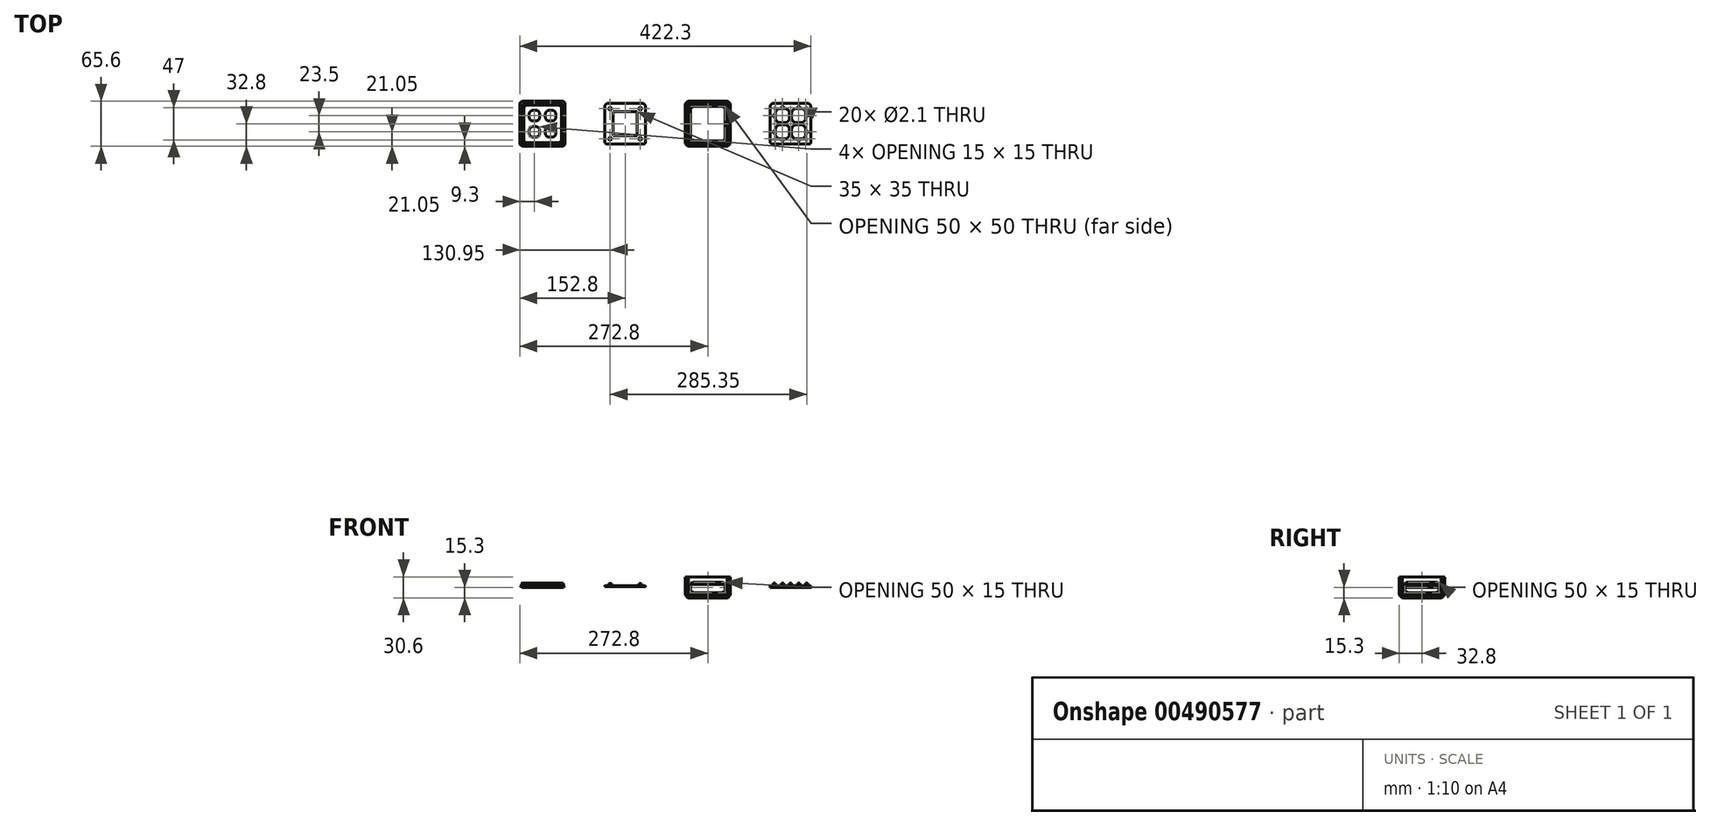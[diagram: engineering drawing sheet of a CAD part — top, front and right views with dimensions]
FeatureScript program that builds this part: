
annotation { "Feature Type Name" : "Feature", "Feature Type Description" : "" }
export const myFeature = defineFeature(function(context is Context, id is Id, definition is map)
    precondition{}
    {
        {
            assignVariable(context, id + "F0", {"name" : "Grosor", "anyValue" : 2.8});
        }
        {
            assignVariable(context, id + "F1", {"name" : "AltoPlaca", "anyValue" : 15});
        }
        {
            assignVariable(context, id + "F2", {"name" : "AltoBriX", "anyValue" : 10});
        }
        {
            var Q0;
            Q0=qCreatedBy(makeId("Top.planeOp"),FACE);
            var sketch = newSketch(context, id + "F3", { "sketchPlane" : qUnion([Q0])});
            skLineSegment(sketch, "E0.bottom", {"start": v(30, -30) * mm, "end": v(-30, -30) * mm});
            skLineSegment(sketch, "E0.top", {"start": v(30, 30) * mm, "end": v(-30, 30) * mm});
            skLineSegment(sketch, "E0.left", {"start": v(30, -30) * mm, "end": v(30, 30) * mm});
            skLineSegment(sketch, "E0.right", {"start": v(-30, -30) * mm, "end": v(-30, 30) * mm});
            skPoint(sketch, "E0.middle", {"position": v(0, 0) * mm});
            skLineSegment(sketch, "E1.0", {"start": v(32.8, 32.8) * mm, "end": v(-32.8, 32.8) * mm});
            skLineSegment(sketch, "E1.1", {"start": v(32.8, -32.8) * mm, "end": v(32.8, 32.8) * mm});
            skLineSegment(sketch, "E1.2", {"start": v(32.8, -32.8) * mm, "end": v(-32.8, -32.8) * mm});
            skLineSegment(sketch, "E1.3", {"start": v(-32.8, -32.8) * mm, "end": v(-32.8, 32.8) * mm});
            skLineSegment(sketch, "E2.bottom", {"start": v(-25, 32.8) * mm, "end": v(25, 32.8) * mm});
            skLineSegment(sketch, "E2.top", {"start": v(-25, -32.8) * mm, "end": v(25, -32.8) * mm});
            skLineSegment(sketch, "E2.left", {"start": v(-25, 32.8) * mm, "end": v(-25, -32.8) * mm});
            skLineSegment(sketch, "E2.right", {"start": v(25, 32.8) * mm, "end": v(25, -32.8) * mm});
            skLineSegment(sketch, "E3.bottom", {"start": v(-32.8, 25) * mm, "end": v(32.8, 25) * mm});
            skLineSegment(sketch, "E3.top", {"start": v(-32.8, -25) * mm, "end": v(32.8, -25) * mm});
            skLineSegment(sketch, "E3.left", {"start": v(-32.8, 25) * mm, "end": v(-32.8, -25) * mm});
            skLineSegment(sketch, "E3.right", {"start": v(32.8, 25) * mm, "end": v(32.8, -25) * mm});
            skSolve(sketch);
        }
        {
            var Q0;
            {var subQ0=sQuery(id+"F3.wireOp",EDGE,"E2.right");var subQ1=sQuery(id+"F3.wireOp",EDGE,"E0.top");var subQ2=makeQuery(id+"F3.imprint","INTERSECT",VERTEX,{"derivedFrom":[subQ1,subQ0]});Q0=makeQuery(id+"F3.imprint","IMPRINT",FACE,{"disambiguationData":[TD([[makeQuery(id+"F3.imprint","IMPRINT",EDGE,{"disambiguationData":[TD([[subQ2,-1.0]])],"derivedFrom":subQ1}),-1.0]])]});}
            var Q1;
            {var subQ7=sQuery(id+"F3.wireOp",EDGE,"E0.right");var subQ8=sQuery(id+"F3.wireOp",EDGE,"E0.top");var subQ9=makeQuery(id+"F3.imprint","INTERSECT",VERTEX,{"derivedFrom":[subQ8,subQ7]});Q1=makeQuery(id+"F3.imprint","IMPRINT",FACE,{"disambiguationData":[TD([[makeQuery(id+"F3.imprint","IMPRINT",EDGE,{"disambiguationData":[TD([[subQ9,1.0]])],"derivedFrom":subQ8}),-1.0]])]});}
            var Q2;
            {var subQ6=sQuery(id+"F3.wireOp",EDGE,"E0.top");var subQ9=sQuery(id+"F3.wireOp",EDGE,"E2.right");var subQ11=makeQuery(id+"F3.imprint","INTERSECT",VERTEX,{"derivedFrom":[subQ6,subQ9]});Q2=makeQuery(id+"F3.imprint","IMPRINT",FACE,{"disambiguationData":[TD([[makeQuery(id+"F3.imprint","IMPRINT",EDGE,{"disambiguationData":[TD([[subQ11,1.0]])],"derivedFrom":subQ6}),-1.0]])]});}
            var Q3;
            {var subQ0=sQuery(id+"F3.wireOp",EDGE,"E3.top");var subQ1=sQuery(id+"F3.wireOp",EDGE,"E0.left");var subQ2=makeQuery(id+"F3.imprint","INTERSECT",VERTEX,{"derivedFrom":[subQ1,subQ0]});Q3=makeQuery(id+"F3.imprint","IMPRINT",FACE,{"disambiguationData":[TD([[makeQuery(id+"F3.imprint","IMPRINT",EDGE,{"disambiguationData":[TD([[subQ2,-1.0]])],"derivedFrom":subQ1}),-1.0]])]});}
            var Q4;
            {var subQ0=sQuery(id+"F3.wireOp",EDGE,"E2.right");var subQ8=sQuery(id+"F3.wireOp",EDGE,"E0.bottom");var subQ11=makeQuery(id+"F3.imprint","INTERSECT",VERTEX,{"derivedFrom":[subQ8,subQ0]});Q4=makeQuery(id+"F3.imprint","IMPRINT",FACE,{"disambiguationData":[TD([[makeQuery(id+"F3.imprint","IMPRINT",EDGE,{"disambiguationData":[TD([[subQ11,1.0]])],"derivedFrom":subQ8}),1.0]])]});}
            var Q5;
            {var subQ0=sQuery(id+"F3.wireOp",EDGE,"E2.right");var subQ1=sQuery(id+"F3.wireOp",EDGE,"E0.bottom");var subQ2=makeQuery(id+"F3.imprint","INTERSECT",VERTEX,{"derivedFrom":[subQ1,subQ0]});Q5=makeQuery(id+"F3.imprint","IMPRINT",FACE,{"disambiguationData":[TD([[makeQuery(id+"F3.imprint","IMPRINT",EDGE,{"disambiguationData":[TD([[subQ2,-1.0]])],"derivedFrom":subQ1}),1.0]])]});}
            var Q6;
            {var subQ6=sQuery(id+"F3.wireOp",EDGE,"E0.right");var subQ9=sQuery(id+"F3.wireOp",EDGE,"E0.bottom");var subQ10=makeQuery(id+"F3.imprint","INTERSECT",VERTEX,{"derivedFrom":[subQ9,subQ6]});Q6=makeQuery(id+"F3.imprint","IMPRINT",FACE,{"disambiguationData":[TD([[makeQuery(id+"F3.imprint","IMPRINT",EDGE,{"disambiguationData":[TD([[subQ10,1.0]])],"derivedFrom":subQ9}),1.0]])]});}
            var Q7;
            {var subQ0=sQuery(id+"F3.wireOp",EDGE,"E3.top");var subQ1=sQuery(id+"F3.wireOp",EDGE,"E0.right");var subQ2=makeQuery(id+"F3.imprint","INTERSECT",VERTEX,{"derivedFrom":[subQ1,subQ0]});Q7=makeQuery(id+"F3.imprint","IMPRINT",FACE,{"disambiguationData":[TD([[makeQuery(id+"F3.imprint","IMPRINT",EDGE,{"disambiguationData":[TD([[subQ2,-1.0]])],"derivedFrom":subQ1}),1.0]])]});}
            var Q8;
            {var subQ0=sQuery(id+"F3.wireOp",EDGE,"E2.right");var subQ1=sQuery(id+"F3.wireOp",EDGE,"E0.bottom");var subQ2=makeQuery(id+"F3.imprint","INTERSECT",VERTEX,{"derivedFrom":[subQ1,subQ0]});Q8=makeQuery(id+"F3.imprint","IMPRINT",FACE,{"disambiguationData":[TD([[makeQuery(id+"F3.imprint","IMPRINT",EDGE,{"disambiguationData":[TD([[subQ2,1.0]])],"derivedFrom":subQ1}),-1.0]])]});}
            var Q9;
            {var subQ0=sQuery(id+"F3.wireOp",EDGE,"E2.right");var subQ1=sQuery(id+"F3.wireOp",EDGE,"E0.top");var subQ2=makeQuery(id+"F3.imprint","INTERSECT",VERTEX,{"derivedFrom":[subQ1,subQ0]});Q9=makeQuery(id+"F3.imprint","IMPRINT",FACE,{"disambiguationData":[TD([[makeQuery(id+"F3.imprint","IMPRINT",EDGE,{"disambiguationData":[TD([[subQ2,1.0]])],"derivedFrom":subQ1}),1.0]])]});}
            var Q10;
            {var subQ0=sQuery(id+"F3.wireOp",EDGE,"E0.right");var subQ1=sQuery(id+"F3.wireOp",EDGE,"E0.top");var subQ2=makeQuery(id+"F3.imprint","INTERSECT",VERTEX,{"derivedFrom":[subQ1,subQ0]});Q10=makeQuery(id+"F3.imprint","IMPRINT",FACE,{"disambiguationData":[TD([[makeQuery(id+"F3.imprint","IMPRINT",EDGE,{"disambiguationData":[TD([[subQ2,1.0]])],"derivedFrom":subQ1}),1.0]])]});}
            var Q11;
            {var subQ0=sQuery(id+"F3.wireOp",EDGE,"E3.top");var subQ1=sQuery(id+"F3.wireOp",EDGE,"E0.right");var subQ2=makeQuery(id+"F3.imprint","INTERSECT",VERTEX,{"derivedFrom":[subQ1,subQ0]});Q11=makeQuery(id+"F3.imprint","IMPRINT",FACE,{"disambiguationData":[TD([[makeQuery(id+"F3.imprint","IMPRINT",EDGE,{"disambiguationData":[TD([[subQ2,-1.0]])],"derivedFrom":subQ1}),-1.0]])]});}
            var Q12;
            {var subQ0=sQuery(id+"F3.wireOp",EDGE,"E3.top");var subQ1=sQuery(id+"F3.wireOp",EDGE,"E0.left");var subQ2=makeQuery(id+"F3.imprint","INTERSECT",VERTEX,{"derivedFrom":[subQ1,subQ0]});Q12=makeQuery(id+"F3.imprint","IMPRINT",FACE,{"disambiguationData":[TD([[makeQuery(id+"F3.imprint","IMPRINT",EDGE,{"disambiguationData":[TD([[subQ2,-1.0]])],"derivedFrom":subQ1}),1.0]])]});}
            var Q13;
            {var subQ0=sQuery(id+"F3.wireOp",EDGE,"E0.right");var subQ1=sQuery(id+"F3.wireOp",EDGE,"E0.bottom");var subQ2=makeQuery(id+"F3.imprint","INTERSECT",VERTEX,{"derivedFrom":[subQ1,subQ0]});Q13=makeQuery(id+"F3.imprint","IMPRINT",FACE,{"disambiguationData":[TD([[makeQuery(id+"F3.imprint","IMPRINT",EDGE,{"disambiguationData":[TD([[subQ2,1.0]])],"derivedFrom":subQ1}),-1.0]])]});}
            var Q14;
            {var subQ0=sQuery(id+"F3.wireOp",EDGE,"E2.right");var subQ1=sQuery(id+"F3.wireOp",EDGE,"E0.bottom");var subQ2=makeQuery(id+"F3.imprint","INTERSECT",VERTEX,{"derivedFrom":[subQ1,subQ0]});Q14=makeQuery(id+"F3.imprint","IMPRINT",FACE,{"disambiguationData":[TD([[makeQuery(id+"F3.imprint","IMPRINT",EDGE,{"disambiguationData":[TD([[subQ2,-1.0]])],"derivedFrom":subQ1}),-1.0]])]});}
            var Q15;
            {var subQ0=sQuery(id+"F3.wireOp",EDGE,"E2.right");var subQ1=sQuery(id+"F3.wireOp",EDGE,"E0.top");var subQ2=makeQuery(id+"F3.imprint","INTERSECT",VERTEX,{"derivedFrom":[subQ1,subQ0]});Q15=makeQuery(id+"F3.imprint","IMPRINT",FACE,{"disambiguationData":[TD([[makeQuery(id+"F3.imprint","IMPRINT",EDGE,{"disambiguationData":[TD([[subQ2,-1.0]])],"derivedFrom":subQ1}),1.0]])]});}
            extrude(context, id + "F4", {"entities" : qUnion([Q0, Q1, Q2, Q3, Q4, Q5, Q6, Q7, Q8, Q9, Q10, Q11, Q12, Q13, Q14, Q15]), "depth" : (getVariable(context, 'AltoBriX') + getVariable(context, 'Grosor')) * mm, "hasSecondDirection" : true, "secondDirectionOppositeDirection" : true, "secondDirectionDepth" : (getVariable(context, 'AltoPlaca') + getVariable(context, 'Grosor')) * mm});
        }
        {
            var Q0;
            {var subQ0=sQuery(id+"F3.wireOp",EDGE,"E3.top");var subQ1=sQuery(id+"F3.wireOp",EDGE,"E0.right");var subQ2=makeQuery(id+"F3.imprint","INTERSECT",VERTEX,{"derivedFrom":[subQ1,subQ0]});Q0=makeQuery(id+"F3.imprint","IMPRINT",FACE,{"disambiguationData":[TD([[makeQuery(id+"F3.imprint","IMPRINT",EDGE,{"disambiguationData":[TD([[subQ2,-1.0]])],"derivedFrom":subQ1}),-1.0]])]});}
            var Q1;
            {var subQ0=sQuery(id+"F3.wireOp",EDGE,"E2.right");var subQ1=sQuery(id+"F3.wireOp",EDGE,"E0.top");var subQ2=makeQuery(id+"F3.imprint","INTERSECT",VERTEX,{"derivedFrom":[subQ1,subQ0]});Q1=makeQuery(id+"F3.imprint","IMPRINT",FACE,{"disambiguationData":[TD([[makeQuery(id+"F3.imprint","IMPRINT",EDGE,{"disambiguationData":[TD([[subQ2,-1.0]])],"derivedFrom":subQ1}),1.0]])]});}
            var Q2;
            {var subQ0=sQuery(id+"F3.wireOp",EDGE,"E0.right");var subQ1=sQuery(id+"F3.wireOp",EDGE,"E0.top");var subQ2=makeQuery(id+"F3.imprint","INTERSECT",VERTEX,{"derivedFrom":[subQ1,subQ0]});Q2=makeQuery(id+"F3.imprint","IMPRINT",FACE,{"disambiguationData":[TD([[makeQuery(id+"F3.imprint","IMPRINT",EDGE,{"disambiguationData":[TD([[subQ2,1.0]])],"derivedFrom":subQ1}),1.0]])]});}
            var Q3;
            {var subQ0=sQuery(id+"F3.wireOp",EDGE,"E3.top");var subQ1=sQuery(id+"F3.wireOp",EDGE,"E0.left");var subQ2=makeQuery(id+"F3.imprint","INTERSECT",VERTEX,{"derivedFrom":[subQ1,subQ0]});Q3=makeQuery(id+"F3.imprint","IMPRINT",FACE,{"disambiguationData":[TD([[makeQuery(id+"F3.imprint","IMPRINT",EDGE,{"disambiguationData":[TD([[subQ2,-1.0]])],"derivedFrom":subQ1}),1.0]])]});}
            var Q4;
            {var subQ0=sQuery(id+"F3.wireOp",EDGE,"E2.right");var subQ1=sQuery(id+"F3.wireOp",EDGE,"E0.top");var subQ2=makeQuery(id+"F3.imprint","INTERSECT",VERTEX,{"derivedFrom":[subQ1,subQ0]});Q4=makeQuery(id+"F3.imprint","IMPRINT",FACE,{"disambiguationData":[TD([[makeQuery(id+"F3.imprint","IMPRINT",EDGE,{"disambiguationData":[TD([[subQ2,1.0]])],"derivedFrom":subQ1}),1.0]])]});}
            var Q5;
            {var subQ0=sQuery(id+"F3.wireOp",EDGE,"E0.right");var subQ1=sQuery(id+"F3.wireOp",EDGE,"E0.bottom");var subQ2=makeQuery(id+"F3.imprint","INTERSECT",VERTEX,{"derivedFrom":[subQ1,subQ0]});Q5=makeQuery(id+"F3.imprint","IMPRINT",FACE,{"disambiguationData":[TD([[makeQuery(id+"F3.imprint","IMPRINT",EDGE,{"disambiguationData":[TD([[subQ2,1.0]])],"derivedFrom":subQ1}),-1.0]])]});}
            var Q6;
            {var subQ0=sQuery(id+"F3.wireOp",EDGE,"E2.right");var subQ1=sQuery(id+"F3.wireOp",EDGE,"E0.bottom");var subQ2=makeQuery(id+"F3.imprint","INTERSECT",VERTEX,{"derivedFrom":[subQ1,subQ0]});Q6=makeQuery(id+"F3.imprint","IMPRINT",FACE,{"disambiguationData":[TD([[makeQuery(id+"F3.imprint","IMPRINT",EDGE,{"disambiguationData":[TD([[subQ2,-1.0]])],"derivedFrom":subQ1}),-1.0]])]});}
            var Q7;
            {var subQ0=sQuery(id+"F3.wireOp",EDGE,"E2.right");var subQ1=sQuery(id+"F3.wireOp",EDGE,"E0.bottom");var subQ2=makeQuery(id+"F3.imprint","INTERSECT",VERTEX,{"derivedFrom":[subQ1,subQ0]});Q7=makeQuery(id+"F3.imprint","IMPRINT",FACE,{"disambiguationData":[TD([[makeQuery(id+"F3.imprint","IMPRINT",EDGE,{"disambiguationData":[TD([[subQ2,1.0]])],"derivedFrom":subQ1}),-1.0]])]});}
            extrude(context, id + "F5", {"entities" : qUnion([Q0, Q1, Q2, Q3, Q4, Q5, Q6, Q7]), "operationType" : NewBodyOperationType.REMOVE, "depth" : (getVariable(context, 'AltoBriX') + getVariable(context, 'Grosor')) * mm, "hasSecondDirection" : true, "secondDirectionOppositeDirection" : true, "secondDirectionDepth" : (getVariable(context, 'AltoPlaca')) * mm});
        }
        {
            var Q0;
            {var subQ0=sQuery(id+"F3.wireOp",EDGE,"E3.top");var subQ1=sQuery(id+"F3.wireOp",EDGE,"E0.right");var subQ2=makeQuery(id+"F3.imprint","INTERSECT",VERTEX,{"derivedFrom":[subQ1,subQ0]});Q0=makeQuery(id+"F3.imprint","IMPRINT",FACE,{"disambiguationData":[TD([[makeQuery(id+"F3.imprint","IMPRINT",EDGE,{"disambiguationData":[TD([[subQ2,-1.0]])],"derivedFrom":subQ1}),1.0]])]});}
            var Q1;
            {var subQ0=sQuery(id+"F3.wireOp",EDGE,"E3.top");var subQ1=sQuery(id+"F3.wireOp",EDGE,"E0.left");var subQ2=makeQuery(id+"F3.imprint","INTERSECT",VERTEX,{"derivedFrom":[subQ1,subQ0]});Q1=makeQuery(id+"F3.imprint","IMPRINT",FACE,{"disambiguationData":[TD([[makeQuery(id+"F3.imprint","IMPRINT",EDGE,{"disambiguationData":[TD([[subQ2,-1.0]])],"derivedFrom":subQ1}),-1.0]])]});}
            var Q2;
            {var subQ0=sQuery(id+"F3.wireOp",EDGE,"E2.right");var subQ1=sQuery(id+"F3.wireOp",EDGE,"E0.bottom");var subQ2=makeQuery(id+"F3.imprint","INTERSECT",VERTEX,{"derivedFrom":[subQ1,subQ0]});Q2=makeQuery(id+"F3.imprint","IMPRINT",FACE,{"disambiguationData":[TD([[makeQuery(id+"F3.imprint","IMPRINT",EDGE,{"disambiguationData":[TD([[subQ2,-1.0]])],"derivedFrom":subQ1}),1.0]])]});}
            var Q3;
            {var subQ0=sQuery(id+"F3.wireOp",EDGE,"E2.right");var subQ1=sQuery(id+"F3.wireOp",EDGE,"E0.top");var subQ2=makeQuery(id+"F3.imprint","INTERSECT",VERTEX,{"derivedFrom":[subQ1,subQ0]});Q3=makeQuery(id+"F3.imprint","IMPRINT",FACE,{"disambiguationData":[TD([[makeQuery(id+"F3.imprint","IMPRINT",EDGE,{"disambiguationData":[TD([[subQ2,-1.0]])],"derivedFrom":subQ1}),-1.0]])]});}
            extrude(context, id + "F6", {"entities" : qUnion([Q0, Q1, Q2, Q3]), "operationType" : NewBodyOperationType.REMOVE, "depth" : (getVariable(context, 'AltoBriX') - 5) * mm, "hasSecondDirection" : true, "secondDirectionOppositeDirection" : true, "secondDirectionDepth" : (getVariable(context, 'AltoPlaca') - 5) * mm});
        }
        {
            var Q0;
            {var subQ0=sQuery(id+"F3.wireOp",EDGE,"E3.bottom");Q0=makeQuery(id+"F6.boolean.opBoolean","COPY",EDGE,{"derivedFrom":makeQuery(id+"F6.opExtrude","CAP_EDGE",EDGE,{"disambiguationData":[OSD([subQ0]),TDD([makeQuery(id+"F3.imprint","IMPRINT",EDGE,{"disambiguationData":[TD([[makeQuery(id+"F3.imprint","INTERSECT",VERTEX,{"derivedFrom":[sQuery(id+"F3.wireOp",EDGE,"E0.right"),subQ0]}),1.0]])],"derivedFrom":subQ0})])],"isStart":false})});}
            var Q1;
            {var subQ0=sQuery(id+"F3.wireOp",EDGE,"E3.bottom");Q1=makeQuery(id+"F6.boolean.opBoolean","COPY",EDGE,{"derivedFrom":makeQuery(id+"F6.opExtrude","CAP_EDGE",EDGE,{"disambiguationData":[OSD([subQ0]),TDD([makeQuery(id+"F3.imprint","IMPRINT",EDGE,{"disambiguationData":[TD([[makeQuery(id+"F3.imprint","INTERSECT",VERTEX,{"derivedFrom":[sQuery(id+"F3.wireOp",EDGE,"E0.right"),subQ0]}),1.0]])],"derivedFrom":subQ0})])],"isStart":true})});}
            var Q2;
            {var subQ0=sQuery(id+"F3.wireOp",EDGE,"E3.top");Q2=makeQuery(id+"F6.boolean.opBoolean","COPY",EDGE,{"derivedFrom":makeQuery(id+"F6.opExtrude","CAP_EDGE",EDGE,{"disambiguationData":[OSD([subQ0]),TDD([makeQuery(id+"F3.imprint","IMPRINT",EDGE,{"disambiguationData":[TD([[makeQuery(id+"F3.imprint","INTERSECT",VERTEX,{"derivedFrom":[sQuery(id+"F3.wireOp",EDGE,"E0.right"),subQ0]}),1.0]])],"derivedFrom":subQ0})])],"isStart":false})});}
            var Q3;
            {var subQ0=sQuery(id+"F3.wireOp",EDGE,"E2.right");Q3=makeQuery(id+"F6.boolean.opBoolean","COPY",EDGE,{"derivedFrom":makeQuery(id+"F6.opExtrude","CAP_EDGE",EDGE,{"disambiguationData":[OSD([subQ0]),TDD([makeQuery(id+"F3.imprint","IMPRINT",EDGE,{"disambiguationData":[TD([[makeQuery(id+"F3.imprint","INTERSECT",VERTEX,{"derivedFrom":[sQuery(id+"F3.wireOp",EDGE,"E0.bottom"),subQ0]}),-1.0]])],"derivedFrom":subQ0})])],"isStart":false})});}
            var Q4;
            {var subQ0=sQuery(id+"F3.wireOp",EDGE,"E3.top");Q4=makeQuery(id+"F6.boolean.opBoolean","COPY",EDGE,{"derivedFrom":makeQuery(id+"F6.opExtrude","CAP_EDGE",EDGE,{"disambiguationData":[OSD([subQ0]),TDD([makeQuery(id+"F3.imprint","IMPRINT",EDGE,{"disambiguationData":[TD([[makeQuery(id+"F3.imprint","INTERSECT",VERTEX,{"derivedFrom":[sQuery(id+"F3.wireOp",EDGE,"E0.left"),subQ0]}),-1.0]])],"derivedFrom":subQ0})])],"isStart":false})});}
            var Q5;
            {var subQ0=sQuery(id+"F3.wireOp",EDGE,"E3.top");Q5=makeQuery(id+"F6.boolean.opBoolean","COPY",EDGE,{"derivedFrom":makeQuery(id+"F6.opExtrude","CAP_EDGE",EDGE,{"disambiguationData":[OSD([subQ0]),TDD([makeQuery(id+"F3.imprint","IMPRINT",EDGE,{"disambiguationData":[TD([[makeQuery(id+"F3.imprint","INTERSECT",VERTEX,{"derivedFrom":[sQuery(id+"F3.wireOp",EDGE,"E0.left"),subQ0]}),-1.0]])],"derivedFrom":subQ0})])],"isStart":true})});}
            var Q6;
            {var subQ0=sQuery(id+"F3.wireOp",EDGE,"E2.right");Q6=makeQuery(id+"F6.boolean.opBoolean","COPY",EDGE,{"derivedFrom":makeQuery(id+"F6.opExtrude","CAP_EDGE",EDGE,{"disambiguationData":[OSD([subQ0]),TDD([makeQuery(id+"F3.imprint","IMPRINT",EDGE,{"disambiguationData":[TD([[makeQuery(id+"F3.imprint","INTERSECT",VERTEX,{"derivedFrom":[sQuery(id+"F3.wireOp",EDGE,"E0.bottom"),subQ0]}),-1.0]])],"derivedFrom":subQ0})])],"isStart":true})});}
            var Q7;
            {var subQ0=sQuery(id+"F3.wireOp",EDGE,"E3.top");Q7=makeQuery(id+"F6.boolean.opBoolean","COPY",EDGE,{"derivedFrom":makeQuery(id+"F6.opExtrude","CAP_EDGE",EDGE,{"disambiguationData":[OSD([subQ0]),TDD([makeQuery(id+"F3.imprint","IMPRINT",EDGE,{"disambiguationData":[TD([[makeQuery(id+"F3.imprint","INTERSECT",VERTEX,{"derivedFrom":[sQuery(id+"F3.wireOp",EDGE,"E0.right"),subQ0]}),1.0]])],"derivedFrom":subQ0})])],"isStart":true})});}
            var Q8;
            {var subQ0=sQuery(id+"F3.wireOp",EDGE,"E2.left");Q8=makeQuery(id+"F6.boolean.opBoolean","COPY",EDGE,{"derivedFrom":makeQuery(id+"F6.opExtrude","CAP_EDGE",EDGE,{"disambiguationData":[OSD([subQ0]),TDD([makeQuery(id+"F3.imprint","IMPRINT",EDGE,{"disambiguationData":[TD([[makeQuery(id+"F3.imprint","INTERSECT",VERTEX,{"derivedFrom":[sQuery(id+"F3.wireOp",EDGE,"E1.2"),subQ0]}),1.0]])],"derivedFrom":subQ0})])],"isStart":true})});}
            var Q9;
            {var subQ0=sQuery(id+"F3.wireOp",EDGE,"E2.left");Q9=makeQuery(id+"F6.boolean.opBoolean","COPY",EDGE,{"derivedFrom":makeQuery(id+"F6.opExtrude","CAP_EDGE",EDGE,{"disambiguationData":[OSD([subQ0]),TDD([makeQuery(id+"F3.imprint","IMPRINT",EDGE,{"disambiguationData":[TD([[makeQuery(id+"F3.imprint","INTERSECT",VERTEX,{"derivedFrom":[sQuery(id+"F3.wireOp",EDGE,"E1.2"),subQ0]}),1.0]])],"derivedFrom":subQ0})])],"isStart":false})});}
            var Q10;
            {var subQ0=sQuery(id+"F3.wireOp",EDGE,"E3.bottom");Q10=makeQuery(id+"F6.boolean.opBoolean","COPY",EDGE,{"derivedFrom":makeQuery(id+"F6.opExtrude","CAP_EDGE",EDGE,{"disambiguationData":[OSD([subQ0]),TDD([makeQuery(id+"F3.imprint","IMPRINT",EDGE,{"disambiguationData":[TD([[makeQuery(id+"F3.imprint","INTERSECT",VERTEX,{"derivedFrom":[sQuery(id+"F3.wireOp",EDGE,"E1.1"),subQ0]}),1.0]])],"derivedFrom":subQ0})])],"isStart":true})});}
            var Q11;
            {var subQ0=sQuery(id+"F3.wireOp",EDGE,"E3.bottom");Q11=makeQuery(id+"F6.boolean.opBoolean","COPY",EDGE,{"derivedFrom":makeQuery(id+"F6.opExtrude","CAP_EDGE",EDGE,{"disambiguationData":[OSD([subQ0]),TDD([makeQuery(id+"F3.imprint","IMPRINT",EDGE,{"disambiguationData":[TD([[makeQuery(id+"F3.imprint","INTERSECT",VERTEX,{"derivedFrom":[sQuery(id+"F3.wireOp",EDGE,"E1.1"),subQ0]}),1.0]])],"derivedFrom":subQ0})])],"isStart":false})});}
            var Q12;
            {var subQ0=sQuery(id+"F3.wireOp",EDGE,"E2.left");Q12=makeQuery(id+"F6.boolean.opBoolean","COPY",EDGE,{"derivedFrom":makeQuery(id+"F6.opExtrude","CAP_EDGE",EDGE,{"disambiguationData":[OSD([subQ0]),TDD([makeQuery(id+"F3.imprint","IMPRINT",EDGE,{"disambiguationData":[TD([[makeQuery(id+"F3.imprint","INTERSECT",VERTEX,{"derivedFrom":[sQuery(id+"F3.wireOp",EDGE,"E1.0"),subQ0]}),-1.0]])],"derivedFrom":subQ0})])],"isStart":false})});}
            var Q13;
            {var subQ0=sQuery(id+"F3.wireOp",EDGE,"E2.left");Q13=makeQuery(id+"F6.boolean.opBoolean","COPY",EDGE,{"derivedFrom":makeQuery(id+"F6.opExtrude","CAP_EDGE",EDGE,{"disambiguationData":[OSD([subQ0]),TDD([makeQuery(id+"F3.imprint","IMPRINT",EDGE,{"disambiguationData":[TD([[makeQuery(id+"F3.imprint","INTERSECT",VERTEX,{"derivedFrom":[sQuery(id+"F3.wireOp",EDGE,"E1.0"),subQ0]}),-1.0]])],"derivedFrom":subQ0})])],"isStart":true})});}
            var Q14;
            {var subQ0=sQuery(id+"F3.wireOp",EDGE,"E2.right");Q14=makeQuery(id+"F6.boolean.opBoolean","COPY",EDGE,{"derivedFrom":makeQuery(id+"F6.opExtrude","CAP_EDGE",EDGE,{"disambiguationData":[OSD([subQ0]),TDD([makeQuery(id+"F3.imprint","IMPRINT",EDGE,{"disambiguationData":[TD([[makeQuery(id+"F3.imprint","INTERSECT",VERTEX,{"derivedFrom":[sQuery(id+"F3.wireOp",EDGE,"E0.top"),subQ0]}),1.0]])],"derivedFrom":subQ0})])],"isStart":false})});}
            var Q15;
            {var subQ0=sQuery(id+"F3.wireOp",EDGE,"E2.right");Q15=makeQuery(id+"F6.boolean.opBoolean","COPY",EDGE,{"derivedFrom":makeQuery(id+"F6.opExtrude","CAP_EDGE",EDGE,{"disambiguationData":[OSD([subQ0]),TDD([makeQuery(id+"F3.imprint","IMPRINT",EDGE,{"disambiguationData":[TD([[makeQuery(id+"F3.imprint","INTERSECT",VERTEX,{"derivedFrom":[sQuery(id+"F3.wireOp",EDGE,"E0.top"),subQ0]}),1.0]])],"derivedFrom":subQ0})])],"isStart":true})});}
            var Q16;
            Q16=makeQuery(id+"F4.opExtrude","SWEPT_EDGE",EDGE,{"disambiguationData":[OSD([sQuery(id+"F3.wireOp",EDGE,"E2.right"),sQuery(id+"F3.wireOp",EDGE,"E3.top")])]});
            var Q17;
            Q17=makeQuery(id+"F4.opExtrude","SWEPT_EDGE",EDGE,{"disambiguationData":[OSD([sQuery(id+"F3.wireOp",EDGE,"E2.left"),sQuery(id+"F3.wireOp",EDGE,"E3.top")])]});
            var Q18;
            Q18=makeQuery(id+"F4.opExtrude","SWEPT_EDGE",EDGE,{"disambiguationData":[OSD([sQuery(id+"F3.wireOp",EDGE,"E2.left"),sQuery(id+"F3.wireOp",EDGE,"E3.bottom")])]});
            var Q19;
            Q19=makeQuery(id+"F4.opExtrude","SWEPT_EDGE",EDGE,{"disambiguationData":[OSD([sQuery(id+"F3.wireOp",EDGE,"E2.right"),sQuery(id+"F3.wireOp",EDGE,"E3.bottom")])]});
            fillet(context, id + "F7", {"entities" : qUnion([Q0, Q1, Q2, Q3, Q4, Q5, Q6, Q7, Q8, Q9, Q10, Q11, Q12, Q13, Q14, Q15, Q16, Q17, Q18, Q19]), "radius" : 5 * mm, "tangentPropagation" : true, "allowEdgeOverflow" : false});
        }
        {
            var Q0;
            Q0=qCreatedBy(makeId("Top.planeOp"),FACE);
            cPlane(context, id + "F8", {"entities" : qUnion([Q0]), "cplaneType" : CPlaneType.OFFSET, "offset" : (getVariable(context, 'AltoBriX') - 5) * mm, "width" : 150 * mm, "height" : 150 * mm});
        }
        {
            var Q0;
            Q0=qCreatedBy(id+"F8.planeOp",FACE);
            var sketch = newSketch(context, id + "F9", { "sketchPlane" : qUnion([Q0])});
            skLineSegment(sketch, "E4", {"start": v(0, 0) * mm, "end": v(-31.4, 0) * mm, "construction": true});
            skLineSegment(sketch, "E5", {"start": v(0, 0) * mm, "end": v(0, 31.4) * mm, "construction": true});
            skLineSegment(sketch, "E6", {"start": v(0, 0) * mm, "end": v(-16.82, 16.82) * mm, "construction": true});
            skLineSegment(sketch, "E7", {"start": v(0, 0) * mm, "end": v(10.62, -10.62) * mm, "construction": true});
            skLineSegment(sketch, "E8.bottom", {"start": v(-0.3, 30.25) * mm, "end": v(0.3, 30.25) * mm});
            skLineSegment(sketch, "E8.top", {"start": v(-0.3, 32.55) * mm, "end": v(0.3, 32.55) * mm});
            skLineSegment(sketch, "E8.left", {"start": v(-0.3, 30.25) * mm, "end": v(-0.3, 32.55) * mm});
            skLineSegment(sketch, "E8.right", {"start": v(0.3, 30.25) * mm, "end": v(0.3, 32.55) * mm});
            skPoint(sketch, "E8.middle", {"position": v(0, 31.4) * mm});
            skLineSegment(sketch, "E9", {"start": v(0, 0) * mm, "end": v(15.28, 0) * mm, "construction": true});
            skLineSegment(sketch, "E10.MirrorCS", {"start": v(0, 0) * mm, "end": v(0, -31.4) * mm, "construction": true});
            skPoint(sketch, "E11.1.0.0", {"position": v(5, 31.4) * mm});
            skPoint(sketch, "E11.1.0.1", {"position": v(5, 31.4) * mm});
            skLineSegment(sketch, "E11.1.0.2", {"start": v(4.7, 30.25) * mm, "end": v(5.3, 30.25) * mm});
            skLineSegment(sketch, "E11.1.0.3", {"start": v(4.7, 32.55) * mm, "end": v(5.3, 32.55) * mm});
            skLineSegment(sketch, "E11.1.0.4", {"start": v(4.7, 30.25) * mm, "end": v(4.7, 32.55) * mm});
            skLineSegment(sketch, "E11.1.0.5", {"start": v(5.3, 30.25) * mm, "end": v(5.3, 32.55) * mm});
            skPoint(sketch, "E11.2.0.0", {"position": v(10, 31.4) * mm});
            skPoint(sketch, "E11.2.0.1", {"position": v(10, 31.4) * mm});
            skLineSegment(sketch, "E11.2.0.2", {"start": v(9.7, 30.25) * mm, "end": v(10.3, 30.25) * mm});
            skLineSegment(sketch, "E11.2.0.3", {"start": v(9.7, 32.55) * mm, "end": v(10.3, 32.55) * mm});
            skLineSegment(sketch, "E11.2.0.4", {"start": v(9.7, 30.25) * mm, "end": v(9.7, 32.55) * mm});
            skLineSegment(sketch, "E11.2.0.5", {"start": v(10.3, 30.25) * mm, "end": v(10.3, 32.55) * mm});
            skPoint(sketch, "E11.3.0.0", {"position": v(15, 31.4) * mm});
            skPoint(sketch, "E11.3.0.1", {"position": v(15, 31.4) * mm});
            skLineSegment(sketch, "E11.3.0.2", {"start": v(14.7, 30.25) * mm, "end": v(15.3, 30.25) * mm});
            skLineSegment(sketch, "E11.3.0.3", {"start": v(14.7, 32.55) * mm, "end": v(15.3, 32.55) * mm});
            skLineSegment(sketch, "E11.3.0.4", {"start": v(14.7, 30.25) * mm, "end": v(14.7, 32.55) * mm});
            skLineSegment(sketch, "E11.3.0.5", {"start": v(15.3, 30.25) * mm, "end": v(15.3, 32.55) * mm});
            skPoint(sketch, "E11.4.0.0", {"position": v(20, 31.4) * mm});
            skPoint(sketch, "E11.4.0.1", {"position": v(20, 31.4) * mm});
            skLineSegment(sketch, "E11.4.0.2", {"start": v(19.7, 30.25) * mm, "end": v(20.3, 30.25) * mm});
            skLineSegment(sketch, "E11.4.0.3", {"start": v(19.7, 32.55) * mm, "end": v(20.3, 32.55) * mm});
            skLineSegment(sketch, "E11.4.0.4", {"start": v(19.7, 30.25) * mm, "end": v(19.7, 32.55) * mm});
            skLineSegment(sketch, "E11.4.0.5", {"start": v(20.3, 30.25) * mm, "end": v(20.3, 32.55) * mm});
            skLineSegment(sketch, "E11.direction1", {"start": v(-0.3, 30.25) * mm, "end": v(4.7, 30.25) * mm, "construction": true});
            skPoint(sketch, "E12.1.0.0", {"position": v(-5, 31.4) * mm});
            skLineSegment(sketch, "E12.1.0.1", {"start": v(-4.7, 30.25) * mm, "end": v(-4.7, 32.55) * mm});
            skLineSegment(sketch, "E12.1.0.2", {"start": v(-5.3, 30.25) * mm, "end": v(-5.3, 32.55) * mm});
            skPoint(sketch, "E12.1.0.3", {"position": v(-5, 31.4) * mm});
            skLineSegment(sketch, "E12.1.0.4", {"start": v(-5.3, 32.55) * mm, "end": v(-4.7, 32.55) * mm});
            skLineSegment(sketch, "E12.1.0.5", {"start": v(-5.3, 30.25) * mm, "end": v(-4.7, 30.25) * mm});
            skPoint(sketch, "E12.2.0.0", {"position": v(-10, 31.4) * mm});
            skLineSegment(sketch, "E12.2.0.1", {"start": v(-9.7, 30.25) * mm, "end": v(-9.7, 32.55) * mm});
            skLineSegment(sketch, "E12.2.0.2", {"start": v(-10.3, 30.25) * mm, "end": v(-10.3, 32.55) * mm});
            skPoint(sketch, "E12.2.0.3", {"position": v(-10, 31.4) * mm});
            skLineSegment(sketch, "E12.2.0.4", {"start": v(-10.3, 32.55) * mm, "end": v(-9.7, 32.55) * mm});
            skLineSegment(sketch, "E12.2.0.5", {"start": v(-10.3, 30.25) * mm, "end": v(-9.7, 30.25) * mm});
            skPoint(sketch, "E12.3.0.0", {"position": v(-15, 31.4) * mm});
            skLineSegment(sketch, "E12.3.0.1", {"start": v(-14.7, 30.25) * mm, "end": v(-14.7, 32.55) * mm});
            skLineSegment(sketch, "E12.3.0.2", {"start": v(-15.3, 30.25) * mm, "end": v(-15.3, 32.55) * mm});
            skPoint(sketch, "E12.3.0.3", {"position": v(-15, 31.4) * mm});
            skLineSegment(sketch, "E12.3.0.4", {"start": v(-15.3, 32.55) * mm, "end": v(-14.7, 32.55) * mm});
            skLineSegment(sketch, "E12.3.0.5", {"start": v(-15.3, 30.25) * mm, "end": v(-14.7, 30.25) * mm});
            skPoint(sketch, "E12.4.0.0", {"position": v(-20, 31.4) * mm});
            skLineSegment(sketch, "E12.4.0.1", {"start": v(-19.7, 30.25) * mm, "end": v(-19.7, 32.55) * mm});
            skLineSegment(sketch, "E12.4.0.2", {"start": v(-20.3, 30.25) * mm, "end": v(-20.3, 32.55) * mm});
            skPoint(sketch, "E12.4.0.3", {"position": v(-20, 31.4) * mm});
            skLineSegment(sketch, "E12.4.0.4", {"start": v(-20.3, 32.55) * mm, "end": v(-19.7, 32.55) * mm});
            skLineSegment(sketch, "E12.4.0.5", {"start": v(-20.3, 30.25) * mm, "end": v(-19.7, 30.25) * mm});
            skLineSegment(sketch, "E12.direction1", {"start": v(-0.3, 30.25) * mm, "end": v(-5.3, 30.25) * mm, "construction": true});
            skLineSegment(sketch, "E13.MirrorCS", {"start": v(-0.3, -30.25) * mm, "end": v(0.3, -30.25) * mm});
            skLineSegment(sketch, "E14.MirrorCS", {"start": v(9.7, -30.25) * mm, "end": v(10.3, -30.25) * mm});
            skLineSegment(sketch, "E15.MirrorCS", {"start": v(5.3, -30.25) * mm, "end": v(5.3, -32.55) * mm});
            skLineSegment(sketch, "E16.MirrorCS", {"start": v(4.7, -30.25) * mm, "end": v(4.7, -32.55) * mm});
            skLineSegment(sketch, "E17.MirrorCS", {"start": v(4.7, -32.55) * mm, "end": v(5.3, -32.55) * mm});
            skLineSegment(sketch, "E18.MirrorCS", {"start": v(4.7, -30.25) * mm, "end": v(5.3, -30.25) * mm});
            skLineSegment(sketch, "E19.MirrorCS", {"start": v(19.7, -30.25) * mm, "end": v(20.3, -30.25) * mm});
            skLineSegment(sketch, "E20.MirrorCS", {"start": v(-0.3, -30.25) * mm, "end": v(-0.3, -32.55) * mm});
            skLineSegment(sketch, "E21.MirrorCS", {"start": v(-0.3, -32.55) * mm, "end": v(0.3, -32.55) * mm});
            skLineSegment(sketch, "E22.MirrorCS", {"start": v(0.3, -30.25) * mm, "end": v(0.3, -32.55) * mm});
            skLineSegment(sketch, "E23.MirrorCS", {"start": v(-5.3, -30.25) * mm, "end": v(-4.7, -30.25) * mm});
            skLineSegment(sketch, "E24.MirrorCS", {"start": v(14.7, -30.25) * mm, "end": v(15.3, -30.25) * mm});
            skLineSegment(sketch, "E25.MirrorCS", {"start": v(20.3, -30.25) * mm, "end": v(20.3, -32.55) * mm});
            skLineSegment(sketch, "E26.MirrorCS", {"start": v(-20.3, -32.55) * mm, "end": v(-19.7, -32.55) * mm});
            skLineSegment(sketch, "E27.MirrorCS", {"start": v(-5.3, -32.55) * mm, "end": v(-4.7, -32.55) * mm});
            skLineSegment(sketch, "E28.MirrorCS", {"start": v(-5.3, -30.25) * mm, "end": v(-5.3, -32.55) * mm});
            skLineSegment(sketch, "E29.MirrorCS", {"start": v(19.7, -30.25) * mm, "end": v(19.7, -32.55) * mm});
            skLineSegment(sketch, "E30.MirrorCS", {"start": v(-20.3, -30.25) * mm, "end": v(-20.3, -32.55) * mm});
            skLineSegment(sketch, "E31.MirrorCS", {"start": v(-4.7, -30.25) * mm, "end": v(-4.7, -32.55) * mm});
            skLineSegment(sketch, "E32.MirrorCS", {"start": v(-0.3, -30.25) * mm, "end": v(-5.3, -30.25) * mm, "construction": true});
            skLineSegment(sketch, "E33.MirrorCS", {"start": v(-20.3, -30.25) * mm, "end": v(-19.7, -30.25) * mm});
            skLineSegment(sketch, "E34.MirrorCS", {"start": v(-15.3, -30.25) * mm, "end": v(-14.7, -30.25) * mm});
            skLineSegment(sketch, "E35.MirrorCS", {"start": v(19.7, -32.55) * mm, "end": v(20.3, -32.55) * mm});
            skLineSegment(sketch, "E36.MirrorCS", {"start": v(-19.7, -30.25) * mm, "end": v(-19.7, -32.55) * mm});
            skLineSegment(sketch, "E37.MirrorCS", {"start": v(15.3, -30.25) * mm, "end": v(15.3, -32.55) * mm});
            skLineSegment(sketch, "E38.MirrorCS", {"start": v(-15.3, -32.55) * mm, "end": v(-14.7, -32.55) * mm});
            skLineSegment(sketch, "E39.MirrorCS", {"start": v(14.7, -30.25) * mm, "end": v(14.7, -32.55) * mm});
            skLineSegment(sketch, "E40.MirrorCS", {"start": v(-15.3, -30.25) * mm, "end": v(-15.3, -32.55) * mm});
            skLineSegment(sketch, "E41.MirrorCS", {"start": v(-10.3, -30.25) * mm, "end": v(-9.7, -30.25) * mm});
            skLineSegment(sketch, "E42.MirrorCS", {"start": v(14.7, -32.55) * mm, "end": v(15.3, -32.55) * mm});
            skLineSegment(sketch, "E43.MirrorCS", {"start": v(-14.7, -30.25) * mm, "end": v(-14.7, -32.55) * mm});
            skLineSegment(sketch, "E44.MirrorCS", {"start": v(-10.3, -30.25) * mm, "end": v(-10.3, -32.55) * mm});
            skLineSegment(sketch, "E45.MirrorCS", {"start": v(9.7, -32.55) * mm, "end": v(10.3, -32.55) * mm});
            skLineSegment(sketch, "E46.MirrorCS", {"start": v(10.3, -30.25) * mm, "end": v(10.3, -32.55) * mm});
            skLineSegment(sketch, "E47.MirrorCS", {"start": v(-10.3, -32.55) * mm, "end": v(-9.7, -32.55) * mm});
            skLineSegment(sketch, "E48.MirrorCS", {"start": v(-9.7, -30.25) * mm, "end": v(-9.7, -32.55) * mm});
            skLineSegment(sketch, "E49.MirrorCS", {"start": v(9.7, -30.25) * mm, "end": v(9.7, -32.55) * mm});
            skPoint(sketch, "E50.MirrorP", {"position": v(0, -31.4) * mm});
            skPoint(sketch, "E51.MirrorP", {"position": v(-15, -31.4) * mm});
            skPoint(sketch, "E52.MirrorP", {"position": v(20, -31.4) * mm});
            skPoint(sketch, "E53.MirrorP", {"position": v(15, -31.4) * mm});
            skLineSegment(sketch, "E54.MirrorCS", {"start": v(-0.3, -30.25) * mm, "end": v(4.7, -30.25) * mm, "construction": true});
            skPoint(sketch, "E55.MirrorP", {"position": v(-5, -31.4) * mm});
            skPoint(sketch, "E56.MirrorP", {"position": v(-20, -31.4) * mm});
            skPoint(sketch, "E57.MirrorP", {"position": v(-10, -31.4) * mm});
            skPoint(sketch, "E58.MirrorP", {"position": v(10, -31.4) * mm});
            skPoint(sketch, "E59.MirrorP", {"position": v(5, -31.4) * mm});
            skLineSegment(sketch, "E60.bottom", {"start": v(-25, 31.25) * mm, "end": v(25, 31.25) * mm});
            skLineSegment(sketch, "E60.top", {"start": v(-25, 31.55) * mm, "end": v(25, 31.55) * mm});
            skLineSegment(sketch, "E60.left", {"start": v(-25, 31.25) * mm, "end": v(-25, 31.55) * mm});
            skLineSegment(sketch, "E60.right", {"start": v(25, 31.25) * mm, "end": v(25, 31.55) * mm});
            skLineSegment(sketch, "E61.MirrorCS", {"start": v(-25, -31.55) * mm, "end": v(25, -31.55) * mm});
            skLineSegment(sketch, "E62.MirrorCS", {"start": v(-25, -31.25) * mm, "end": v(25, -31.25) * mm});
            skLineSegment(sketch, "E63.MirrorCS", {"start": v(25, -31.25) * mm, "end": v(25, -31.55) * mm});
            skLineSegment(sketch, "E64.MirrorCS", {"start": v(-25, -31.25) * mm, "end": v(-25, -31.55) * mm});
            skLineSegment(sketch, "E65.bottom", {"start": v(-32.55, 0.3) * mm, "end": v(-30.25, 0.3) * mm});
            skLineSegment(sketch, "E65.top", {"start": v(-32.55, -0.3) * mm, "end": v(-30.25, -0.3) * mm});
            skLineSegment(sketch, "E65.left", {"start": v(-32.55, 0.3) * mm, "end": v(-32.55, -0.3) * mm});
            skLineSegment(sketch, "E65.right", {"start": v(-30.25, 0.3) * mm, "end": v(-30.25, -0.3) * mm});
            skPoint(sketch, "E65.middle", {"position": v(-31.4, 0) * mm});
            skLineSegment(sketch, "E66.1.0.0", {"start": v(-32.54, -4.7) * mm, "end": v(-32.54, -5.3) * mm});
            skLineSegment(sketch, "E66.1.0.1", {"start": v(-30.24, -4.7) * mm, "end": v(-30.24, -5.3) * mm});
            skPoint(sketch, "E66.1.0.2", {"position": v(-31.4, -5) * mm});
            skLineSegment(sketch, "E66.1.0.3", {"start": v(-32.54, -4.7) * mm, "end": v(-30.24, -4.7) * mm});
            skLineSegment(sketch, "E66.1.0.4", {"start": v(-32.54, -5.3) * mm, "end": v(-30.24, -5.3) * mm});
            skLineSegment(sketch, "E66.2.0.0", {"start": v(-32.53, -9.7) * mm, "end": v(-32.53, -10.3) * mm});
            skLineSegment(sketch, "E66.2.0.1", {"start": v(-30.23, -9.7) * mm, "end": v(-30.23, -10.3) * mm});
            skPoint(sketch, "E66.2.0.2", {"position": v(-31.38, -10) * mm});
            skLineSegment(sketch, "E66.2.0.3", {"start": v(-32.53, -9.7) * mm, "end": v(-30.23, -9.7) * mm});
            skLineSegment(sketch, "E66.2.0.4", {"start": v(-32.53, -10.3) * mm, "end": v(-30.23, -10.3) * mm});
            skLineSegment(sketch, "E66.3.0.0", {"start": v(-32.53, -14.7) * mm, "end": v(-32.53, -15.3) * mm});
            skLineSegment(sketch, "E66.3.0.1", {"start": v(-30.23, -14.7) * mm, "end": v(-30.23, -15.3) * mm});
            skPoint(sketch, "E66.3.0.2", {"position": v(-31.38, -15) * mm});
            skLineSegment(sketch, "E66.3.0.3", {"start": v(-32.53, -14.7) * mm, "end": v(-30.23, -14.7) * mm});
            skLineSegment(sketch, "E66.3.0.4", {"start": v(-32.53, -15.3) * mm, "end": v(-30.23, -15.3) * mm});
            skLineSegment(sketch, "E66.4.0.0", {"start": v(-32.52, -19.7) * mm, "end": v(-32.52, -20.3) * mm});
            skLineSegment(sketch, "E66.4.0.1", {"start": v(-30.22, -19.7) * mm, "end": v(-30.22, -20.3) * mm});
            skPoint(sketch, "E66.4.0.2", {"position": v(-31.37, -20) * mm});
            skLineSegment(sketch, "E66.4.0.3", {"start": v(-32.52, -19.7) * mm, "end": v(-30.22, -19.7) * mm});
            skLineSegment(sketch, "E66.4.0.4", {"start": v(-32.52, -20.3) * mm, "end": v(-30.22, -20.3) * mm});
            skLineSegment(sketch, "E66.5.0.0", {"start": v(-32.5, -24.7) * mm, "end": v(-32.5, -25.3) * mm});
            skLineSegment(sketch, "E66.5.0.1", {"start": v(-30.2, -24.7) * mm, "end": v(-30.2, -25.3) * mm});
            skPoint(sketch, "E66.5.0.2", {"position": v(-31.36, -25) * mm});
            skLineSegment(sketch, "E66.5.0.3", {"start": v(-32.5, -24.7) * mm, "end": v(-30.2, -24.7) * mm});
            skLineSegment(sketch, "E66.5.0.4", {"start": v(-32.5, -25.3) * mm, "end": v(-30.2, -25.3) * mm});
            skLineSegment(sketch, "E66.6.0.0", {"start": v(-32.5, -29.7) * mm, "end": v(-32.5, -30.3) * mm});
            skLineSegment(sketch, "E66.6.0.1", {"start": v(-30.2, -29.7) * mm, "end": v(-30.2, -30.3) * mm});
            skPoint(sketch, "E66.6.0.2", {"position": v(-31.35, -30) * mm});
            skLineSegment(sketch, "E66.6.0.3", {"start": v(-32.5, -29.7) * mm, "end": v(-30.2, -29.7) * mm});
            skLineSegment(sketch, "E66.6.0.4", {"start": v(-32.5, -30.3) * mm, "end": v(-30.2, -30.3) * mm});
            skLineSegment(sketch, "E66.direction1", {"start": v(-32.55, -0.3) * mm, "end": v(-32.54, -5.3) * mm, "construction": true});
            skLineSegment(sketch, "E67.1.0.0", {"start": v(-32.55, 4.7) * mm, "end": v(-30.25, 4.7) * mm});
            skPoint(sketch, "E67.1.0.1", {"position": v(-31.4, 5) * mm});
            skLineSegment(sketch, "E67.1.0.2", {"start": v(-32.55, 5.3) * mm, "end": v(-30.25, 5.3) * mm});
            skLineSegment(sketch, "E67.1.0.3", {"start": v(-30.25, 5.3) * mm, "end": v(-30.25, 4.7) * mm});
            skLineSegment(sketch, "E67.1.0.4", {"start": v(-32.55, 5.3) * mm, "end": v(-32.55, 4.7) * mm});
            skLineSegment(sketch, "E67.2.0.0", {"start": v(-32.55, 9.7) * mm, "end": v(-30.25, 9.7) * mm});
            skPoint(sketch, "E67.2.0.1", {"position": v(-31.4, 10) * mm});
            skLineSegment(sketch, "E67.2.0.2", {"start": v(-32.55, 10.3) * mm, "end": v(-30.25, 10.3) * mm});
            skLineSegment(sketch, "E67.2.0.3", {"start": v(-30.25, 10.3) * mm, "end": v(-30.25, 9.7) * mm});
            skLineSegment(sketch, "E67.2.0.4", {"start": v(-32.55, 10.3) * mm, "end": v(-32.55, 9.7) * mm});
            skLineSegment(sketch, "E67.3.0.0", {"start": v(-32.55, 14.7) * mm, "end": v(-30.25, 14.7) * mm});
            skPoint(sketch, "E67.3.0.1", {"position": v(-31.4, 15) * mm});
            skLineSegment(sketch, "E67.3.0.2", {"start": v(-32.55, 15.3) * mm, "end": v(-30.25, 15.3) * mm});
            skLineSegment(sketch, "E67.3.0.3", {"start": v(-30.25, 15.3) * mm, "end": v(-30.25, 14.7) * mm});
            skLineSegment(sketch, "E67.3.0.4", {"start": v(-32.55, 15.3) * mm, "end": v(-32.55, 14.7) * mm});
            skLineSegment(sketch, "E67.4.0.0", {"start": v(-32.55, 19.7) * mm, "end": v(-30.25, 19.7) * mm});
            skPoint(sketch, "E67.4.0.1", {"position": v(-31.4, 20) * mm});
            skLineSegment(sketch, "E67.4.0.2", {"start": v(-32.55, 20.3) * mm, "end": v(-30.25, 20.3) * mm});
            skLineSegment(sketch, "E67.4.0.3", {"start": v(-30.25, 20.3) * mm, "end": v(-30.25, 19.7) * mm});
            skLineSegment(sketch, "E67.4.0.4", {"start": v(-32.55, 20.3) * mm, "end": v(-32.55, 19.7) * mm});
            skLineSegment(sketch, "E67.5.0.0", {"start": v(-32.55, 24.7) * mm, "end": v(-30.25, 24.7) * mm});
            skPoint(sketch, "E67.5.0.1", {"position": v(-31.4, 25) * mm});
            skLineSegment(sketch, "E67.5.0.2", {"start": v(-32.55, 25.3) * mm, "end": v(-30.25, 25.3) * mm});
            skLineSegment(sketch, "E67.5.0.3", {"start": v(-30.25, 25.3) * mm, "end": v(-30.25, 24.7) * mm});
            skLineSegment(sketch, "E67.5.0.4", {"start": v(-32.55, 25.3) * mm, "end": v(-32.55, 24.7) * mm});
            skLineSegment(sketch, "E67.6.0.0", {"start": v(-32.55, 29.7) * mm, "end": v(-30.25, 29.7) * mm});
            skPoint(sketch, "E67.6.0.1", {"position": v(-31.4, 30) * mm});
            skLineSegment(sketch, "E67.6.0.2", {"start": v(-32.55, 30.3) * mm, "end": v(-30.25, 30.3) * mm});
            skLineSegment(sketch, "E67.6.0.3", {"start": v(-30.25, 30.3) * mm, "end": v(-30.25, 29.7) * mm});
            skLineSegment(sketch, "E67.6.0.4", {"start": v(-32.55, 30.3) * mm, "end": v(-32.55, 29.7) * mm});
            skLineSegment(sketch, "E67.direction1", {"start": v(-32.55, -0.3) * mm, "end": v(-32.55, 4.7) * mm, "construction": true});
            skLineSegment(sketch, "E68.MirrorCS", {"start": v(32.55, 0.3) * mm, "end": v(32.55, -0.3) * mm});
            skLineSegment(sketch, "E69.MirrorCS", {"start": v(32.55, -0.3) * mm, "end": v(30.25, -0.3) * mm});
            skLineSegment(sketch, "E70.MirrorCS", {"start": v(32.55, 0.3) * mm, "end": v(30.25, 0.3) * mm});
            skLineSegment(sketch, "E71.MirrorCS", {"start": v(32.5, -24.7) * mm, "end": v(32.5, -25.3) * mm});
            skLineSegment(sketch, "E72.MirrorCS", {"start": v(32.55, 20.3) * mm, "end": v(32.55, 19.7) * mm});
            skLineSegment(sketch, "E73.MirrorCS", {"start": v(30.2, -24.7) * mm, "end": v(30.2, -25.3) * mm});
            skLineSegment(sketch, "E74.MirrorCS", {"start": v(30.25, 0.3) * mm, "end": v(30.25, -0.3) * mm});
            skLineSegment(sketch, "E75.MirrorCS", {"start": v(30.25, 20.3) * mm, "end": v(30.25, 19.7) * mm});
            skLineSegment(sketch, "E76.MirrorCS", {"start": v(32.5, -24.7) * mm, "end": v(30.2, -24.7) * mm});
            skLineSegment(sketch, "E77.MirrorCS", {"start": v(32.5, -25.3) * mm, "end": v(30.2, -25.3) * mm});
            skLineSegment(sketch, "E78.MirrorCS", {"start": v(32.55, 20.3) * mm, "end": v(30.25, 20.3) * mm});
            skLineSegment(sketch, "E79.MirrorCS", {"start": v(32.55, 19.7) * mm, "end": v(30.25, 19.7) * mm});
            skLineSegment(sketch, "E80.MirrorCS", {"start": v(30.23, -9.7) * mm, "end": v(30.23, -10.3) * mm});
            skLineSegment(sketch, "E81.MirrorCS", {"start": v(30.24, -4.7) * mm, "end": v(30.24, -5.3) * mm});
            skLineSegment(sketch, "E82.MirrorCS", {"start": v(32.52, -20.3) * mm, "end": v(30.22, -20.3) * mm});
            skLineSegment(sketch, "E83.MirrorCS", {"start": v(32.53, -9.7) * mm, "end": v(32.53, -10.3) * mm});
            skLineSegment(sketch, "E84.MirrorCS", {"start": v(32.55, -0.3) * mm, "end": v(32.55, 4.7) * mm, "construction": true});
            skLineSegment(sketch, "E85.MirrorCS", {"start": v(32.53, -10.3) * mm, "end": v(30.23, -10.3) * mm});
            skLineSegment(sketch, "E86.MirrorCS", {"start": v(32.53, -9.7) * mm, "end": v(30.23, -9.7) * mm});
            skLineSegment(sketch, "E87.MirrorCS", {"start": v(32.55, 9.7) * mm, "end": v(30.25, 9.7) * mm});
            skLineSegment(sketch, "E88.MirrorCS", {"start": v(32.55, 29.7) * mm, "end": v(30.25, 29.7) * mm});
            skLineSegment(sketch, "E89.MirrorCS", {"start": v(30.22, -19.7) * mm, "end": v(30.22, -20.3) * mm});
            skLineSegment(sketch, "E90.MirrorCS", {"start": v(30.25, 30.3) * mm, "end": v(30.25, 29.7) * mm});
            skLineSegment(sketch, "E91.MirrorCS", {"start": v(32.52, -19.7) * mm, "end": v(30.22, -19.7) * mm});
            skLineSegment(sketch, "E92.MirrorCS", {"start": v(30.25, 10.3) * mm, "end": v(30.25, 9.7) * mm});
            skLineSegment(sketch, "E93.MirrorCS", {"start": v(32.54, -5.3) * mm, "end": v(30.24, -5.3) * mm});
            skLineSegment(sketch, "E94.MirrorCS", {"start": v(32.55, 5.3) * mm, "end": v(30.25, 5.3) * mm});
            skLineSegment(sketch, "E95.MirrorCS", {"start": v(30.2, -29.7) * mm, "end": v(30.2, -30.3) * mm});
            skLineSegment(sketch, "E96.MirrorCS", {"start": v(30.23, -14.7) * mm, "end": v(30.23, -15.3) * mm});
            skLineSegment(sketch, "E97.MirrorCS", {"start": v(32.55, 4.7) * mm, "end": v(30.25, 4.7) * mm});
            skLineSegment(sketch, "E98.MirrorCS", {"start": v(32.54, -4.7) * mm, "end": v(30.24, -4.7) * mm});
            skLineSegment(sketch, "E99.MirrorCS", {"start": v(32.55, 5.3) * mm, "end": v(32.55, 4.7) * mm});
            skLineSegment(sketch, "E100.MirrorCS", {"start": v(32.55, 30.3) * mm, "end": v(30.25, 30.3) * mm});
            skLineSegment(sketch, "E101.MirrorCS", {"start": v(32.55, 10.3) * mm, "end": v(30.25, 10.3) * mm});
            skLineSegment(sketch, "E102.MirrorCS", {"start": v(32.55, 24.7) * mm, "end": v(30.25, 24.7) * mm});
            skLineSegment(sketch, "E103.MirrorCS", {"start": v(32.5, -30.3) * mm, "end": v(30.2, -30.3) * mm});
            skLineSegment(sketch, "E104.MirrorCS", {"start": v(32.53, -14.7) * mm, "end": v(32.53, -15.3) * mm});
            skLineSegment(sketch, "E105.MirrorCS", {"start": v(32.55, 15.3) * mm, "end": v(32.55, 14.7) * mm});
            skLineSegment(sketch, "E106.MirrorCS", {"start": v(32.55, 10.3) * mm, "end": v(32.55, 9.7) * mm});
            skLineSegment(sketch, "E107.MirrorCS", {"start": v(32.55, 30.3) * mm, "end": v(32.55, 29.7) * mm});
            skLineSegment(sketch, "E108.MirrorCS", {"start": v(32.55, 14.7) * mm, "end": v(30.25, 14.7) * mm});
            skLineSegment(sketch, "E109.MirrorCS", {"start": v(32.54, -4.7) * mm, "end": v(32.54, -5.3) * mm});
            skLineSegment(sketch, "E110.MirrorCS", {"start": v(32.5, -29.7) * mm, "end": v(30.2, -29.7) * mm});
            skLineSegment(sketch, "E111.MirrorCS", {"start": v(32.55, 15.3) * mm, "end": v(30.25, 15.3) * mm});
            skLineSegment(sketch, "E112.MirrorCS", {"start": v(30.25, 15.3) * mm, "end": v(30.25, 14.7) * mm});
            skLineSegment(sketch, "E113.MirrorCS", {"start": v(30.25, 5.3) * mm, "end": v(30.25, 4.7) * mm});
            skLineSegment(sketch, "E114.MirrorCS", {"start": v(32.53, -14.7) * mm, "end": v(30.23, -14.7) * mm});
            skLineSegment(sketch, "E115.MirrorCS", {"start": v(32.55, 25.3) * mm, "end": v(30.25, 25.3) * mm});
            skLineSegment(sketch, "E116.MirrorCS", {"start": v(30.25, 25.3) * mm, "end": v(30.25, 24.7) * mm});
            skLineSegment(sketch, "E117.MirrorCS", {"start": v(32.53, -15.3) * mm, "end": v(30.23, -15.3) * mm});
            skLineSegment(sketch, "E118.MirrorCS", {"start": v(32.5, -29.7) * mm, "end": v(32.5, -30.3) * mm});
            skLineSegment(sketch, "E119.MirrorCS", {"start": v(32.55, -0.3) * mm, "end": v(32.54, -5.3) * mm, "construction": true});
            skLineSegment(sketch, "E120.MirrorCS", {"start": v(32.52, -19.7) * mm, "end": v(32.52, -20.3) * mm});
            skLineSegment(sketch, "E121.MirrorCS", {"start": v(32.55, 25.3) * mm, "end": v(32.55, 24.7) * mm});
            skPoint(sketch, "E122.MirrorP", {"position": v(31.4, 0) * mm});
            skPoint(sketch, "E123.MirrorP", {"position": v(31.38, -10) * mm});
            skPoint(sketch, "E124.MirrorP", {"position": v(31.38, -15) * mm});
            skPoint(sketch, "E125.MirrorP", {"position": v(31.4, 15) * mm});
            skPoint(sketch, "E126.MirrorP", {"position": v(31.4, 30) * mm});
            skPoint(sketch, "E127.MirrorP", {"position": v(31.4, 5) * mm});
            skPoint(sketch, "E128.MirrorP", {"position": v(31.36, -25) * mm});
            skPoint(sketch, "E129.MirrorP", {"position": v(31.35, -30) * mm});
            skPoint(sketch, "E130.MirrorP", {"position": v(31.4, 20) * mm});
            skPoint(sketch, "E131.MirrorP", {"position": v(31.4, 10) * mm});
            skPoint(sketch, "E132.MirrorP", {"position": v(31.4, 25) * mm});
            skPoint(sketch, "E133.MirrorP", {"position": v(31.4, -5) * mm});
            skPoint(sketch, "E134.MirrorP", {"position": v(31.37, -20) * mm});
            skLineSegment(sketch, "E135.bottom", {"start": v(-31.6, -25) * mm, "end": v(-31.2, -25) * mm});
            skLineSegment(sketch, "E135.top", {"start": v(-31.6, 25) * mm, "end": v(-31.2, 25) * mm});
            skLineSegment(sketch, "E135.left", {"start": v(-31.6, -25) * mm, "end": v(-31.6, 25) * mm});
            skLineSegment(sketch, "E135.right", {"start": v(-31.2, -25) * mm, "end": v(-31.2, 25) * mm});
            skLineSegment(sketch, "E136.bottom", {"start": v(31.6, -25) * mm, "end": v(31.2, -25) * mm});
            skLineSegment(sketch, "E136.top", {"start": v(31.6, 25) * mm, "end": v(31.2, 25) * mm});
            skLineSegment(sketch, "E136.left", {"start": v(31.6, -25) * mm, "end": v(31.6, 25) * mm});
            skLineSegment(sketch, "E136.right", {"start": v(31.2, -25) * mm, "end": v(31.2, 25) * mm});
            skSolve(sketch);
        }
        {
            var Q0;
            Q0=qSketchRegion(id+"F9",true);
            extrude(context, id + "F10", {"entities" : qUnion([Q0]), "operationType" : NewBodyOperationType.ADD, "oppositeDirection" : true, "depth" : 3 * mm, "hasDraft" : true, "draftAngle" : 3 * degree});
        }
        {
            var Q0;
            {var subQ5=sQuery(id+"F9.wireOp",EDGE,"E60.left");Q0=makeQuery(id+"F9.imprint","IMPRINT",FACE,{"disambiguationData":[TD([[makeQuery(id+"F9.imprint","IMPRINT",EDGE,{"derivedFrom":subQ5}),-1.0]])]});}
            var Q1;
            {var subQ5=sQuery(id+"F9.wireOp",EDGE,"E60.right");Q1=makeQuery(id+"F9.imprint","IMPRINT",FACE,{"disambiguationData":[TD([[makeQuery(id+"F9.imprint","IMPRINT",EDGE,{"derivedFrom":subQ5}),1.0]])]});}
            var Q2;
            {var subQ0=sQuery(id+"F9.wireOp",EDGE,"E136.left");var subQ1=sQuery(id+"F9.wireOp",EDGE,"E78.MirrorCS");var subQ2=makeQuery(id+"F9.imprint","INTERSECT",VERTEX,{"derivedFrom":[subQ1,subQ0]});Q2=makeQuery(id+"F9.imprint","IMPRINT",FACE,{"disambiguationData":[TD([[makeQuery(id+"F9.imprint","IMPRINT",EDGE,{"disambiguationData":[TD([[subQ2,-1.0]])],"derivedFrom":subQ1}),-1.0]])]});}
            var Q3;
            {var subQ0=sQuery(id+"F9.wireOp",EDGE,"E136.left");var subQ1=sQuery(id+"F9.wireOp",EDGE,"E76.MirrorCS");var subQ2=makeQuery(id+"F9.imprint","INTERSECT",VERTEX,{"derivedFrom":[subQ1,subQ0]});Q3=makeQuery(id+"F9.imprint","IMPRINT",FACE,{"disambiguationData":[TD([[makeQuery(id+"F9.imprint","IMPRINT",EDGE,{"disambiguationData":[TD([[subQ2,-1.0]])],"derivedFrom":subQ1}),-1.0]])]});}
            var Q4;
            {var subQ5=sQuery(id+"F9.wireOp",EDGE,"E63.MirrorCS");Q4=makeQuery(id+"F9.imprint","IMPRINT",FACE,{"disambiguationData":[TD([[makeQuery(id+"F9.imprint","IMPRINT",EDGE,{"derivedFrom":subQ5}),-1.0]])]});}
            var Q5;
            {var subQ5=sQuery(id+"F9.wireOp",EDGE,"E64.MirrorCS");Q5=makeQuery(id+"F9.imprint","IMPRINT",FACE,{"disambiguationData":[TD([[makeQuery(id+"F9.imprint","IMPRINT",EDGE,{"derivedFrom":subQ5}),1.0]])]});}
            var Q6;
            {var subQ0=sQuery(id+"F9.wireOp",EDGE,"E135.left");var subQ1=sQuery(id+"F9.wireOp",EDGE,"E66.4.0.4");var subQ2=makeQuery(id+"F9.imprint","INTERSECT",VERTEX,{"derivedFrom":[subQ1,subQ0]});Q6=makeQuery(id+"F9.imprint","IMPRINT",FACE,{"disambiguationData":[TD([[makeQuery(id+"F9.imprint","IMPRINT",EDGE,{"disambiguationData":[TD([[subQ2,-1.0]])],"derivedFrom":subQ1}),-1.0]])]});}
            var Q7;
            {var subQ0=sQuery(id+"F9.wireOp",EDGE,"E135.left");var subQ1=sQuery(id+"F9.wireOp",EDGE,"E67.4.0.2");var subQ2=makeQuery(id+"F9.imprint","INTERSECT",VERTEX,{"derivedFrom":[subQ1,subQ0]});Q7=makeQuery(id+"F9.imprint","IMPRINT",FACE,{"disambiguationData":[TD([[makeQuery(id+"F9.imprint","IMPRINT",EDGE,{"disambiguationData":[TD([[subQ2,-1.0]])],"derivedFrom":subQ1}),1.0]])]});}
            var Q8;
            {var subQ0=sQuery(id+"F9.wireOp",EDGE,"E60.bottom");var subQ1=sQuery(id+"F9.wireOp",EDGE,"E12.2.0.2");var subQ2=makeQuery(id+"F9.imprint","INTERSECT",VERTEX,{"derivedFrom":[subQ1,subQ0]});Q8=makeQuery(id+"F9.imprint","IMPRINT",FACE,{"disambiguationData":[TD([[makeQuery(id+"F9.imprint","IMPRINT",EDGE,{"disambiguationData":[TD([[subQ2,-1.0]])],"derivedFrom":subQ1}),1.0]])]});}
            var Q9;
            {var subQ0=sQuery(id+"F9.wireOp",EDGE,"E62.MirrorCS");var subQ1=sQuery(id+"F9.wireOp",EDGE,"E36.MirrorCS");var subQ2=makeQuery(id+"F9.imprint","INTERSECT",VERTEX,{"derivedFrom":[subQ1,subQ0]});Q9=makeQuery(id+"F9.imprint","IMPRINT",FACE,{"disambiguationData":[TD([[makeQuery(id+"F9.imprint","IMPRINT",EDGE,{"disambiguationData":[TD([[subQ2,-1.0]])],"derivedFrom":subQ1}),1.0]])]});}
            var Q10;
            {var subQ0=sQuery(id+"F9.wireOp",EDGE,"E62.MirrorCS");var subQ1=sQuery(id+"F9.wireOp",EDGE,"E43.MirrorCS");var subQ2=makeQuery(id+"F9.imprint","INTERSECT",VERTEX,{"derivedFrom":[subQ1,subQ0]});Q10=makeQuery(id+"F9.imprint","IMPRINT",FACE,{"disambiguationData":[TD([[makeQuery(id+"F9.imprint","IMPRINT",EDGE,{"disambiguationData":[TD([[subQ2,-1.0]])],"derivedFrom":subQ1}),1.0]])]});}
            var Q11;
            {var subQ0=sQuery(id+"F9.wireOp",EDGE,"E62.MirrorCS");var subQ1=sQuery(id+"F9.wireOp",EDGE,"E28.MirrorCS");var subQ2=makeQuery(id+"F9.imprint","INTERSECT",VERTEX,{"derivedFrom":[subQ1,subQ0]});Q11=makeQuery(id+"F9.imprint","IMPRINT",FACE,{"disambiguationData":[TD([[makeQuery(id+"F9.imprint","IMPRINT",EDGE,{"disambiguationData":[TD([[subQ2,-1.0]])],"derivedFrom":subQ1}),-1.0]])]});}
            var Q12;
            {var subQ0=sQuery(id+"F9.wireOp",EDGE,"E62.MirrorCS");var subQ1=sQuery(id+"F9.wireOp",EDGE,"E20.MirrorCS");var subQ2=makeQuery(id+"F9.imprint","INTERSECT",VERTEX,{"derivedFrom":[subQ1,subQ0]});Q12=makeQuery(id+"F9.imprint","IMPRINT",FACE,{"disambiguationData":[TD([[makeQuery(id+"F9.imprint","IMPRINT",EDGE,{"disambiguationData":[TD([[subQ2,-1.0]])],"derivedFrom":subQ1}),-1.0]])]});}
            var Q13;
            {var subQ0=sQuery(id+"F9.wireOp",EDGE,"E62.MirrorCS");var subQ1=sQuery(id+"F9.wireOp",EDGE,"E16.MirrorCS");var subQ2=makeQuery(id+"F9.imprint","INTERSECT",VERTEX,{"derivedFrom":[subQ1,subQ0]});Q13=makeQuery(id+"F9.imprint","IMPRINT",FACE,{"disambiguationData":[TD([[makeQuery(id+"F9.imprint","IMPRINT",EDGE,{"disambiguationData":[TD([[subQ2,-1.0]])],"derivedFrom":subQ1}),-1.0]])]});}
            var Q14;
            {var subQ0=sQuery(id+"F9.wireOp",EDGE,"E62.MirrorCS");var subQ1=sQuery(id+"F9.wireOp",EDGE,"E15.MirrorCS");var subQ2=makeQuery(id+"F9.imprint","INTERSECT",VERTEX,{"derivedFrom":[subQ1,subQ0]});Q14=makeQuery(id+"F9.imprint","IMPRINT",FACE,{"disambiguationData":[TD([[makeQuery(id+"F9.imprint","IMPRINT",EDGE,{"disambiguationData":[TD([[subQ2,-1.0]])],"derivedFrom":subQ1}),1.0]])]});}
            var Q15;
            {var subQ0=sQuery(id+"F9.wireOp",EDGE,"E62.MirrorCS");var subQ1=sQuery(id+"F9.wireOp",EDGE,"E29.MirrorCS");var subQ2=makeQuery(id+"F9.imprint","INTERSECT",VERTEX,{"derivedFrom":[subQ1,subQ0]});Q15=makeQuery(id+"F9.imprint","IMPRINT",FACE,{"disambiguationData":[TD([[makeQuery(id+"F9.imprint","IMPRINT",EDGE,{"disambiguationData":[TD([[subQ2,-1.0]])],"derivedFrom":subQ1}),-1.0]])]});}
            var Q16;
            {var subQ0=sQuery(id+"F9.wireOp",EDGE,"E62.MirrorCS");var subQ1=sQuery(id+"F9.wireOp",EDGE,"E39.MirrorCS");var subQ2=makeQuery(id+"F9.imprint","INTERSECT",VERTEX,{"derivedFrom":[subQ1,subQ0]});Q16=makeQuery(id+"F9.imprint","IMPRINT",FACE,{"disambiguationData":[TD([[makeQuery(id+"F9.imprint","IMPRINT",EDGE,{"disambiguationData":[TD([[subQ2,-1.0]])],"derivedFrom":subQ1}),-1.0]])]});}
            var Q17;
            {var subQ0=sQuery(id+"F9.wireOp",EDGE,"E136.left");var subQ1=sQuery(id+"F9.wireOp",EDGE,"E91.MirrorCS");var subQ2=makeQuery(id+"F9.imprint","INTERSECT",VERTEX,{"derivedFrom":[subQ1,subQ0]});Q17=makeQuery(id+"F9.imprint","IMPRINT",FACE,{"disambiguationData":[TD([[makeQuery(id+"F9.imprint","IMPRINT",EDGE,{"disambiguationData":[TD([[subQ2,-1.0]])],"derivedFrom":subQ1}),-1.0]])]});}
            var Q18;
            {var subQ0=sQuery(id+"F9.wireOp",EDGE,"E136.left");var subQ1=sQuery(id+"F9.wireOp",EDGE,"E85.MirrorCS");var subQ2=makeQuery(id+"F9.imprint","INTERSECT",VERTEX,{"derivedFrom":[subQ1,subQ0]});Q18=makeQuery(id+"F9.imprint","IMPRINT",FACE,{"disambiguationData":[TD([[makeQuery(id+"F9.imprint","IMPRINT",EDGE,{"disambiguationData":[TD([[subQ2,-1.0]])],"derivedFrom":subQ1}),1.0]])]});}
            var Q19;
            {var subQ0=sQuery(id+"F9.wireOp",EDGE,"E136.left");var subQ1=sQuery(id+"F9.wireOp",EDGE,"E86.MirrorCS");var subQ2=makeQuery(id+"F9.imprint","INTERSECT",VERTEX,{"derivedFrom":[subQ1,subQ0]});Q19=makeQuery(id+"F9.imprint","IMPRINT",FACE,{"disambiguationData":[TD([[makeQuery(id+"F9.imprint","IMPRINT",EDGE,{"disambiguationData":[TD([[subQ2,-1.0]])],"derivedFrom":subQ1}),-1.0]])]});}
            var Q20;
            {var subQ0=sQuery(id+"F9.wireOp",EDGE,"E136.left");var subQ1=sQuery(id+"F9.wireOp",EDGE,"E69.MirrorCS");var subQ2=makeQuery(id+"F9.imprint","INTERSECT",VERTEX,{"derivedFrom":[subQ1,subQ0]});Q20=makeQuery(id+"F9.imprint","IMPRINT",FACE,{"disambiguationData":[TD([[makeQuery(id+"F9.imprint","IMPRINT",EDGE,{"disambiguationData":[TD([[subQ2,-1.0]])],"derivedFrom":subQ1}),1.0]])]});}
            var Q21;
            {var subQ0=sQuery(id+"F9.wireOp",EDGE,"E136.left");var subQ1=sQuery(id+"F9.wireOp",EDGE,"E87.MirrorCS");var subQ2=makeQuery(id+"F9.imprint","INTERSECT",VERTEX,{"derivedFrom":[subQ1,subQ0]});Q21=makeQuery(id+"F9.imprint","IMPRINT",FACE,{"disambiguationData":[TD([[makeQuery(id+"F9.imprint","IMPRINT",EDGE,{"disambiguationData":[TD([[subQ2,-1.0]])],"derivedFrom":subQ1}),1.0]])]});}
            var Q22;
            {var subQ0=sQuery(id+"F9.wireOp",EDGE,"E136.left");var subQ1=sQuery(id+"F9.wireOp",EDGE,"E70.MirrorCS");var subQ2=makeQuery(id+"F9.imprint","INTERSECT",VERTEX,{"derivedFrom":[subQ1,subQ0]});Q22=makeQuery(id+"F9.imprint","IMPRINT",FACE,{"disambiguationData":[TD([[makeQuery(id+"F9.imprint","IMPRINT",EDGE,{"disambiguationData":[TD([[subQ2,-1.0]])],"derivedFrom":subQ1}),-1.0]])]});}
            var Q23;
            {var subQ0=sQuery(id+"F9.wireOp",EDGE,"E136.left");var subQ1=sQuery(id+"F9.wireOp",EDGE,"E101.MirrorCS");var subQ2=makeQuery(id+"F9.imprint","INTERSECT",VERTEX,{"derivedFrom":[subQ1,subQ0]});Q23=makeQuery(id+"F9.imprint","IMPRINT",FACE,{"disambiguationData":[TD([[makeQuery(id+"F9.imprint","IMPRINT",EDGE,{"disambiguationData":[TD([[subQ2,-1.0]])],"derivedFrom":subQ1}),-1.0]])]});}
            var Q24;
            {var subQ0=sQuery(id+"F9.wireOp",EDGE,"E136.left");var subQ1=sQuery(id+"F9.wireOp",EDGE,"E79.MirrorCS");var subQ2=makeQuery(id+"F9.imprint","INTERSECT",VERTEX,{"derivedFrom":[subQ1,subQ0]});Q24=makeQuery(id+"F9.imprint","IMPRINT",FACE,{"disambiguationData":[TD([[makeQuery(id+"F9.imprint","IMPRINT",EDGE,{"disambiguationData":[TD([[subQ2,-1.0]])],"derivedFrom":subQ1}),1.0]])]});}
            var Q25;
            {var subQ0=sQuery(id+"F9.wireOp",EDGE,"E60.bottom");var subQ1=sQuery(id+"F9.wireOp",EDGE,"E11.3.0.5");var subQ2=makeQuery(id+"F9.imprint","INTERSECT",VERTEX,{"derivedFrom":[subQ1,subQ0]});Q25=makeQuery(id+"F9.imprint","IMPRINT",FACE,{"disambiguationData":[TD([[makeQuery(id+"F9.imprint","IMPRINT",EDGE,{"disambiguationData":[TD([[subQ2,-1.0]])],"derivedFrom":subQ1}),-1.0]])]});}
            var Q26;
            {var subQ0=sQuery(id+"F9.wireOp",EDGE,"E60.bottom");var subQ1=sQuery(id+"F9.wireOp",EDGE,"E11.2.0.5");var subQ2=makeQuery(id+"F9.imprint","INTERSECT",VERTEX,{"derivedFrom":[subQ1,subQ0]});Q26=makeQuery(id+"F9.imprint","IMPRINT",FACE,{"disambiguationData":[TD([[makeQuery(id+"F9.imprint","IMPRINT",EDGE,{"disambiguationData":[TD([[subQ2,-1.0]])],"derivedFrom":subQ1}),-1.0]])]});}
            var Q27;
            {var subQ0=sQuery(id+"F9.wireOp",EDGE,"E60.bottom");var subQ1=sQuery(id+"F9.wireOp",EDGE,"E11.1.0.5");var subQ2=makeQuery(id+"F9.imprint","INTERSECT",VERTEX,{"derivedFrom":[subQ1,subQ0]});Q27=makeQuery(id+"F9.imprint","IMPRINT",FACE,{"disambiguationData":[TD([[makeQuery(id+"F9.imprint","IMPRINT",EDGE,{"disambiguationData":[TD([[subQ2,-1.0]])],"derivedFrom":subQ1}),-1.0]])]});}
            var Q28;
            {var subQ0=sQuery(id+"F9.wireOp",EDGE,"E60.bottom");var subQ1=sQuery(id+"F9.wireOp",EDGE,"E8.right");var subQ2=makeQuery(id+"F9.imprint","INTERSECT",VERTEX,{"derivedFrom":[subQ1,subQ0]});Q28=makeQuery(id+"F9.imprint","IMPRINT",FACE,{"disambiguationData":[TD([[makeQuery(id+"F9.imprint","IMPRINT",EDGE,{"disambiguationData":[TD([[subQ2,-1.0]])],"derivedFrom":subQ1}),-1.0]])]});}
            var Q29;
            {var subQ0=sQuery(id+"F9.wireOp",EDGE,"E60.bottom");var subQ1=sQuery(id+"F9.wireOp",EDGE,"E8.left");var subQ2=makeQuery(id+"F9.imprint","INTERSECT",VERTEX,{"derivedFrom":[subQ1,subQ0]});Q29=makeQuery(id+"F9.imprint","IMPRINT",FACE,{"disambiguationData":[TD([[makeQuery(id+"F9.imprint","IMPRINT",EDGE,{"disambiguationData":[TD([[subQ2,-1.0]])],"derivedFrom":subQ1}),1.0]])]});}
            var Q30;
            {var subQ0=sQuery(id+"F9.wireOp",EDGE,"E60.bottom");var subQ1=sQuery(id+"F9.wireOp",EDGE,"E12.1.0.2");var subQ2=makeQuery(id+"F9.imprint","INTERSECT",VERTEX,{"derivedFrom":[subQ1,subQ0]});Q30=makeQuery(id+"F9.imprint","IMPRINT",FACE,{"disambiguationData":[TD([[makeQuery(id+"F9.imprint","IMPRINT",EDGE,{"disambiguationData":[TD([[subQ2,-1.0]])],"derivedFrom":subQ1}),1.0]])]});}
            var Q31;
            {var subQ0=sQuery(id+"F9.wireOp",EDGE,"E60.bottom");var subQ1=sQuery(id+"F9.wireOp",EDGE,"E12.3.0.2");var subQ2=makeQuery(id+"F9.imprint","INTERSECT",VERTEX,{"derivedFrom":[subQ1,subQ0]});Q31=makeQuery(id+"F9.imprint","IMPRINT",FACE,{"disambiguationData":[TD([[makeQuery(id+"F9.imprint","IMPRINT",EDGE,{"disambiguationData":[TD([[subQ2,-1.0]])],"derivedFrom":subQ1}),1.0]])]});}
            var Q32;
            {var subQ0=sQuery(id+"F9.wireOp",EDGE,"E135.left");var subQ1=sQuery(id+"F9.wireOp",EDGE,"E67.3.0.2");var subQ2=makeQuery(id+"F9.imprint","INTERSECT",VERTEX,{"derivedFrom":[subQ1,subQ0]});Q32=makeQuery(id+"F9.imprint","IMPRINT",FACE,{"disambiguationData":[TD([[makeQuery(id+"F9.imprint","IMPRINT",EDGE,{"disambiguationData":[TD([[subQ2,-1.0]])],"derivedFrom":subQ1}),1.0]])]});}
            var Q33;
            {var subQ0=sQuery(id+"F9.wireOp",EDGE,"E135.left");var subQ1=sQuery(id+"F9.wireOp",EDGE,"E67.2.0.2");var subQ2=makeQuery(id+"F9.imprint","INTERSECT",VERTEX,{"derivedFrom":[subQ1,subQ0]});Q33=makeQuery(id+"F9.imprint","IMPRINT",FACE,{"disambiguationData":[TD([[makeQuery(id+"F9.imprint","IMPRINT",EDGE,{"disambiguationData":[TD([[subQ2,-1.0]])],"derivedFrom":subQ1}),1.0]])]});}
            var Q34;
            {var subQ0=sQuery(id+"F9.wireOp",EDGE,"E135.left");var subQ1=sQuery(id+"F9.wireOp",EDGE,"E67.1.0.2");var subQ2=makeQuery(id+"F9.imprint","INTERSECT",VERTEX,{"derivedFrom":[subQ1,subQ0]});Q34=makeQuery(id+"F9.imprint","IMPRINT",FACE,{"disambiguationData":[TD([[makeQuery(id+"F9.imprint","IMPRINT",EDGE,{"disambiguationData":[TD([[subQ2,-1.0]])],"derivedFrom":subQ1}),1.0]])]});}
            var Q35;
            {var subQ0=sQuery(id+"F9.wireOp",EDGE,"E135.left");var subQ1=sQuery(id+"F9.wireOp",EDGE,"E65.bottom");var subQ2=makeQuery(id+"F9.imprint","INTERSECT",VERTEX,{"derivedFrom":[subQ1,subQ0]});Q35=makeQuery(id+"F9.imprint","IMPRINT",FACE,{"disambiguationData":[TD([[makeQuery(id+"F9.imprint","IMPRINT",EDGE,{"disambiguationData":[TD([[subQ2,-1.0]])],"derivedFrom":subQ1}),1.0]])]});}
            var Q36;
            {var subQ0=sQuery(id+"F9.wireOp",EDGE,"E135.left");var subQ1=sQuery(id+"F9.wireOp",EDGE,"E66.1.0.4");var subQ2=makeQuery(id+"F9.imprint","INTERSECT",VERTEX,{"derivedFrom":[subQ1,subQ0]});Q36=makeQuery(id+"F9.imprint","IMPRINT",FACE,{"disambiguationData":[TD([[makeQuery(id+"F9.imprint","IMPRINT",EDGE,{"disambiguationData":[TD([[subQ2,-1.0]])],"derivedFrom":subQ1}),-1.0]])]});}
            var Q37;
            {var subQ0=sQuery(id+"F9.wireOp",EDGE,"E135.left");var subQ1=sQuery(id+"F9.wireOp",EDGE,"E65.top");var subQ2=makeQuery(id+"F9.imprint","INTERSECT",VERTEX,{"derivedFrom":[subQ1,subQ0]});Q37=makeQuery(id+"F9.imprint","IMPRINT",FACE,{"disambiguationData":[TD([[makeQuery(id+"F9.imprint","IMPRINT",EDGE,{"disambiguationData":[TD([[subQ2,-1.0]])],"derivedFrom":subQ1}),-1.0]])]});}
            var Q38;
            {var subQ0=sQuery(id+"F9.wireOp",EDGE,"E135.left");var subQ1=sQuery(id+"F9.wireOp",EDGE,"E66.2.0.4");var subQ2=makeQuery(id+"F9.imprint","INTERSECT",VERTEX,{"derivedFrom":[subQ1,subQ0]});Q38=makeQuery(id+"F9.imprint","IMPRINT",FACE,{"disambiguationData":[TD([[makeQuery(id+"F9.imprint","IMPRINT",EDGE,{"disambiguationData":[TD([[subQ2,-1.0]])],"derivedFrom":subQ1}),-1.0]])]});}
            var Q39;
            {var subQ0=sQuery(id+"F9.wireOp",EDGE,"E135.left");var subQ1=sQuery(id+"F9.wireOp",EDGE,"E66.3.0.4");var subQ2=makeQuery(id+"F9.imprint","INTERSECT",VERTEX,{"derivedFrom":[subQ1,subQ0]});Q39=makeQuery(id+"F9.imprint","IMPRINT",FACE,{"disambiguationData":[TD([[makeQuery(id+"F9.imprint","IMPRINT",EDGE,{"disambiguationData":[TD([[subQ2,-1.0]])],"derivedFrom":subQ1}),-1.0]])]});}
            extrude(context, id + "F11", {"entities" : qUnion([Q0, Q1, Q2, Q3, Q4, Q5, Q6, Q7, Q8, Q9, Q10, Q11, Q12, Q13, Q14, Q15, Q16, Q17, Q18, Q19, Q20, Q21, Q22, Q23, Q24, Q25, Q26, Q27, Q28, Q29, Q30, Q31, Q32, Q33, Q34, Q35, Q36, Q37, Q38, Q39]), "operationType" : NewBodyOperationType.REMOVE, "oppositeDirection" : true, "depth" : 2 * mm, "hasDraft" : true, "draftAngle" : 3 * degree});
        }
        {
            var Q0;
            {var subQ0=sQuery(id+"F3.wireOp",EDGE,"E0.right");var subQ1=sQuery(id+"F3.wireOp",EDGE,"E0.top");var subQ2=makeQuery(id+"F3.imprint","INTERSECT",VERTEX,{"derivedFrom":[subQ1,subQ0]});Q0=makeQuery(id+"F3.imprint","IMPRINT",FACE,{"disambiguationData":[TD([[makeQuery(id+"F3.imprint","IMPRINT",EDGE,{"disambiguationData":[TD([[subQ2,1.0]])],"derivedFrom":subQ1}),1.0]])]});}
            var Q1;
            {var subQ0=sQuery(id+"F3.wireOp",EDGE,"E2.right");var subQ1=sQuery(id+"F3.wireOp",EDGE,"E0.top");var subQ2=makeQuery(id+"F3.imprint","INTERSECT",VERTEX,{"derivedFrom":[subQ1,subQ0]});Q1=makeQuery(id+"F3.imprint","IMPRINT",FACE,{"disambiguationData":[TD([[makeQuery(id+"F3.imprint","IMPRINT",EDGE,{"disambiguationData":[TD([[subQ2,1.0]])],"derivedFrom":subQ1}),1.0]])]});}
            var Q2;
            {var subQ0=sQuery(id+"F3.wireOp",EDGE,"E2.right");var subQ1=sQuery(id+"F3.wireOp",EDGE,"E0.bottom");var subQ2=makeQuery(id+"F3.imprint","INTERSECT",VERTEX,{"derivedFrom":[subQ1,subQ0]});Q2=makeQuery(id+"F3.imprint","IMPRINT",FACE,{"disambiguationData":[TD([[makeQuery(id+"F3.imprint","IMPRINT",EDGE,{"disambiguationData":[TD([[subQ2,1.0]])],"derivedFrom":subQ1}),-1.0]])]});}
            var Q3;
            {var subQ0=sQuery(id+"F3.wireOp",EDGE,"E0.right");var subQ1=sQuery(id+"F3.wireOp",EDGE,"E0.bottom");var subQ2=makeQuery(id+"F3.imprint","INTERSECT",VERTEX,{"derivedFrom":[subQ1,subQ0]});Q3=makeQuery(id+"F3.imprint","IMPRINT",FACE,{"disambiguationData":[TD([[makeQuery(id+"F3.imprint","IMPRINT",EDGE,{"disambiguationData":[TD([[subQ2,1.0]])],"derivedFrom":subQ1}),-1.0]])]});}
            extrude(context, id + "F12", {"entities" : qUnion([Q0, Q1, Q2, Q3]), "operationType" : NewBodyOperationType.ADD, "endBound" : BoundingType.SYMMETRIC, "depth" : (getVariable(context, 'Grosor')) * mm});
        }
        {
            var Q0;
            Q0=makeQuery(id+"F12.opExtrude","SWEPT_EDGE",EDGE,{"disambiguationData":[OSD([sQuery(id+"F3.wireOp",EDGE,"E2.left"),sQuery(id+"F3.wireOp",EDGE,"E3.bottom")])]});
            var Q1;
            Q1=makeQuery(id+"F12.opExtrude","SWEPT_EDGE",EDGE,{"disambiguationData":[OSD([sQuery(id+"F3.wireOp",EDGE,"E2.right"),sQuery(id+"F3.wireOp",EDGE,"E3.bottom")])]});
            var Q2;
            Q2=makeQuery(id+"F12.opExtrude","SWEPT_EDGE",EDGE,{"disambiguationData":[OSD([sQuery(id+"F3.wireOp",EDGE,"E2.right"),sQuery(id+"F3.wireOp",EDGE,"E3.top")])]});
            var Q3;
            Q3=makeQuery(id+"F12.opExtrude","SWEPT_EDGE",EDGE,{"disambiguationData":[OSD([sQuery(id+"F3.wireOp",EDGE,"E2.left"),sQuery(id+"F3.wireOp",EDGE,"E3.top")])]});
            chamfer(context, id + "F13", {"entities" : qUnion([Q0, Q1, Q2, Q3]), "width" : 5 * mm, "tangentPropagation" : true});
        }
        {
            var Q0;
            {var subQ0=sQuery(id+"F3.wireOp",EDGE,"E1.3");Q0=makeQuery(id+"F3vxCluZQKjuGS6_1.boolean.opBoolean","MERGE",EDGE,{"derivedFrom":[makeQuery(id+"F6.opExtrude","CAP_EDGE",EDGE,{"disambiguationData":[OSD([subQ0]),TDD([makeQuery(id+"F3.imprint","IMPRINT",EDGE,{"disambiguationData":[TD([[makeQuery(id+"F3.imprint","INTERSECT",VERTEX,{"derivedFrom":[sQuery(id+"F3.wireOp",EDGE,"E1.2"),subQ0]}),-1.0]])],"derivedFrom":subQ0})])],"isStart":false}),makeQuery(id+"F6.opExtrude","CAP_EDGE",EDGE,{"disambiguationData":[OSD([subQ0]),TDD([makeQuery(id+"F3.imprint","IMPRINT",EDGE,{"disambiguationData":[TD([[makeQuery(id+"F3.imprint","INTERSECT",VERTEX,{"derivedFrom":[sQuery(id+"F3.wireOp",EDGE,"E1.0"),subQ0]}),1.0]])],"derivedFrom":subQ0})])],"isStart":false}),makeQuery(id+"F3vxCluZQKjuGS6_1.opExtrude","CAP_EDGE",EDGE,{"disambiguationData":[OSD([sQuery(id+"FG7JfQnFfKm0W8e.wireOp",EDGE,"a4df6a7b-901c-458c-aeef-db07d71890a7.3"),sQuery(id+"FG7JfQnFfKm0W8e.wireOp",EDGE,"3a78ae17-f210-4514-9efc-eef556d70575.left")])],"isStart":true})]});}
            var Q1;
            {var subQ0=sQuery(id+"F3.wireOp",EDGE,"E1.0");Q1=makeQuery(id+"F3vxCluZQKjuGS6_1.boolean.opBoolean","MERGE",EDGE,{"derivedFrom":[makeQuery(id+"F6.opExtrude","CAP_EDGE",EDGE,{"disambiguationData":[OSD([subQ0]),TDD([makeQuery(id+"F3.imprint","IMPRINT",EDGE,{"disambiguationData":[TD([[makeQuery(id+"F3.imprint","INTERSECT",VERTEX,{"derivedFrom":[subQ0,sQuery(id+"F3.wireOp",EDGE,"E1.1")]}),-1.0]])],"derivedFrom":subQ0})])],"isStart":false}),makeQuery(id+"F6.opExtrude","CAP_EDGE",EDGE,{"disambiguationData":[OSD([subQ0]),TDD([makeQuery(id+"F3.imprint","IMPRINT",EDGE,{"disambiguationData":[TD([[makeQuery(id+"F3.imprint","INTERSECT",VERTEX,{"derivedFrom":[subQ0,sQuery(id+"F3.wireOp",EDGE,"E1.3")]}),1.0]])],"derivedFrom":subQ0})])],"isStart":false}),makeQuery(id+"F3vxCluZQKjuGS6_1.opExtrude","CAP_EDGE",EDGE,{"disambiguationData":[OSD([sQuery(id+"FG7JfQnFfKm0W8e.wireOp",EDGE,"a4df6a7b-901c-458c-aeef-db07d71890a7.0"),sQuery(id+"FG7JfQnFfKm0W8e.wireOp",EDGE,"28a57de8-ee20-4f04-b501-8f9bbeeccb0a.bottom")])],"isStart":true})]});}
            var Q2;
            Q2=makeQuery(id+"F4.opExtrude","SWEPT_EDGE",EDGE,{"disambiguationData":[OSD([sQuery(id+"F3.wireOp",EDGE,"E1.0"),sQuery(id+"F3.wireOp",EDGE,"E1.3")])]});
            var Q3;
            {var subQ0=sQuery(id+"F3.wireOp",EDGE,"E1.1");Q3=makeQuery(id+"F3vxCluZQKjuGS6_1.boolean.opBoolean","MERGE",EDGE,{"derivedFrom":[makeQuery(id+"F6.opExtrude","CAP_EDGE",EDGE,{"disambiguationData":[OSD([subQ0]),TDD([makeQuery(id+"F3.imprint","IMPRINT",EDGE,{"disambiguationData":[TD([[makeQuery(id+"F3.imprint","INTERSECT",VERTEX,{"derivedFrom":[subQ0,sQuery(id+"F3.wireOp",EDGE,"E1.2")]}),-1.0]])],"derivedFrom":subQ0})])],"isStart":false}),makeQuery(id+"F6.opExtrude","CAP_EDGE",EDGE,{"disambiguationData":[OSD([subQ0]),TDD([makeQuery(id+"F3.imprint","IMPRINT",EDGE,{"disambiguationData":[TD([[makeQuery(id+"F3.imprint","INTERSECT",VERTEX,{"derivedFrom":[sQuery(id+"F3.wireOp",EDGE,"E1.0"),subQ0]}),1.0]])],"derivedFrom":subQ0})])],"isStart":false}),makeQuery(id+"F3vxCluZQKjuGS6_1.opExtrude","CAP_EDGE",EDGE,{"disambiguationData":[OSD([sQuery(id+"FG7JfQnFfKm0W8e.wireOp",EDGE,"a4df6a7b-901c-458c-aeef-db07d71890a7.1"),sQuery(id+"FG7JfQnFfKm0W8e.wireOp",EDGE,"3a78ae17-f210-4514-9efc-eef556d70575.right")])],"isStart":true})]});}
            var Q4;
            Q4=makeQuery(id+"F4.opExtrude","SWEPT_EDGE",EDGE,{"disambiguationData":[OSD([sQuery(id+"F3.wireOp",EDGE,"E1.0"),sQuery(id+"F3.wireOp",EDGE,"E1.1")])]});
            var Q5;
            Q5=makeQuery(id+"F4.opExtrude","SWEPT_EDGE",EDGE,{"disambiguationData":[OSD([sQuery(id+"F3.wireOp",EDGE,"E1.1"),sQuery(id+"F3.wireOp",EDGE,"E1.2")])]});
            var Q6;
            Q6=makeQuery(id+"F4.opExtrude","SWEPT_EDGE",EDGE,{"disambiguationData":[OSD([sQuery(id+"F3.wireOp",EDGE,"E1.2"),sQuery(id+"F3.wireOp",EDGE,"E1.3")])]});
            var Q7;
            {var subQ0=sQuery(id+"F3.wireOp",EDGE,"E1.2");Q7=makeQuery(id+"F3vxCluZQKjuGS6_1.boolean.opBoolean","MERGE",EDGE,{"derivedFrom":[makeQuery(id+"F6.opExtrude","CAP_EDGE",EDGE,{"disambiguationData":[OSD([subQ0]),TDD([makeQuery(id+"F3.imprint","IMPRINT",EDGE,{"disambiguationData":[TD([[makeQuery(id+"F3.imprint","INTERSECT",VERTEX,{"derivedFrom":[sQuery(id+"F3.wireOp",EDGE,"E1.1"),subQ0]}),-1.0]])],"derivedFrom":subQ0})])],"isStart":false}),makeQuery(id+"F6.opExtrude","CAP_EDGE",EDGE,{"disambiguationData":[OSD([subQ0]),TDD([makeQuery(id+"F3.imprint","IMPRINT",EDGE,{"disambiguationData":[TD([[makeQuery(id+"F3.imprint","INTERSECT",VERTEX,{"derivedFrom":[subQ0,sQuery(id+"F3.wireOp",EDGE,"E1.3")]}),1.0]])],"derivedFrom":subQ0})])],"isStart":false}),makeQuery(id+"F3vxCluZQKjuGS6_1.opExtrude","CAP_EDGE",EDGE,{"disambiguationData":[OSD([sQuery(id+"FG7JfQnFfKm0W8e.wireOp",EDGE,"a4df6a7b-901c-458c-aeef-db07d71890a7.2"),sQuery(id+"FG7JfQnFfKm0W8e.wireOp",EDGE,"28a57de8-ee20-4f04-b501-8f9bbeeccb0a.top")])],"isStart":true})]});}
            var Q8;
            Q8=makeQuery(id+"F4.opExtrude","CAP_EDGE",EDGE,{"disambiguationData":[OSD([sQuery(id+"F3.wireOp",EDGE,"E1.2")])],"isStart":true});
            var Q9;
            Q9=makeQuery(id+"F4.opExtrude","CAP_EDGE",EDGE,{"disambiguationData":[OSD([sQuery(id+"F3.wireOp",EDGE,"E1.0")])],"isStart":true});
            var Q10;
            Q10=makeQuery(id+"F4.opExtrude","CAP_EDGE",EDGE,{"disambiguationData":[OSD([sQuery(id+"F3.wireOp",EDGE,"E1.1")])],"isStart":true});
            var Q11;
            Q11=makeQuery(id+"F4.opExtrude","CAP_EDGE",EDGE,{"disambiguationData":[OSD([sQuery(id+"F3.wireOp",EDGE,"E1.3")])],"isStart":true});
            chamfer(context, id + "F14", {"entities" : qUnion([Q0, Q1, Q2, Q3, Q4, Q5, Q6, Q7, Q8, Q9, Q10, Q11]), "width" : 4 * mm, "tangentPropagation" : true});
        }
        {
            var Q0;
            Q0=makeQuery(id+"F5.boolean.opBoolean","COPY",EDGE,{"derivedFrom":makeQuery(id+"F5.opExtrude","CAP_EDGE",EDGE,{"disambiguationData":[OSD([sQuery(id+"F3.wireOp",EDGE,"E0.left")])],"isStart":true})});
            var Q1;
            Q1=makeQuery(id+"F5.boolean.opBoolean","COPY",EDGE,{"derivedFrom":makeQuery(id+"F5.opExtrude","CAP_EDGE",EDGE,{"disambiguationData":[OSD([sQuery(id+"F3.wireOp",EDGE,"E0.bottom")])],"isStart":true})});
            var Q2;
            Q2=makeQuery(id+"F5.boolean.opBoolean","COPY",EDGE,{"derivedFrom":makeQuery(id+"F5.opExtrude","CAP_EDGE",EDGE,{"disambiguationData":[OSD([sQuery(id+"F3.wireOp",EDGE,"E0.top")])],"isStart":true})});
            var Q3;
            Q3=makeQuery(id+"F5.boolean.opBoolean","COPY",EDGE,{"derivedFrom":makeQuery(id+"F5.opExtrude","CAP_EDGE",EDGE,{"disambiguationData":[OSD([sQuery(id+"F3.wireOp",EDGE,"E0.right")])],"isStart":true})});
            var Q4;
            {var subQ0=sQuery(id+"F3.wireOp",EDGE,"E3.bottom");var subQ1=sQuery(id+"F3.wireOp",EDGE,"E2.left");var subQ2=sQuery(id+"F3.wireOp",EDGE,"E0.right");var subQ3=sQuery(id+"F3.wireOp",EDGE,"E0.top");Q4=makeQuery(id+"F12.boolean.opBoolean","SPLIT",EDGE,{"disambiguationData":[TD([makeQuery(id+"F12.opExtrude","CAP_FACE",FACE,{"disambiguationData":[OSD([subQ3,subQ2,subQ1,subQ0])],"isStart":true})])],"derivedFrom":makeQuery(id+"F5.boolean.opBoolean","COPY",EDGE,{"derivedFrom":makeQuery(id+"F5.opExtrude","SWEPT_EDGE",EDGE,{"disambiguationData":[OSD([subQ3,subQ2])]})})});}
            var Q5;
            {var subQ0=sQuery(id+"F3.wireOp",EDGE,"E3.bottom");var subQ1=sQuery(id+"F3.wireOp",EDGE,"E2.right");var subQ2=sQuery(id+"F3.wireOp",EDGE,"E0.left");var subQ3=sQuery(id+"F3.wireOp",EDGE,"E0.top");Q5=makeQuery(id+"F12.boolean.opBoolean","SPLIT",EDGE,{"disambiguationData":[TD([makeQuery(id+"F12.opExtrude","CAP_FACE",FACE,{"disambiguationData":[OSD([subQ3,subQ2,subQ1,subQ0])],"isStart":true})])],"derivedFrom":makeQuery(id+"F5.boolean.opBoolean","COPY",EDGE,{"derivedFrom":makeQuery(id+"F5.opExtrude","SWEPT_EDGE",EDGE,{"disambiguationData":[OSD([subQ3,subQ2])]})})});}
            var Q6;
            {var subQ0=sQuery(id+"F3.wireOp",EDGE,"E0.bottom");var subQ1=sQuery(id+"F3.wireOp",EDGE,"E3.top");var subQ2=sQuery(id+"F3.wireOp",EDGE,"E2.right");var subQ3=sQuery(id+"F3.wireOp",EDGE,"E0.left");Q6=makeQuery(id+"F12.boolean.opBoolean","SPLIT",EDGE,{"disambiguationData":[TD([makeQuery(id+"F12.opExtrude","CAP_FACE",FACE,{"disambiguationData":[OSD([subQ0,subQ3,subQ2,subQ1])],"isStart":true})])],"derivedFrom":makeQuery(id+"F5.boolean.opBoolean","COPY",EDGE,{"derivedFrom":makeQuery(id+"F5.opExtrude","SWEPT_EDGE",EDGE,{"disambiguationData":[OSD([subQ0,subQ3])]})})});}
            var Q7;
            {var subQ0=sQuery(id+"F3.wireOp",EDGE,"E0.bottom");var subQ1=sQuery(id+"F3.wireOp",EDGE,"E3.top");var subQ2=sQuery(id+"F3.wireOp",EDGE,"E2.left");var subQ3=sQuery(id+"F3.wireOp",EDGE,"E0.right");Q7=makeQuery(id+"F12.boolean.opBoolean","SPLIT",EDGE,{"disambiguationData":[TD([makeQuery(id+"F12.opExtrude","CAP_FACE",FACE,{"disambiguationData":[OSD([subQ0,subQ3,subQ2,subQ1])],"isStart":true})])],"derivedFrom":makeQuery(id+"F5.boolean.opBoolean","COPY",EDGE,{"derivedFrom":makeQuery(id+"F5.opExtrude","SWEPT_EDGE",EDGE,{"disambiguationData":[OSD([subQ0,subQ3])]})})});}
            var Q8;
            {var subQ0=sQuery(id+"F3.wireOp",EDGE,"E3.bottom");var subQ1=sQuery(id+"F3.wireOp",EDGE,"E2.right");var subQ2=sQuery(id+"F3.wireOp",EDGE,"E0.top");var subQ3=sQuery(id+"F3.wireOp",EDGE,"E0.left");Q8=makeQuery(id+"F12.boolean.opBoolean","SPLIT",EDGE,{"disambiguationData":[TD([makeQuery(id+"F12.opExtrude","CAP_FACE",FACE,{"disambiguationData":[OSD([subQ2,subQ3,subQ1,subQ0])],"isStart":false})])],"derivedFrom":makeQuery(id+"F5.boolean.opBoolean","COPY",EDGE,{"derivedFrom":makeQuery(id+"F5.opExtrude","SWEPT_EDGE",EDGE,{"disambiguationData":[OSD([subQ2,subQ3])]})})});}
            var Q9;
            {var subQ0=sQuery(id+"F3.wireOp",EDGE,"E3.bottom");var subQ1=sQuery(id+"F3.wireOp",EDGE,"E2.left");var subQ2=sQuery(id+"F3.wireOp",EDGE,"E0.top");var subQ3=sQuery(id+"F3.wireOp",EDGE,"E0.right");Q9=makeQuery(id+"F12.boolean.opBoolean","SPLIT",EDGE,{"disambiguationData":[TD([makeQuery(id+"F12.opExtrude","CAP_FACE",FACE,{"disambiguationData":[OSD([subQ2,subQ3,subQ1,subQ0])],"isStart":false})])],"derivedFrom":makeQuery(id+"F5.boolean.opBoolean","COPY",EDGE,{"derivedFrom":makeQuery(id+"F5.opExtrude","SWEPT_EDGE",EDGE,{"disambiguationData":[OSD([subQ2,subQ3])]})})});}
            chamfer(context, id + "F15", {"entities" : qUnion([Q0, Q1, Q2, Q3, Q4, Q5, Q6, Q7, Q8, Q9]), "width" : 3 * mm, "tangentPropagation" : true});
        }
        {
            var Q0;
            {var subQ0=sQuery(id+"F3.wireOp",EDGE,"E3.top");var subQ1=sQuery(id+"F3.wireOp",EDGE,"E2.right");var subQ2=sQuery(id+"F3.wireOp",EDGE,"E0.bottom");var subQ3=sQuery(id+"F3.wireOp",EDGE,"E0.left");Q0=makeQuery(id+"F12.boolean.opBoolean","SPLIT",EDGE,{"disambiguationData":[TD([makeQuery(id+"F12.opExtrude","CAP_FACE",FACE,{"disambiguationData":[OSD([subQ2,subQ3,subQ1,subQ0])],"isStart":false})])],"derivedFrom":makeQuery(id+"F5.boolean.opBoolean","COPY",EDGE,{"derivedFrom":makeQuery(id+"F5.opExtrude","SWEPT_EDGE",EDGE,{"disambiguationData":[OSD([subQ2,subQ3])]})})});}
            var Q1;
            {var subQ0=sQuery(id+"F3.wireOp",EDGE,"E3.top");var subQ1=sQuery(id+"F3.wireOp",EDGE,"E2.left");var subQ2=sQuery(id+"F3.wireOp",EDGE,"E0.bottom");var subQ3=sQuery(id+"F3.wireOp",EDGE,"E0.right");Q1=makeQuery(id+"F12.boolean.opBoolean","SPLIT",EDGE,{"disambiguationData":[TD([makeQuery(id+"F12.opExtrude","CAP_FACE",FACE,{"disambiguationData":[OSD([subQ2,subQ3,subQ1,subQ0])],"isStart":false})])],"derivedFrom":makeQuery(id+"F5.boolean.opBoolean","COPY",EDGE,{"derivedFrom":makeQuery(id+"F5.opExtrude","SWEPT_EDGE",EDGE,{"disambiguationData":[OSD([subQ2,subQ3])]})})});}
            fillet(context, id + "F16", {"entities" : qUnion([Q0, Q1]), "radius" : 3 * mm, "tangentPropagation" : true, "allowEdgeOverflow" : false});
        }
        {
            var Q0;
            Q0=qCreatedBy(makeId("Top.planeOp"),FACE);
            var sketch = newSketch(context, id + "F17", { "sketchPlane" : qUnion([Q0])});
            skLineSegment(sketch, "E137", {"start": v(0, 0) * mm, "end": v(-240, 0) * mm, "construction": true});
            skLineSegment(sketch, "E138.bottom", {"start": v(-272.8, 32.8) * mm, "end": v(-207.2, 32.8) * mm});
            skLineSegment(sketch, "E138.top", {"start": v(-272.8, -32.8) * mm, "end": v(-207.2, -32.8) * mm});
            skLineSegment(sketch, "E138.left", {"start": v(-272.8, 32.8) * mm, "end": v(-272.8, -32.8) * mm});
            skLineSegment(sketch, "E138.right", {"start": v(-207.2, 32.8) * mm, "end": v(-207.2, -32.8) * mm});
            skPoint(sketch, "E138.middle", {"position": v(-240, 0) * mm});
            skSolve(sketch);
        }
        {
            var Q0;
            Q0 = qSketchRegion(id + "F17", true);
            extrude(context, id + "F18", {"entities" : qUnion([Q0]), "oppositeDirection" : true, "depth" : (getVariable(context, 'Grosor')) * mm});
        }
        {
            var Q0;
            Q0=qCreatedBy(makeId("Top.planeOp"),FACE);
            var sketch = newSketch(context, id + "F19", { "sketchPlane" : qUnion([Q0])});
            skLineSegment(sketch, "E139", {"start": v(0, 0) * mm, "end": v(-240, 0) * mm, "construction": true});
            skLineSegment(sketch, "E140.bottom", {"start": v(-269.75, 29.75) * mm, "end": v(-210.25, 29.75) * mm});
            skLineSegment(sketch, "E140.top", {"start": v(-269.75, -29.75) * mm, "end": v(-210.25, -29.75) * mm});
            skLineSegment(sketch, "E140.left", {"start": v(-269.75, 29.75) * mm, "end": v(-269.75, -29.75) * mm});
            skLineSegment(sketch, "E140.right", {"start": v(-210.25, 29.75) * mm, "end": v(-210.25, -29.75) * mm});
            skPoint(sketch, "E140.middle", {"position": v(-240, 0) * mm});
            skLineSegment(sketch, "E141.bottom", {"start": v(-267.2, 27.2) * mm, "end": v(-212.8, 27.2) * mm});
            skLineSegment(sketch, "E141.top", {"start": v(-267.2, -27.2) * mm, "end": v(-212.8, -27.2) * mm});
            skLineSegment(sketch, "E141.left", {"start": v(-267.2, 27.2) * mm, "end": v(-267.2, -27.2) * mm});
            skLineSegment(sketch, "E141.right", {"start": v(-212.8, 27.2) * mm, "end": v(-212.8, -27.2) * mm});
            skSolve(sketch);
        }
        {
            var Q0;
            Q0 = qSketchRegion(id + "F19", true);
            extrude(context, id + "F20", {"entities" : qUnion([Q0]), "operationType" : NewBodyOperationType.ADD, "depth" : (getVariable(context, 'Grosor') + 1) * mm});
        }
        {
            var Q0;
            Q0=makeQuery(id+"F18.opExtrude","CAP_FACE",FACE,{"disambiguationData":[OSD([sQuery(id+"F17.wireOp",EDGE,"E138.bottom"),sQuery(id+"F17.wireOp",EDGE,"E138.top"),sQuery(id+"F17.wireOp",EDGE,"E138.left"),sQuery(id+"F17.wireOp",EDGE,"E138.right")])],"isStart":false});
            var Q1;
            Q1=makeQuery(id+"F18.opExtrude","SWEPT_EDGE",EDGE,{"disambiguationData":[OSD([sQuery(id+"F17.wireOp",EDGE,"E138.bottom"),sQuery(id+"F17.wireOp",EDGE,"E138.left")])]});
            var Q2;
            Q2=makeQuery(id+"F18.opExtrude","SWEPT_EDGE",EDGE,{"disambiguationData":[OSD([sQuery(id+"F17.wireOp",EDGE,"E138.bottom"),sQuery(id+"F17.wireOp",EDGE,"E138.right")])]});
            var Q3;
            Q3=makeQuery(id+"F18.opExtrude","SWEPT_EDGE",EDGE,{"disambiguationData":[OSD([sQuery(id+"F17.wireOp",EDGE,"E138.top"),sQuery(id+"F17.wireOp",EDGE,"E138.right")])]});
            var Q4;
            Q4=makeQuery(id+"F18.opExtrude","SWEPT_EDGE",EDGE,{"disambiguationData":[OSD([sQuery(id+"F17.wireOp",EDGE,"E138.top"),sQuery(id+"F17.wireOp",EDGE,"E138.left")])]});
            chamfer(context, id + "F21", {"entities" : qUnion([Q0, Q1, Q2, Q3, Q4]), "width" : 2.8 * mm, "tangentPropagation" : true});
        }
        {
            var Q0;
            Q0=makeQuery(id+"F20.opExtrude","SWEPT_EDGE",EDGE,{"disambiguationData":[OSD([sQuery(id+"F19.wireOp",EDGE,"E140.bottom"),sQuery(id+"F19.wireOp",EDGE,"E140.left")])]});
            var Q1;
            Q1=makeQuery(id+"F20.opExtrude","SWEPT_EDGE",EDGE,{"disambiguationData":[OSD([sQuery(id+"F19.wireOp",EDGE,"E141.bottom"),sQuery(id+"F19.wireOp",EDGE,"E141.left")])]});
            var Q2;
            Q2=makeQuery(id+"F20.opExtrude","SWEPT_EDGE",EDGE,{"disambiguationData":[OSD([sQuery(id+"F19.wireOp",EDGE,"E141.bottom"),sQuery(id+"F19.wireOp",EDGE,"E141.right")])]});
            var Q3;
            Q3=makeQuery(id+"F20.opExtrude","SWEPT_EDGE",EDGE,{"disambiguationData":[OSD([sQuery(id+"F19.wireOp",EDGE,"E140.bottom"),sQuery(id+"F19.wireOp",EDGE,"E140.right")])]});
            chamfer(context, id + "F22", {"entities" : qUnion([Q0, Q1, Q2, Q3]), "width" : 3 * mm, "tangentPropagation" : true});
        }
        {
            var Q0;
            Q0=makeQuery(id+"F20.opExtrude","SWEPT_EDGE",EDGE,{"disambiguationData":[OSD([sQuery(id+"F19.wireOp",EDGE,"E140.top"),sQuery(id+"F19.wireOp",EDGE,"E140.right")])]});
            var Q1;
            Q1=makeQuery(id+"F20.opExtrude","SWEPT_EDGE",EDGE,{"disambiguationData":[OSD([sQuery(id+"F19.wireOp",EDGE,"E140.top"),sQuery(id+"F19.wireOp",EDGE,"E140.left")])]});
            var Q2;
            Q2=makeQuery(id+"F20.opExtrude","SWEPT_EDGE",EDGE,{"disambiguationData":[OSD([sQuery(id+"F19.wireOp",EDGE,"E141.top"),sQuery(id+"F19.wireOp",EDGE,"E141.left")])]});
            var Q3;
            Q3=makeQuery(id+"F20.opExtrude","SWEPT_EDGE",EDGE,{"disambiguationData":[OSD([sQuery(id+"F19.wireOp",EDGE,"E141.top"),sQuery(id+"F19.wireOp",EDGE,"E141.right")])]});
            fillet(context, id + "F23", {"entities" : qUnion([Q0, Q1, Q2, Q3]), "radius" : 3 * mm, "tangentPropagation" : true, "allowEdgeOverflow" : false});
        }
        {
            var Q0;
            Q0=qCreatedBy(makeId("Top.planeOp"),FACE);
            var sketch = newSketch(context, id + "F24", { "sketchPlane" : qUnion([Q0])});
            skLineSegment(sketch, "E142", {"start": v(0, 0) * mm, "end": v(-240, 0) * mm, "construction": true});
            skLineSegment(sketch, "E143", {"start": v(-240, 0) * mm, "end": v(-240, -11.75) * mm, "construction": true});
            skLineSegment(sketch, "E144", {"start": v(-240, -11.75) * mm, "end": v(-251.75, -11.75) * mm, "construction": true});
            skLineSegment(sketch, "E145.bottom", {"start": v(-254.25, -4.25) * mm, "end": v(-249.25, -4.25) * mm});
            skLineSegment(sketch, "E145.top", {"start": v(-254.25, -19.25) * mm, "end": v(-249.25, -19.25) * mm});
            skLineSegment(sketch, "E145.left", {"start": v(-259.25, -9.25) * mm, "end": v(-259.25, -14.25) * mm});
            skLineSegment(sketch, "E145.right", {"start": v(-244.25, -9.25) * mm, "end": v(-244.25, -14.25) * mm});
            skPoint(sketch, "E145.middle", {"position": v(-251.75, -11.75) * mm});
            skPoint(sketch, "E146.visualSharp", {"position": v(-259.25, -4.25) * mm});
            skArc(sketch, "E146.filletArc", {"start": v(-254.25, -4.25) * mm, "mid": v(-257.79, -5.71) * mm, "end": v(-259.25, -9.25) * mm});
            skPoint(sketch, "E147.visualSharp", {"position": v(-244.25, -4.25) * mm});
            skArc(sketch, "E147.filletArc", {"start": v(-244.25, -9.25) * mm, "mid": v(-245.71, -5.71) * mm, "end": v(-249.25, -4.25) * mm});
            skPoint(sketch, "E148.visualSharp", {"position": v(-244.25, -19.25) * mm});
            skArc(sketch, "E148.filletArc", {"start": v(-249.25, -19.25) * mm, "mid": v(-245.71, -17.79) * mm, "end": v(-244.25, -14.25) * mm});
            skPoint(sketch, "E149.visualSharp", {"position": v(-259.25, -19.25) * mm});
            skArc(sketch, "E149.filletArc", {"start": v(-259.25, -14.25) * mm, "mid": v(-257.79, -17.79) * mm, "end": v(-254.25, -19.25) * mm});
            skArc(sketch, "E150.0.1.0", {"start": v(-254.25, 19.25) * mm, "mid": v(-257.79, 17.79) * mm, "end": v(-259.25, 14.25) * mm});
            skPoint(sketch, "E150.0.1.1", {"position": v(-244.25, 4.25) * mm});
            skPoint(sketch, "E150.0.1.2", {"position": v(-244.25, 19.25) * mm});
            skArc(sketch, "E150.0.1.3", {"start": v(-249.25, 4.25) * mm, "mid": v(-245.71, 5.71) * mm, "end": v(-244.25, 9.25) * mm});
            skArc(sketch, "E150.0.1.4", {"start": v(-244.25, 14.25) * mm, "mid": v(-245.71, 17.79) * mm, "end": v(-249.25, 19.25) * mm});
            skPoint(sketch, "E150.0.1.5", {"position": v(-251.75, 11.75) * mm});
            skPoint(sketch, "E150.0.1.6", {"position": v(-259.25, 19.25) * mm});
            skLineSegment(sketch, "E150.0.1.7", {"start": v(-259.25, 14.25) * mm, "end": v(-259.25, 9.25) * mm});
            skArc(sketch, "E150.0.1.8", {"start": v(-259.25, 9.25) * mm, "mid": v(-257.79, 5.71) * mm, "end": v(-254.25, 4.25) * mm});
            skPoint(sketch, "E150.0.1.9", {"position": v(-259.25, 4.25) * mm});
            skLineSegment(sketch, "E150.0.1.10", {"start": v(-244.25, 14.25) * mm, "end": v(-244.25, 9.25) * mm});
            skLineSegment(sketch, "E150.0.1.11", {"start": v(-254.25, 19.25) * mm, "end": v(-249.25, 19.25) * mm});
            skLineSegment(sketch, "E150.0.1.12", {"start": v(-254.25, 4.25) * mm, "end": v(-249.25, 4.25) * mm});
            skArc(sketch, "E150.0.2.0", {"start": v(-254.25, 42.75) * mm, "mid": v(-257.79, 41.29) * mm, "end": v(-259.25, 37.75) * mm});
            skPoint(sketch, "E150.0.2.1", {"position": v(-244.25, 27.75) * mm});
            skPoint(sketch, "E150.0.2.2", {"position": v(-244.25, 42.75) * mm});
            skArc(sketch, "E150.0.2.3", {"start": v(-249.25, 27.75) * mm, "mid": v(-245.71, 29.21) * mm, "end": v(-244.25, 32.75) * mm});
            skArc(sketch, "E150.0.2.4", {"start": v(-244.25, 37.75) * mm, "mid": v(-245.71, 41.29) * mm, "end": v(-249.25, 42.75) * mm});
            skPoint(sketch, "E150.0.2.5", {"position": v(-251.75, 35.25) * mm});
            skPoint(sketch, "E150.0.2.6", {"position": v(-259.25, 42.75) * mm});
            skLineSegment(sketch, "E150.0.2.7", {"start": v(-259.25, 37.75) * mm, "end": v(-259.25, 32.75) * mm});
            skArc(sketch, "E150.0.2.8", {"start": v(-259.25, 32.75) * mm, "mid": v(-257.79, 29.21) * mm, "end": v(-254.25, 27.75) * mm});
            skPoint(sketch, "E150.0.2.9", {"position": v(-259.25, 27.75) * mm});
            skLineSegment(sketch, "E150.0.2.10", {"start": v(-244.25, 37.75) * mm, "end": v(-244.25, 32.75) * mm});
            skLineSegment(sketch, "E150.0.2.11", {"start": v(-254.25, 42.75) * mm, "end": v(-249.25, 42.75) * mm});
            skLineSegment(sketch, "E150.0.2.12", {"start": v(-254.25, 27.75) * mm, "end": v(-249.25, 27.75) * mm});
            skArc(sketch, "E150.1.0.0", {"start": v(-230.75, -4.25) * mm, "mid": v(-234.29, -5.71) * mm, "end": v(-235.75, -9.25) * mm});
            skPoint(sketch, "E150.1.0.1", {"position": v(-220.75, -19.25) * mm});
            skPoint(sketch, "E150.1.0.2", {"position": v(-220.75, -4.25) * mm});
            skArc(sketch, "E150.1.0.3", {"start": v(-225.75, -19.25) * mm, "mid": v(-222.21, -17.79) * mm, "end": v(-220.75, -14.25) * mm});
            skArc(sketch, "E150.1.0.4", {"start": v(-220.75, -9.25) * mm, "mid": v(-222.21, -5.71) * mm, "end": v(-225.75, -4.25) * mm});
            skPoint(sketch, "E150.1.0.5", {"position": v(-228.25, -11.75) * mm});
            skPoint(sketch, "E150.1.0.6", {"position": v(-235.75, -4.25) * mm});
            skLineSegment(sketch, "E150.1.0.7", {"start": v(-235.75, -9.25) * mm, "end": v(-235.75, -14.25) * mm});
            skArc(sketch, "E150.1.0.8", {"start": v(-235.75, -14.25) * mm, "mid": v(-234.29, -17.79) * mm, "end": v(-230.75, -19.25) * mm});
            skPoint(sketch, "E150.1.0.9", {"position": v(-235.75, -19.25) * mm});
            skLineSegment(sketch, "E150.1.0.10", {"start": v(-220.75, -9.25) * mm, "end": v(-220.75, -14.25) * mm});
            skLineSegment(sketch, "E150.1.0.11", {"start": v(-230.75, -4.25) * mm, "end": v(-225.75, -4.25) * mm});
            skLineSegment(sketch, "E150.1.0.12", {"start": v(-230.75, -19.25) * mm, "end": v(-225.75, -19.25) * mm});
            skArc(sketch, "E150.1.1.0", {"start": v(-230.75, 19.25) * mm, "mid": v(-234.29, 17.79) * mm, "end": v(-235.75, 14.25) * mm});
            skPoint(sketch, "E150.1.1.1", {"position": v(-220.75, 4.25) * mm});
            skPoint(sketch, "E150.1.1.2", {"position": v(-220.75, 19.25) * mm});
            skArc(sketch, "E150.1.1.3", {"start": v(-225.75, 4.25) * mm, "mid": v(-222.21, 5.71) * mm, "end": v(-220.75, 9.25) * mm});
            skArc(sketch, "E150.1.1.4", {"start": v(-220.75, 14.25) * mm, "mid": v(-222.21, 17.79) * mm, "end": v(-225.75, 19.25) * mm});
            skPoint(sketch, "E150.1.1.5", {"position": v(-228.25, 11.75) * mm});
            skPoint(sketch, "E150.1.1.6", {"position": v(-235.75, 19.25) * mm});
            skLineSegment(sketch, "E150.1.1.7", {"start": v(-235.75, 14.25) * mm, "end": v(-235.75, 9.25) * mm});
            skArc(sketch, "E150.1.1.8", {"start": v(-235.75, 9.25) * mm, "mid": v(-234.29, 5.71) * mm, "end": v(-230.75, 4.25) * mm});
            skPoint(sketch, "E150.1.1.9", {"position": v(-235.75, 4.25) * mm});
            skLineSegment(sketch, "E150.1.1.10", {"start": v(-220.75, 14.25) * mm, "end": v(-220.75, 9.25) * mm});
            skLineSegment(sketch, "E150.1.1.11", {"start": v(-230.75, 19.25) * mm, "end": v(-225.75, 19.25) * mm});
            skLineSegment(sketch, "E150.1.1.12", {"start": v(-230.75, 4.25) * mm, "end": v(-225.75, 4.25) * mm});
            skArc(sketch, "E150.1.2.0", {"start": v(-230.75, 42.75) * mm, "mid": v(-234.29, 41.29) * mm, "end": v(-235.75, 37.75) * mm});
            skPoint(sketch, "E150.1.2.1", {"position": v(-220.75, 27.75) * mm});
            skPoint(sketch, "E150.1.2.2", {"position": v(-220.75, 42.75) * mm});
            skArc(sketch, "E150.1.2.3", {"start": v(-225.75, 27.75) * mm, "mid": v(-222.21, 29.21) * mm, "end": v(-220.75, 32.75) * mm});
            skArc(sketch, "E150.1.2.4", {"start": v(-220.75, 37.75) * mm, "mid": v(-222.21, 41.29) * mm, "end": v(-225.75, 42.75) * mm});
            skPoint(sketch, "E150.1.2.5", {"position": v(-228.25, 35.25) * mm});
            skPoint(sketch, "E150.1.2.6", {"position": v(-235.75, 42.75) * mm});
            skLineSegment(sketch, "E150.1.2.7", {"start": v(-235.75, 37.75) * mm, "end": v(-235.75, 32.75) * mm});
            skArc(sketch, "E150.1.2.8", {"start": v(-235.75, 32.75) * mm, "mid": v(-234.29, 29.21) * mm, "end": v(-230.75, 27.75) * mm});
            skPoint(sketch, "E150.1.2.9", {"position": v(-235.75, 27.75) * mm});
            skLineSegment(sketch, "E150.1.2.10", {"start": v(-220.75, 37.75) * mm, "end": v(-220.75, 32.75) * mm});
            skLineSegment(sketch, "E150.1.2.11", {"start": v(-230.75, 42.75) * mm, "end": v(-225.75, 42.75) * mm});
            skLineSegment(sketch, "E150.1.2.12", {"start": v(-230.75, 27.75) * mm, "end": v(-225.75, 27.75) * mm});
            skArc(sketch, "E150.2.0.0", {"start": v(-207.25, -4.25) * mm, "mid": v(-210.79, -5.71) * mm, "end": v(-212.25, -9.25) * mm});
            skPoint(sketch, "E150.2.0.1", {"position": v(-197.25, -19.25) * mm});
            skPoint(sketch, "E150.2.0.2", {"position": v(-197.25, -4.25) * mm});
            skArc(sketch, "E150.2.0.3", {"start": v(-202.25, -19.25) * mm, "mid": v(-198.71, -17.79) * mm, "end": v(-197.25, -14.25) * mm});
            skArc(sketch, "E150.2.0.4", {"start": v(-197.25, -9.25) * mm, "mid": v(-198.71, -5.71) * mm, "end": v(-202.25, -4.25) * mm});
            skPoint(sketch, "E150.2.0.5", {"position": v(-204.75, -11.75) * mm});
            skPoint(sketch, "E150.2.0.6", {"position": v(-212.25, -4.25) * mm});
            skLineSegment(sketch, "E150.2.0.7", {"start": v(-212.25, -9.25) * mm, "end": v(-212.25, -14.25) * mm});
            skArc(sketch, "E150.2.0.8", {"start": v(-212.25, -14.25) * mm, "mid": v(-210.79, -17.79) * mm, "end": v(-207.25, -19.25) * mm});
            skPoint(sketch, "E150.2.0.9", {"position": v(-212.25, -19.25) * mm});
            skLineSegment(sketch, "E150.2.0.10", {"start": v(-197.25, -9.25) * mm, "end": v(-197.25, -14.25) * mm});
            skLineSegment(sketch, "E150.2.0.11", {"start": v(-207.25, -4.25) * mm, "end": v(-202.25, -4.25) * mm});
            skLineSegment(sketch, "E150.2.0.12", {"start": v(-207.25, -19.25) * mm, "end": v(-202.25, -19.25) * mm});
            skArc(sketch, "E150.2.1.0", {"start": v(-207.25, 19.25) * mm, "mid": v(-210.79, 17.79) * mm, "end": v(-212.25, 14.25) * mm});
            skPoint(sketch, "E150.2.1.1", {"position": v(-197.25, 4.25) * mm});
            skPoint(sketch, "E150.2.1.2", {"position": v(-197.25, 19.25) * mm});
            skArc(sketch, "E150.2.1.3", {"start": v(-202.25, 4.25) * mm, "mid": v(-198.71, 5.71) * mm, "end": v(-197.25, 9.25) * mm});
            skArc(sketch, "E150.2.1.4", {"start": v(-197.25, 14.25) * mm, "mid": v(-198.71, 17.79) * mm, "end": v(-202.25, 19.25) * mm});
            skPoint(sketch, "E150.2.1.5", {"position": v(-204.75, 11.75) * mm});
            skPoint(sketch, "E150.2.1.6", {"position": v(-212.25, 19.25) * mm});
            skLineSegment(sketch, "E150.2.1.7", {"start": v(-212.25, 14.25) * mm, "end": v(-212.25, 9.25) * mm});
            skArc(sketch, "E150.2.1.8", {"start": v(-212.25, 9.25) * mm, "mid": v(-210.79, 5.71) * mm, "end": v(-207.25, 4.25) * mm});
            skPoint(sketch, "E150.2.1.9", {"position": v(-212.25, 4.25) * mm});
            skLineSegment(sketch, "E150.2.1.10", {"start": v(-197.25, 14.25) * mm, "end": v(-197.25, 9.25) * mm});
            skLineSegment(sketch, "E150.2.1.11", {"start": v(-207.25, 19.25) * mm, "end": v(-202.25, 19.25) * mm});
            skLineSegment(sketch, "E150.2.1.12", {"start": v(-207.25, 4.25) * mm, "end": v(-202.25, 4.25) * mm});
            skArc(sketch, "E150.2.2.0", {"start": v(-207.25, 42.75) * mm, "mid": v(-210.79, 41.29) * mm, "end": v(-212.25, 37.75) * mm});
            skPoint(sketch, "E150.2.2.1", {"position": v(-197.25, 27.75) * mm});
            skPoint(sketch, "E150.2.2.2", {"position": v(-197.25, 42.75) * mm});
            skArc(sketch, "E150.2.2.3", {"start": v(-202.25, 27.75) * mm, "mid": v(-198.71, 29.21) * mm, "end": v(-197.25, 32.75) * mm});
            skArc(sketch, "E150.2.2.4", {"start": v(-197.25, 37.75) * mm, "mid": v(-198.71, 41.29) * mm, "end": v(-202.25, 42.75) * mm});
            skPoint(sketch, "E150.2.2.5", {"position": v(-204.75, 35.25) * mm});
            skPoint(sketch, "E150.2.2.6", {"position": v(-212.25, 42.75) * mm});
            skLineSegment(sketch, "E150.2.2.7", {"start": v(-212.25, 37.75) * mm, "end": v(-212.25, 32.75) * mm});
            skArc(sketch, "E150.2.2.8", {"start": v(-212.25, 32.75) * mm, "mid": v(-210.79, 29.21) * mm, "end": v(-207.25, 27.75) * mm});
            skPoint(sketch, "E150.2.2.9", {"position": v(-212.25, 27.75) * mm});
            skLineSegment(sketch, "E150.2.2.10", {"start": v(-197.25, 37.75) * mm, "end": v(-197.25, 32.75) * mm});
            skLineSegment(sketch, "E150.2.2.11", {"start": v(-207.25, 42.75) * mm, "end": v(-202.25, 42.75) * mm});
            skLineSegment(sketch, "E150.2.2.12", {"start": v(-207.25, 27.75) * mm, "end": v(-202.25, 27.75) * mm});
            skLineSegment(sketch, "E150.direction1", {"start": v(-259.25, -19.25) * mm, "end": v(-235.75, -19.25) * mm, "construction": true});
            skLineSegment(sketch, "E150.direction2", {"start": v(-259.25, -19.25) * mm, "end": v(-259.25, 4.25) * mm, "construction": true});
            skSolve(sketch);
        }
        {
            var Q0;
            Q0=makeQuery(id+"F24.imprint","IMPRINT",FACE,{"disambiguationData":[TD([[makeQuery(id+"F24.imprint","IMPRINT",EDGE,{"derivedFrom":sQuery(id+"F24.wireOp",EDGE,"E150.0.1.0")}),1.0]])]});
            var Q1;
            Q1=makeQuery(id+"F24.imprint","IMPRINT",FACE,{"disambiguationData":[TD([[makeQuery(id+"F24.imprint","IMPRINT",EDGE,{"derivedFrom":sQuery(id+"F24.wireOp",EDGE,"E150.1.1.0")}),1.0]])]});
            var Q2;
            Q2=makeQuery(id+"F24.imprint","IMPRINT",FACE,{"disambiguationData":[TD([[makeQuery(id+"F24.imprint","IMPRINT",EDGE,{"derivedFrom":sQuery(id+"F24.wireOp",EDGE,"E150.1.0.0")}),1.0]])]});
            var Q3;
            Q3=makeQuery(id+"F24.imprint","IMPRINT",FACE,{"disambiguationData":[TD([[makeQuery(id+"F24.imprint","IMPRINT",EDGE,{"derivedFrom":sQuery(id+"F24.wireOp",EDGE,"E145.bottom")}),-1.0]])]});
            extrude(context, id + "F25", {"entities" : qUnion([Q0, Q1, Q2, Q3]), "operationType" : NewBodyOperationType.REMOVE, "endBound" : BoundingType.THROUGH_ALL, "oppositeDirection" : true, "depth" : 25 * mm});
        }
        {
            var Q0;
            Q0=qCreatedBy(makeId("Top.planeOp"),FACE);
            var sketch = newSketch(context, id + "F26", { "sketchPlane" : qUnion([Q0])});
            skLineSegment(sketch, "E151", {"start": v(0, 0) * mm, "end": v(120, 0) * mm, "construction": true});
            skLineSegment(sketch, "E152.bottom", {"start": v(90.5, -29.5) * mm, "end": v(149.5, -29.5) * mm});
            skLineSegment(sketch, "E152.top", {"start": v(90.5, 29.5) * mm, "end": v(149.5, 29.5) * mm});
            skLineSegment(sketch, "E152.left", {"start": v(90.5, -29.5) * mm, "end": v(90.5, 29.5) * mm});
            skLineSegment(sketch, "E152.right", {"start": v(149.5, -29.5) * mm, "end": v(149.5, 29.5) * mm});
            skSolve(sketch);
        }
        {
            var Q0;
            Q0=qSketchRegion(id+"F26",true);
            extrude(context, id + "F27", {"entities" : qUnion([Q0]), "oppositeDirection" : true, "depth" : (getVariable(context, 'Grosor')) * mm, "hasSecondDirection" : true, "secondDirectionOppositeDirection" : false, "secondDirectionDepth" : 3.5 * mm});
        }
        {
            var Q0;
            Q0=qCreatedBy(makeId("Top.planeOp"),FACE);
            var sketch = newSketch(context, id + "F28", { "sketchPlane" : qUnion([Q0])});
            skLineSegment(sketch, "E153", {"start": v(0, 0) * mm, "end": v(120, 0) * mm, "construction": true});
            skLineSegment(sketch, "E154.bottom", {"start": v(149.75, -29.75) * mm, "end": v(90.25, -29.75) * mm});
            skLineSegment(sketch, "E154.top", {"start": v(149.75, 29.75) * mm, "end": v(90.25, 29.75) * mm});
            skLineSegment(sketch, "E154.left", {"start": v(149.75, -29.75) * mm, "end": v(149.75, 29.75) * mm});
            skLineSegment(sketch, "E154.right", {"start": v(90.25, -29.75) * mm, "end": v(90.25, 29.75) * mm});
            skPoint(sketch, "E154.middle", {"position": v(120, 0) * mm});
            skLineSegment(sketch, "E155", {"start": v(120, 0) * mm, "end": v(120, -11.75) * mm, "construction": true});
            skLineSegment(sketch, "E156", {"start": v(120, -11.75) * mm, "end": v(96.5, -11.75) * mm, "construction": true});
            skLineSegment(sketch, "E157", {"start": v(108.25, -11.75) * mm, "end": v(108.25, -23.5) * mm, "construction": true});
            skLineSegment(sketch, "E158.bottom", {"start": v(106.75, -25) * mm, "end": v(109.75, -25) * mm});
            skLineSegment(sketch, "E158.top", {"start": v(106.75, -22) * mm, "end": v(109.75, -22) * mm});
            skLineSegment(sketch, "E158.left", {"start": v(106.75, -25) * mm, "end": v(106.75, -22) * mm});
            skLineSegment(sketch, "E158.right", {"start": v(109.75, -25) * mm, "end": v(109.75, -22) * mm});
            skPoint(sketch, "E158.middle", {"position": v(108.25, -23.5) * mm});
            skLineSegment(sketch, "E159.bottom", {"start": v(95, -13.25) * mm, "end": v(98, -13.25) * mm});
            skLineSegment(sketch, "E159.top", {"start": v(95, -10.25) * mm, "end": v(98, -10.25) * mm});
            skLineSegment(sketch, "E159.left", {"start": v(95, -13.25) * mm, "end": v(95, -10.25) * mm});
            skLineSegment(sketch, "E159.right", {"start": v(98, -13.25) * mm, "end": v(98, -10.25) * mm});
            skPoint(sketch, "E159.middle", {"position": v(96.5, -11.75) * mm});
            skLineSegment(sketch, "E160.0.1.0", {"start": v(109.75, -1.5) * mm, "end": v(109.75, 1.5) * mm});
            skLineSegment(sketch, "E160.0.1.1", {"start": v(108.25, 11.75) * mm, "end": v(108.25, 0) * mm, "construction": true});
            skLineSegment(sketch, "E160.0.1.2", {"start": v(106.75, -1.5) * mm, "end": v(109.75, -1.5) * mm});
            skLineSegment(sketch, "E160.0.1.3", {"start": v(106.75, 1.5) * mm, "end": v(109.75, 1.5) * mm});
            skLineSegment(sketch, "E160.0.1.4", {"start": v(95, 13.25) * mm, "end": v(98, 13.25) * mm});
            skPoint(sketch, "E160.0.1.5", {"position": v(96.5, 11.75) * mm});
            skPoint(sketch, "E160.0.1.6", {"position": v(108.25, 0) * mm});
            skLineSegment(sketch, "E160.0.1.7", {"start": v(95, 10.25) * mm, "end": v(98, 10.25) * mm});
            skLineSegment(sketch, "E160.0.1.8", {"start": v(106.75, -1.5) * mm, "end": v(106.75, 1.5) * mm});
            skLineSegment(sketch, "E160.0.1.9", {"start": v(95, 10.25) * mm, "end": v(95, 13.25) * mm});
            skLineSegment(sketch, "E160.0.1.10", {"start": v(98, 10.25) * mm, "end": v(98, 13.25) * mm});
            skLineSegment(sketch, "E160.0.2.0", {"start": v(109.75, 22) * mm, "end": v(109.75, 25) * mm});
            skLineSegment(sketch, "E160.0.2.1", {"start": v(108.25, 35.25) * mm, "end": v(108.25, 23.5) * mm, "construction": true});
            skLineSegment(sketch, "E160.0.2.2", {"start": v(106.75, 22) * mm, "end": v(109.75, 22) * mm});
            skLineSegment(sketch, "E160.0.2.3", {"start": v(106.75, 25) * mm, "end": v(109.75, 25) * mm});
            skLineSegment(sketch, "E160.0.2.4", {"start": v(95, 36.75) * mm, "end": v(98, 36.75) * mm});
            skPoint(sketch, "E160.0.2.5", {"position": v(96.5, 35.25) * mm});
            skPoint(sketch, "E160.0.2.6", {"position": v(108.25, 23.5) * mm});
            skLineSegment(sketch, "E160.0.2.7", {"start": v(95, 33.75) * mm, "end": v(98, 33.75) * mm});
            skLineSegment(sketch, "E160.0.2.8", {"start": v(106.75, 22) * mm, "end": v(106.75, 25) * mm});
            skLineSegment(sketch, "E160.0.2.9", {"start": v(95, 33.75) * mm, "end": v(95, 36.75) * mm});
            skLineSegment(sketch, "E160.0.2.10", {"start": v(98, 33.75) * mm, "end": v(98, 36.75) * mm});
            skLineSegment(sketch, "E160.0.3.0", {"start": v(109.75, 45.5) * mm, "end": v(109.75, 48.5) * mm});
            skLineSegment(sketch, "E160.0.3.1", {"start": v(108.25, 58.75) * mm, "end": v(108.25, 47) * mm, "construction": true});
            skLineSegment(sketch, "E160.0.3.2", {"start": v(106.75, 45.5) * mm, "end": v(109.75, 45.5) * mm});
            skLineSegment(sketch, "E160.0.3.3", {"start": v(106.75, 48.5) * mm, "end": v(109.75, 48.5) * mm});
            skLineSegment(sketch, "E160.0.3.4", {"start": v(95, 60.25) * mm, "end": v(98, 60.25) * mm});
            skPoint(sketch, "E160.0.3.5", {"position": v(96.5, 58.75) * mm});
            skPoint(sketch, "E160.0.3.6", {"position": v(108.25, 47) * mm});
            skLineSegment(sketch, "E160.0.3.7", {"start": v(95, 57.25) * mm, "end": v(98, 57.25) * mm});
            skLineSegment(sketch, "E160.0.3.8", {"start": v(106.75, 45.5) * mm, "end": v(106.75, 48.5) * mm});
            skLineSegment(sketch, "E160.0.3.9", {"start": v(95, 57.25) * mm, "end": v(95, 60.25) * mm});
            skLineSegment(sketch, "E160.0.3.10", {"start": v(98, 57.25) * mm, "end": v(98, 60.25) * mm});
            skLineSegment(sketch, "E160.0.4.0", {"start": v(109.75, 69) * mm, "end": v(109.75, 72) * mm});
            skLineSegment(sketch, "E160.0.4.1", {"start": v(108.25, 82.25) * mm, "end": v(108.25, 70.5) * mm, "construction": true});
            skLineSegment(sketch, "E160.0.4.2", {"start": v(106.75, 69) * mm, "end": v(109.75, 69) * mm});
            skLineSegment(sketch, "E160.0.4.3", {"start": v(106.75, 72) * mm, "end": v(109.75, 72) * mm});
            skLineSegment(sketch, "E160.0.4.4", {"start": v(95, 83.75) * mm, "end": v(98, 83.75) * mm});
            skPoint(sketch, "E160.0.4.5", {"position": v(96.5, 82.25) * mm});
            skPoint(sketch, "E160.0.4.6", {"position": v(108.25, 70.5) * mm});
            skLineSegment(sketch, "E160.0.4.7", {"start": v(95, 80.75) * mm, "end": v(98, 80.75) * mm});
            skLineSegment(sketch, "E160.0.4.8", {"start": v(106.75, 69) * mm, "end": v(106.75, 72) * mm});
            skLineSegment(sketch, "E160.0.4.9", {"start": v(95, 80.75) * mm, "end": v(95, 83.75) * mm});
            skLineSegment(sketch, "E160.0.4.10", {"start": v(98, 80.75) * mm, "end": v(98, 83.75) * mm});
            skLineSegment(sketch, "E160.1.0.0", {"start": v(133.25, -25) * mm, "end": v(133.25, -22) * mm});
            skLineSegment(sketch, "E160.1.0.1", {"start": v(131.75, -11.75) * mm, "end": v(131.75, -23.5) * mm, "construction": true});
            skLineSegment(sketch, "E160.1.0.2", {"start": v(130.25, -25) * mm, "end": v(133.25, -25) * mm});
            skLineSegment(sketch, "E160.1.0.3", {"start": v(130.25, -22) * mm, "end": v(133.25, -22) * mm});
            skLineSegment(sketch, "E160.1.0.4", {"start": v(118.5, -10.25) * mm, "end": v(121.5, -10.25) * mm});
            skPoint(sketch, "E160.1.0.5", {"position": v(120, -11.75) * mm});
            skPoint(sketch, "E160.1.0.6", {"position": v(131.75, -23.5) * mm});
            skLineSegment(sketch, "E160.1.0.7", {"start": v(118.5, -13.25) * mm, "end": v(121.5, -13.25) * mm});
            skLineSegment(sketch, "E160.1.0.8", {"start": v(130.25, -25) * mm, "end": v(130.25, -22) * mm});
            skLineSegment(sketch, "E160.1.0.9", {"start": v(118.5, -13.25) * mm, "end": v(118.5, -10.25) * mm});
            skLineSegment(sketch, "E160.1.0.10", {"start": v(121.5, -13.25) * mm, "end": v(121.5, -10.25) * mm});
            skLineSegment(sketch, "E160.1.1.0", {"start": v(133.25, -1.5) * mm, "end": v(133.25, 1.5) * mm});
            skLineSegment(sketch, "E160.1.1.1", {"start": v(131.75, 11.75) * mm, "end": v(131.75, 0) * mm, "construction": true});
            skLineSegment(sketch, "E160.1.1.2", {"start": v(130.25, -1.5) * mm, "end": v(133.25, -1.5) * mm});
            skLineSegment(sketch, "E160.1.1.3", {"start": v(130.25, 1.5) * mm, "end": v(133.25, 1.5) * mm});
            skLineSegment(sketch, "E160.1.1.4", {"start": v(118.5, 13.25) * mm, "end": v(121.5, 13.25) * mm});
            skPoint(sketch, "E160.1.1.5", {"position": v(120, 11.75) * mm});
            skPoint(sketch, "E160.1.1.6", {"position": v(131.75, 0) * mm});
            skLineSegment(sketch, "E160.1.1.7", {"start": v(118.5, 10.25) * mm, "end": v(121.5, 10.25) * mm});
            skLineSegment(sketch, "E160.1.1.8", {"start": v(130.25, -1.5) * mm, "end": v(130.25, 1.5) * mm});
            skLineSegment(sketch, "E160.1.1.9", {"start": v(118.5, 10.25) * mm, "end": v(118.5, 13.25) * mm});
            skLineSegment(sketch, "E160.1.1.10", {"start": v(121.5, 10.25) * mm, "end": v(121.5, 13.25) * mm});
            skLineSegment(sketch, "E160.1.2.0", {"start": v(133.25, 22) * mm, "end": v(133.25, 25) * mm});
            skLineSegment(sketch, "E160.1.2.1", {"start": v(131.75, 35.25) * mm, "end": v(131.75, 23.5) * mm, "construction": true});
            skLineSegment(sketch, "E160.1.2.2", {"start": v(130.25, 22) * mm, "end": v(133.25, 22) * mm});
            skLineSegment(sketch, "E160.1.2.3", {"start": v(130.25, 25) * mm, "end": v(133.25, 25) * mm});
            skLineSegment(sketch, "E160.1.2.4", {"start": v(118.5, 36.75) * mm, "end": v(121.5, 36.75) * mm});
            skPoint(sketch, "E160.1.2.5", {"position": v(120, 35.25) * mm});
            skPoint(sketch, "E160.1.2.6", {"position": v(131.75, 23.5) * mm});
            skLineSegment(sketch, "E160.1.2.7", {"start": v(118.5, 33.75) * mm, "end": v(121.5, 33.75) * mm});
            skLineSegment(sketch, "E160.1.2.8", {"start": v(130.25, 22) * mm, "end": v(130.25, 25) * mm});
            skLineSegment(sketch, "E160.1.2.9", {"start": v(118.5, 33.75) * mm, "end": v(118.5, 36.75) * mm});
            skLineSegment(sketch, "E160.1.2.10", {"start": v(121.5, 33.75) * mm, "end": v(121.5, 36.75) * mm});
            skLineSegment(sketch, "E160.1.3.0", {"start": v(133.25, 45.5) * mm, "end": v(133.25, 48.5) * mm});
            skLineSegment(sketch, "E160.1.3.1", {"start": v(131.75, 58.75) * mm, "end": v(131.75, 47) * mm, "construction": true});
            skLineSegment(sketch, "E160.1.3.2", {"start": v(130.25, 45.5) * mm, "end": v(133.25, 45.5) * mm});
            skLineSegment(sketch, "E160.1.3.3", {"start": v(130.25, 48.5) * mm, "end": v(133.25, 48.5) * mm});
            skLineSegment(sketch, "E160.1.3.4", {"start": v(118.5, 60.25) * mm, "end": v(121.5, 60.25) * mm});
            skPoint(sketch, "E160.1.3.5", {"position": v(120, 58.75) * mm});
            skPoint(sketch, "E160.1.3.6", {"position": v(131.75, 47) * mm});
            skLineSegment(sketch, "E160.1.3.7", {"start": v(118.5, 57.25) * mm, "end": v(121.5, 57.25) * mm});
            skLineSegment(sketch, "E160.1.3.8", {"start": v(130.25, 45.5) * mm, "end": v(130.25, 48.5) * mm});
            skLineSegment(sketch, "E160.1.3.9", {"start": v(118.5, 57.25) * mm, "end": v(118.5, 60.25) * mm});
            skLineSegment(sketch, "E160.1.3.10", {"start": v(121.5, 57.25) * mm, "end": v(121.5, 60.25) * mm});
            skLineSegment(sketch, "E160.1.4.0", {"start": v(133.25, 69) * mm, "end": v(133.25, 72) * mm});
            skLineSegment(sketch, "E160.1.4.1", {"start": v(131.75, 82.25) * mm, "end": v(131.75, 70.5) * mm, "construction": true});
            skLineSegment(sketch, "E160.1.4.2", {"start": v(130.25, 69) * mm, "end": v(133.25, 69) * mm});
            skLineSegment(sketch, "E160.1.4.3", {"start": v(130.25, 72) * mm, "end": v(133.25, 72) * mm});
            skLineSegment(sketch, "E160.1.4.4", {"start": v(118.5, 83.75) * mm, "end": v(121.5, 83.75) * mm});
            skPoint(sketch, "E160.1.4.5", {"position": v(120, 82.25) * mm});
            skPoint(sketch, "E160.1.4.6", {"position": v(131.75, 70.5) * mm});
            skLineSegment(sketch, "E160.1.4.7", {"start": v(118.5, 80.75) * mm, "end": v(121.5, 80.75) * mm});
            skLineSegment(sketch, "E160.1.4.8", {"start": v(130.25, 69) * mm, "end": v(130.25, 72) * mm});
            skLineSegment(sketch, "E160.1.4.9", {"start": v(118.5, 80.75) * mm, "end": v(118.5, 83.75) * mm});
            skLineSegment(sketch, "E160.1.4.10", {"start": v(121.5, 80.75) * mm, "end": v(121.5, 83.75) * mm});
            skLineSegment(sketch, "E160.2.0.0", {"start": v(156.75, -25) * mm, "end": v(156.75, -22) * mm});
            skLineSegment(sketch, "E160.2.0.1", {"start": v(155.25, -11.75) * mm, "end": v(155.25, -23.5) * mm, "construction": true});
            skLineSegment(sketch, "E160.2.0.2", {"start": v(153.75, -25) * mm, "end": v(156.75, -25) * mm});
            skLineSegment(sketch, "E160.2.0.3", {"start": v(153.75, -22) * mm, "end": v(156.75, -22) * mm});
            skLineSegment(sketch, "E160.2.0.4", {"start": v(142, -10.25) * mm, "end": v(145, -10.25) * mm});
            skPoint(sketch, "E160.2.0.5", {"position": v(143.5, -11.75) * mm});
            skPoint(sketch, "E160.2.0.6", {"position": v(155.25, -23.5) * mm});
            skLineSegment(sketch, "E160.2.0.7", {"start": v(142, -13.25) * mm, "end": v(145, -13.25) * mm});
            skLineSegment(sketch, "E160.2.0.8", {"start": v(153.75, -25) * mm, "end": v(153.75, -22) * mm});
            skLineSegment(sketch, "E160.2.0.9", {"start": v(142, -13.25) * mm, "end": v(142, -10.25) * mm});
            skLineSegment(sketch, "E160.2.0.10", {"start": v(145, -13.25) * mm, "end": v(145, -10.25) * mm});
            skLineSegment(sketch, "E160.2.1.0", {"start": v(156.75, -1.5) * mm, "end": v(156.75, 1.5) * mm});
            skLineSegment(sketch, "E160.2.1.1", {"start": v(155.25, 11.75) * mm, "end": v(155.25, 0) * mm, "construction": true});
            skLineSegment(sketch, "E160.2.1.2", {"start": v(153.75, -1.5) * mm, "end": v(156.75, -1.5) * mm});
            skLineSegment(sketch, "E160.2.1.3", {"start": v(153.75, 1.5) * mm, "end": v(156.75, 1.5) * mm});
            skLineSegment(sketch, "E160.2.1.4", {"start": v(142, 13.25) * mm, "end": v(145, 13.25) * mm});
            skPoint(sketch, "E160.2.1.5", {"position": v(143.5, 11.75) * mm});
            skPoint(sketch, "E160.2.1.6", {"position": v(155.25, 0) * mm});
            skLineSegment(sketch, "E160.2.1.7", {"start": v(142, 10.25) * mm, "end": v(145, 10.25) * mm});
            skLineSegment(sketch, "E160.2.1.8", {"start": v(153.75, -1.5) * mm, "end": v(153.75, 1.5) * mm});
            skLineSegment(sketch, "E160.2.1.9", {"start": v(142, 10.25) * mm, "end": v(142, 13.25) * mm});
            skLineSegment(sketch, "E160.2.1.10", {"start": v(145, 10.25) * mm, "end": v(145, 13.25) * mm});
            skLineSegment(sketch, "E160.2.2.0", {"start": v(156.75, 22) * mm, "end": v(156.75, 25) * mm});
            skLineSegment(sketch, "E160.2.2.1", {"start": v(155.25, 35.25) * mm, "end": v(155.25, 23.5) * mm, "construction": true});
            skLineSegment(sketch, "E160.2.2.2", {"start": v(153.75, 22) * mm, "end": v(156.75, 22) * mm});
            skLineSegment(sketch, "E160.2.2.3", {"start": v(153.75, 25) * mm, "end": v(156.75, 25) * mm});
            skLineSegment(sketch, "E160.2.2.4", {"start": v(142, 36.75) * mm, "end": v(145, 36.75) * mm});
            skPoint(sketch, "E160.2.2.5", {"position": v(143.5, 35.25) * mm});
            skPoint(sketch, "E160.2.2.6", {"position": v(155.25, 23.5) * mm});
            skLineSegment(sketch, "E160.2.2.7", {"start": v(142, 33.75) * mm, "end": v(145, 33.75) * mm});
            skLineSegment(sketch, "E160.2.2.8", {"start": v(153.75, 22) * mm, "end": v(153.75, 25) * mm});
            skLineSegment(sketch, "E160.2.2.9", {"start": v(142, 33.75) * mm, "end": v(142, 36.75) * mm});
            skLineSegment(sketch, "E160.2.2.10", {"start": v(145, 33.75) * mm, "end": v(145, 36.75) * mm});
            skLineSegment(sketch, "E160.2.3.0", {"start": v(156.75, 45.5) * mm, "end": v(156.75, 48.5) * mm});
            skLineSegment(sketch, "E160.2.3.1", {"start": v(155.25, 58.75) * mm, "end": v(155.25, 47) * mm, "construction": true});
            skLineSegment(sketch, "E160.2.3.2", {"start": v(153.75, 45.5) * mm, "end": v(156.75, 45.5) * mm});
            skLineSegment(sketch, "E160.2.3.3", {"start": v(153.75, 48.5) * mm, "end": v(156.75, 48.5) * mm});
            skLineSegment(sketch, "E160.2.3.4", {"start": v(142, 60.25) * mm, "end": v(145, 60.25) * mm});
            skPoint(sketch, "E160.2.3.5", {"position": v(143.5, 58.75) * mm});
            skPoint(sketch, "E160.2.3.6", {"position": v(155.25, 47) * mm});
            skLineSegment(sketch, "E160.2.3.7", {"start": v(142, 57.25) * mm, "end": v(145, 57.25) * mm});
            skLineSegment(sketch, "E160.2.3.8", {"start": v(153.75, 45.5) * mm, "end": v(153.75, 48.5) * mm});
            skLineSegment(sketch, "E160.2.3.9", {"start": v(142, 57.25) * mm, "end": v(142, 60.25) * mm});
            skLineSegment(sketch, "E160.2.3.10", {"start": v(145, 57.25) * mm, "end": v(145, 60.25) * mm});
            skLineSegment(sketch, "E160.2.4.0", {"start": v(156.75, 69) * mm, "end": v(156.75, 72) * mm});
            skLineSegment(sketch, "E160.2.4.1", {"start": v(155.25, 82.25) * mm, "end": v(155.25, 70.5) * mm, "construction": true});
            skLineSegment(sketch, "E160.2.4.2", {"start": v(153.75, 69) * mm, "end": v(156.75, 69) * mm});
            skLineSegment(sketch, "E160.2.4.3", {"start": v(153.75, 72) * mm, "end": v(156.75, 72) * mm});
            skLineSegment(sketch, "E160.2.4.4", {"start": v(142, 83.75) * mm, "end": v(145, 83.75) * mm});
            skPoint(sketch, "E160.2.4.5", {"position": v(143.5, 82.25) * mm});
            skPoint(sketch, "E160.2.4.6", {"position": v(155.25, 70.5) * mm});
            skLineSegment(sketch, "E160.2.4.7", {"start": v(142, 80.75) * mm, "end": v(145, 80.75) * mm});
            skLineSegment(sketch, "E160.2.4.8", {"start": v(153.75, 69) * mm, "end": v(153.75, 72) * mm});
            skLineSegment(sketch, "E160.2.4.9", {"start": v(142, 80.75) * mm, "end": v(142, 83.75) * mm});
            skLineSegment(sketch, "E160.2.4.10", {"start": v(145, 80.75) * mm, "end": v(145, 83.75) * mm});
            skLineSegment(sketch, "E160.3.0.0", {"start": v(180.25, -25) * mm, "end": v(180.25, -22) * mm});
            skLineSegment(sketch, "E160.3.0.1", {"start": v(178.75, -11.75) * mm, "end": v(178.75, -23.5) * mm, "construction": true});
            skLineSegment(sketch, "E160.3.0.2", {"start": v(177.25, -25) * mm, "end": v(180.25, -25) * mm});
            skLineSegment(sketch, "E160.3.0.3", {"start": v(177.25, -22) * mm, "end": v(180.25, -22) * mm});
            skLineSegment(sketch, "E160.3.0.4", {"start": v(165.5, -10.25) * mm, "end": v(168.5, -10.25) * mm});
            skPoint(sketch, "E160.3.0.5", {"position": v(167, -11.75) * mm});
            skPoint(sketch, "E160.3.0.6", {"position": v(178.75, -23.5) * mm});
            skLineSegment(sketch, "E160.3.0.7", {"start": v(165.5, -13.25) * mm, "end": v(168.5, -13.25) * mm});
            skLineSegment(sketch, "E160.3.0.8", {"start": v(177.25, -25) * mm, "end": v(177.25, -22) * mm});
            skLineSegment(sketch, "E160.3.0.9", {"start": v(165.5, -13.25) * mm, "end": v(165.5, -10.25) * mm});
            skLineSegment(sketch, "E160.3.0.10", {"start": v(168.5, -13.25) * mm, "end": v(168.5, -10.25) * mm});
            skLineSegment(sketch, "E160.3.1.0", {"start": v(180.25, -1.5) * mm, "end": v(180.25, 1.5) * mm});
            skLineSegment(sketch, "E160.3.1.1", {"start": v(178.75, 11.75) * mm, "end": v(178.75, 0) * mm, "construction": true});
            skLineSegment(sketch, "E160.3.1.2", {"start": v(177.25, -1.5) * mm, "end": v(180.25, -1.5) * mm});
            skLineSegment(sketch, "E160.3.1.3", {"start": v(177.25, 1.5) * mm, "end": v(180.25, 1.5) * mm});
            skLineSegment(sketch, "E160.3.1.4", {"start": v(165.5, 13.25) * mm, "end": v(168.5, 13.25) * mm});
            skPoint(sketch, "E160.3.1.5", {"position": v(167, 11.75) * mm});
            skPoint(sketch, "E160.3.1.6", {"position": v(178.75, 0) * mm});
            skLineSegment(sketch, "E160.3.1.7", {"start": v(165.5, 10.25) * mm, "end": v(168.5, 10.25) * mm});
            skLineSegment(sketch, "E160.3.1.8", {"start": v(177.25, -1.5) * mm, "end": v(177.25, 1.5) * mm});
            skLineSegment(sketch, "E160.3.1.9", {"start": v(165.5, 10.25) * mm, "end": v(165.5, 13.25) * mm});
            skLineSegment(sketch, "E160.3.1.10", {"start": v(168.5, 10.25) * mm, "end": v(168.5, 13.25) * mm});
            skLineSegment(sketch, "E160.3.2.0", {"start": v(180.25, 22) * mm, "end": v(180.25, 25) * mm});
            skLineSegment(sketch, "E160.3.2.1", {"start": v(178.75, 35.25) * mm, "end": v(178.75, 23.5) * mm, "construction": true});
            skLineSegment(sketch, "E160.3.2.2", {"start": v(177.25, 22) * mm, "end": v(180.25, 22) * mm});
            skLineSegment(sketch, "E160.3.2.3", {"start": v(177.25, 25) * mm, "end": v(180.25, 25) * mm});
            skLineSegment(sketch, "E160.3.2.4", {"start": v(165.5, 36.75) * mm, "end": v(168.5, 36.75) * mm});
            skPoint(sketch, "E160.3.2.5", {"position": v(167, 35.25) * mm});
            skPoint(sketch, "E160.3.2.6", {"position": v(178.75, 23.5) * mm});
            skLineSegment(sketch, "E160.3.2.7", {"start": v(165.5, 33.75) * mm, "end": v(168.5, 33.75) * mm});
            skLineSegment(sketch, "E160.3.2.8", {"start": v(177.25, 22) * mm, "end": v(177.25, 25) * mm});
            skLineSegment(sketch, "E160.3.2.9", {"start": v(165.5, 33.75) * mm, "end": v(165.5, 36.75) * mm});
            skLineSegment(sketch, "E160.3.2.10", {"start": v(168.5, 33.75) * mm, "end": v(168.5, 36.75) * mm});
            skLineSegment(sketch, "E160.3.3.0", {"start": v(180.25, 45.5) * mm, "end": v(180.25, 48.5) * mm});
            skLineSegment(sketch, "E160.3.3.1", {"start": v(178.75, 58.75) * mm, "end": v(178.75, 47) * mm, "construction": true});
            skLineSegment(sketch, "E160.3.3.2", {"start": v(177.25, 45.5) * mm, "end": v(180.25, 45.5) * mm});
            skLineSegment(sketch, "E160.3.3.3", {"start": v(177.25, 48.5) * mm, "end": v(180.25, 48.5) * mm});
            skLineSegment(sketch, "E160.3.3.4", {"start": v(165.5, 60.25) * mm, "end": v(168.5, 60.25) * mm});
            skPoint(sketch, "E160.3.3.5", {"position": v(167, 58.75) * mm});
            skPoint(sketch, "E160.3.3.6", {"position": v(178.75, 47) * mm});
            skLineSegment(sketch, "E160.3.3.7", {"start": v(165.5, 57.25) * mm, "end": v(168.5, 57.25) * mm});
            skLineSegment(sketch, "E160.3.3.8", {"start": v(177.25, 45.5) * mm, "end": v(177.25, 48.5) * mm});
            skLineSegment(sketch, "E160.3.3.9", {"start": v(165.5, 57.25) * mm, "end": v(165.5, 60.25) * mm});
            skLineSegment(sketch, "E160.3.3.10", {"start": v(168.5, 57.25) * mm, "end": v(168.5, 60.25) * mm});
            skLineSegment(sketch, "E160.3.4.0", {"start": v(180.25, 69) * mm, "end": v(180.25, 72) * mm});
            skLineSegment(sketch, "E160.3.4.1", {"start": v(178.75, 82.25) * mm, "end": v(178.75, 70.5) * mm, "construction": true});
            skLineSegment(sketch, "E160.3.4.2", {"start": v(177.25, 69) * mm, "end": v(180.25, 69) * mm});
            skLineSegment(sketch, "E160.3.4.3", {"start": v(177.25, 72) * mm, "end": v(180.25, 72) * mm});
            skLineSegment(sketch, "E160.3.4.4", {"start": v(165.5, 83.75) * mm, "end": v(168.5, 83.75) * mm});
            skPoint(sketch, "E160.3.4.5", {"position": v(167, 82.25) * mm});
            skPoint(sketch, "E160.3.4.6", {"position": v(178.75, 70.5) * mm});
            skLineSegment(sketch, "E160.3.4.7", {"start": v(165.5, 80.75) * mm, "end": v(168.5, 80.75) * mm});
            skLineSegment(sketch, "E160.3.4.8", {"start": v(177.25, 69) * mm, "end": v(177.25, 72) * mm});
            skLineSegment(sketch, "E160.3.4.9", {"start": v(165.5, 80.75) * mm, "end": v(165.5, 83.75) * mm});
            skLineSegment(sketch, "E160.3.4.10", {"start": v(168.5, 80.75) * mm, "end": v(168.5, 83.75) * mm});
            skLineSegment(sketch, "E160.4.0.0", {"start": v(203.75, -25) * mm, "end": v(203.75, -22) * mm});
            skLineSegment(sketch, "E160.4.0.1", {"start": v(202.25, -11.75) * mm, "end": v(202.25, -23.5) * mm, "construction": true});
            skLineSegment(sketch, "E160.4.0.2", {"start": v(200.75, -25) * mm, "end": v(203.75, -25) * mm});
            skLineSegment(sketch, "E160.4.0.3", {"start": v(200.75, -22) * mm, "end": v(203.75, -22) * mm});
            skLineSegment(sketch, "E160.4.0.4", {"start": v(189, -10.25) * mm, "end": v(192, -10.25) * mm});
            skPoint(sketch, "E160.4.0.5", {"position": v(190.5, -11.75) * mm});
            skPoint(sketch, "E160.4.0.6", {"position": v(202.25, -23.5) * mm});
            skLineSegment(sketch, "E160.4.0.7", {"start": v(189, -13.25) * mm, "end": v(192, -13.25) * mm});
            skLineSegment(sketch, "E160.4.0.8", {"start": v(200.75, -25) * mm, "end": v(200.75, -22) * mm});
            skLineSegment(sketch, "E160.4.0.9", {"start": v(189, -13.25) * mm, "end": v(189, -10.25) * mm});
            skLineSegment(sketch, "E160.4.0.10", {"start": v(192, -13.25) * mm, "end": v(192, -10.25) * mm});
            skLineSegment(sketch, "E160.4.1.0", {"start": v(203.75, -1.5) * mm, "end": v(203.75, 1.5) * mm});
            skLineSegment(sketch, "E160.4.1.1", {"start": v(202.25, 11.75) * mm, "end": v(202.25, 0) * mm, "construction": true});
            skLineSegment(sketch, "E160.4.1.2", {"start": v(200.75, -1.5) * mm, "end": v(203.75, -1.5) * mm});
            skLineSegment(sketch, "E160.4.1.3", {"start": v(200.75, 1.5) * mm, "end": v(203.75, 1.5) * mm});
            skLineSegment(sketch, "E160.4.1.4", {"start": v(189, 13.25) * mm, "end": v(192, 13.25) * mm});
            skPoint(sketch, "E160.4.1.5", {"position": v(190.5, 11.75) * mm});
            skPoint(sketch, "E160.4.1.6", {"position": v(202.25, 0) * mm});
            skLineSegment(sketch, "E160.4.1.7", {"start": v(189, 10.25) * mm, "end": v(192, 10.25) * mm});
            skLineSegment(sketch, "E160.4.1.8", {"start": v(200.75, -1.5) * mm, "end": v(200.75, 1.5) * mm});
            skLineSegment(sketch, "E160.4.1.9", {"start": v(189, 10.25) * mm, "end": v(189, 13.25) * mm});
            skLineSegment(sketch, "E160.4.1.10", {"start": v(192, 10.25) * mm, "end": v(192, 13.25) * mm});
            skLineSegment(sketch, "E160.4.2.0", {"start": v(203.75, 22) * mm, "end": v(203.75, 25) * mm});
            skLineSegment(sketch, "E160.4.2.1", {"start": v(202.25, 35.25) * mm, "end": v(202.25, 23.5) * mm, "construction": true});
            skLineSegment(sketch, "E160.4.2.2", {"start": v(200.75, 22) * mm, "end": v(203.75, 22) * mm});
            skLineSegment(sketch, "E160.4.2.3", {"start": v(200.75, 25) * mm, "end": v(203.75, 25) * mm});
            skLineSegment(sketch, "E160.4.2.4", {"start": v(189, 36.75) * mm, "end": v(192, 36.75) * mm});
            skPoint(sketch, "E160.4.2.5", {"position": v(190.5, 35.25) * mm});
            skPoint(sketch, "E160.4.2.6", {"position": v(202.25, 23.5) * mm});
            skLineSegment(sketch, "E160.4.2.7", {"start": v(189, 33.75) * mm, "end": v(192, 33.75) * mm});
            skLineSegment(sketch, "E160.4.2.8", {"start": v(200.75, 22) * mm, "end": v(200.75, 25) * mm});
            skLineSegment(sketch, "E160.4.2.9", {"start": v(189, 33.75) * mm, "end": v(189, 36.75) * mm});
            skLineSegment(sketch, "E160.4.2.10", {"start": v(192, 33.75) * mm, "end": v(192, 36.75) * mm});
            skLineSegment(sketch, "E160.4.3.0", {"start": v(203.75, 45.5) * mm, "end": v(203.75, 48.5) * mm});
            skLineSegment(sketch, "E160.4.3.1", {"start": v(202.25, 58.75) * mm, "end": v(202.25, 47) * mm, "construction": true});
            skLineSegment(sketch, "E160.4.3.2", {"start": v(200.75, 45.5) * mm, "end": v(203.75, 45.5) * mm});
            skLineSegment(sketch, "E160.4.3.3", {"start": v(200.75, 48.5) * mm, "end": v(203.75, 48.5) * mm});
            skLineSegment(sketch, "E160.4.3.4", {"start": v(189, 60.25) * mm, "end": v(192, 60.25) * mm});
            skPoint(sketch, "E160.4.3.5", {"position": v(190.5, 58.75) * mm});
            skPoint(sketch, "E160.4.3.6", {"position": v(202.25, 47) * mm});
            skLineSegment(sketch, "E160.4.3.7", {"start": v(189, 57.25) * mm, "end": v(192, 57.25) * mm});
            skLineSegment(sketch, "E160.4.3.8", {"start": v(200.75, 45.5) * mm, "end": v(200.75, 48.5) * mm});
            skLineSegment(sketch, "E160.4.3.9", {"start": v(189, 57.25) * mm, "end": v(189, 60.25) * mm});
            skLineSegment(sketch, "E160.4.3.10", {"start": v(192, 57.25) * mm, "end": v(192, 60.25) * mm});
            skLineSegment(sketch, "E160.4.4.0", {"start": v(203.75, 69) * mm, "end": v(203.75, 72) * mm});
            skLineSegment(sketch, "E160.4.4.1", {"start": v(202.25, 82.25) * mm, "end": v(202.25, 70.5) * mm, "construction": true});
            skLineSegment(sketch, "E160.4.4.2", {"start": v(200.75, 69) * mm, "end": v(203.75, 69) * mm});
            skLineSegment(sketch, "E160.4.4.3", {"start": v(200.75, 72) * mm, "end": v(203.75, 72) * mm});
            skLineSegment(sketch, "E160.4.4.4", {"start": v(189, 83.75) * mm, "end": v(192, 83.75) * mm});
            skPoint(sketch, "E160.4.4.5", {"position": v(190.5, 82.25) * mm});
            skPoint(sketch, "E160.4.4.6", {"position": v(202.25, 70.5) * mm});
            skLineSegment(sketch, "E160.4.4.7", {"start": v(189, 80.75) * mm, "end": v(192, 80.75) * mm});
            skLineSegment(sketch, "E160.4.4.8", {"start": v(200.75, 69) * mm, "end": v(200.75, 72) * mm});
            skLineSegment(sketch, "E160.4.4.9", {"start": v(189, 80.75) * mm, "end": v(189, 83.75) * mm});
            skLineSegment(sketch, "E160.4.4.10", {"start": v(192, 80.75) * mm, "end": v(192, 83.75) * mm});
            skLineSegment(sketch, "E160.direction1", {"start": v(106.75, -25) * mm, "end": v(130.25, -25) * mm, "construction": true});
            skLineSegment(sketch, "E160.direction2", {"start": v(106.75, -25) * mm, "end": v(106.75, -1.5) * mm, "construction": true});
            skSolve(sketch);
        }
        {
            var Q0;
            Q0=qSketchRegion(id+"F28",true);
            extrude(context, id + "F29", {"entities" : qUnion([Q0]), "operationType" : NewBodyOperationType.REMOVE, "depth" : 25 * mm});
        }
        {
            var Q0;
            Q0=qCreatedBy(makeId("Top.planeOp"),FACE);
            var sketch = newSketch(context, id + "F30", { "sketchPlane" : qUnion([Q0])});
            skLineSegment(sketch, "E161", {"start": v(0, 0) * mm, "end": v(120, 0) * mm, "construction": true});
            skLineSegment(sketch, "E162", {"start": v(120, 0) * mm, "end": v(120, -11.75) * mm, "construction": true});
            skLineSegment(sketch, "E163", {"start": v(120, -11.75) * mm, "end": v(96.5, -11.75) * mm, "construction": true});
            skCircle(sketch, "E164", {"center": v(96.5, -11.75) * mm, "radius": 1.05 * mm});
            skLineSegment(sketch, "E165", {"start": v(108.25, -11.75) * mm, "end": v(108.25, -23.5) * mm, "construction": true});
            skCircle(sketch, "E166", {"center": v(108.25, -23.5) * mm, "radius": 1.05 * mm});
            skCircle(sketch, "E167.0.1.0", {"center": v(108.25, 0) * mm, "radius": 1.05 * mm});
            skLineSegment(sketch, "E167.0.1.1", {"start": v(108.25, 11.75) * mm, "end": v(108.25, 0) * mm, "construction": true});
            skCircle(sketch, "E167.0.1.2", {"center": v(96.5, 11.75) * mm, "radius": 1.05 * mm});
            skCircle(sketch, "E167.0.2.0", {"center": v(108.25, 23.5) * mm, "radius": 1.05 * mm});
            skLineSegment(sketch, "E167.0.2.1", {"start": v(108.25, 35.25) * mm, "end": v(108.25, 23.5) * mm, "construction": true});
            skCircle(sketch, "E167.0.2.2", {"center": v(96.5, 35.25) * mm, "radius": 1.05 * mm});
            skCircle(sketch, "E167.0.3.0", {"center": v(108.25, 47) * mm, "radius": 1.05 * mm});
            skLineSegment(sketch, "E167.0.3.1", {"start": v(108.25, 58.75) * mm, "end": v(108.25, 47) * mm, "construction": true});
            skCircle(sketch, "E167.0.3.2", {"center": v(96.5, 58.75) * mm, "radius": 1.05 * mm});
            skCircle(sketch, "E167.0.4.0", {"center": v(108.25, 70.5) * mm, "radius": 1.05 * mm});
            skLineSegment(sketch, "E167.0.4.1", {"start": v(108.25, 82.25) * mm, "end": v(108.25, 70.5) * mm, "construction": true});
            skCircle(sketch, "E167.0.4.2", {"center": v(96.5, 82.25) * mm, "radius": 1.05 * mm});
            skCircle(sketch, "E167.1.0.0", {"center": v(131.75, -23.5) * mm, "radius": 1.05 * mm});
            skLineSegment(sketch, "E167.1.0.1", {"start": v(131.75, -11.75) * mm, "end": v(131.75, -23.5) * mm, "construction": true});
            skCircle(sketch, "E167.1.0.2", {"center": v(120, -11.75) * mm, "radius": 1.05 * mm});
            skCircle(sketch, "E167.1.1.0", {"center": v(131.75, 0) * mm, "radius": 1.05 * mm});
            skLineSegment(sketch, "E167.1.1.1", {"start": v(131.75, 11.75) * mm, "end": v(131.75, 0) * mm, "construction": true});
            skCircle(sketch, "E167.1.1.2", {"center": v(120, 11.75) * mm, "radius": 1.05 * mm});
            skCircle(sketch, "E167.1.2.0", {"center": v(131.75, 23.5) * mm, "radius": 1.05 * mm});
            skLineSegment(sketch, "E167.1.2.1", {"start": v(131.75, 35.25) * mm, "end": v(131.75, 23.5) * mm, "construction": true});
            skCircle(sketch, "E167.1.2.2", {"center": v(120, 35.25) * mm, "radius": 1.05 * mm});
            skCircle(sketch, "E167.1.3.0", {"center": v(131.75, 47) * mm, "radius": 1.05 * mm});
            skLineSegment(sketch, "E167.1.3.1", {"start": v(131.75, 58.75) * mm, "end": v(131.75, 47) * mm, "construction": true});
            skCircle(sketch, "E167.1.3.2", {"center": v(120, 58.75) * mm, "radius": 1.05 * mm});
            skCircle(sketch, "E167.1.4.0", {"center": v(131.75, 70.5) * mm, "radius": 1.05 * mm});
            skLineSegment(sketch, "E167.1.4.1", {"start": v(131.75, 82.25) * mm, "end": v(131.75, 70.5) * mm, "construction": true});
            skCircle(sketch, "E167.1.4.2", {"center": v(120, 82.25) * mm, "radius": 1.05 * mm});
            skCircle(sketch, "E167.2.0.0", {"center": v(155.25, -23.5) * mm, "radius": 1.05 * mm});
            skLineSegment(sketch, "E167.2.0.1", {"start": v(155.25, -11.75) * mm, "end": v(155.25, -23.5) * mm, "construction": true});
            skCircle(sketch, "E167.2.0.2", {"center": v(143.5, -11.75) * mm, "radius": 1.05 * mm});
            skCircle(sketch, "E167.2.1.0", {"center": v(155.25, 0) * mm, "radius": 1.05 * mm});
            skLineSegment(sketch, "E167.2.1.1", {"start": v(155.25, 11.75) * mm, "end": v(155.25, 0) * mm, "construction": true});
            skCircle(sketch, "E167.2.1.2", {"center": v(143.5, 11.75) * mm, "radius": 1.05 * mm});
            skCircle(sketch, "E167.2.2.0", {"center": v(155.25, 23.5) * mm, "radius": 1.05 * mm});
            skLineSegment(sketch, "E167.2.2.1", {"start": v(155.25, 35.25) * mm, "end": v(155.25, 23.5) * mm, "construction": true});
            skCircle(sketch, "E167.2.2.2", {"center": v(143.5, 35.25) * mm, "radius": 1.05 * mm});
            skCircle(sketch, "E167.2.3.0", {"center": v(155.25, 47) * mm, "radius": 1.05 * mm});
            skLineSegment(sketch, "E167.2.3.1", {"start": v(155.25, 58.75) * mm, "end": v(155.25, 47) * mm, "construction": true});
            skCircle(sketch, "E167.2.3.2", {"center": v(143.5, 58.75) * mm, "radius": 1.05 * mm});
            skCircle(sketch, "E167.2.4.0", {"center": v(155.25, 70.5) * mm, "radius": 1.05 * mm});
            skLineSegment(sketch, "E167.2.4.1", {"start": v(155.25, 82.25) * mm, "end": v(155.25, 70.5) * mm, "construction": true});
            skCircle(sketch, "E167.2.4.2", {"center": v(143.5, 82.25) * mm, "radius": 1.05 * mm});
            skCircle(sketch, "E167.3.0.0", {"center": v(178.75, -23.5) * mm, "radius": 1.05 * mm});
            skLineSegment(sketch, "E167.3.0.1", {"start": v(178.75, -11.75) * mm, "end": v(178.75, -23.5) * mm, "construction": true});
            skCircle(sketch, "E167.3.0.2", {"center": v(167, -11.75) * mm, "radius": 1.05 * mm});
            skCircle(sketch, "E167.3.1.0", {"center": v(178.75, 0) * mm, "radius": 1.05 * mm});
            skLineSegment(sketch, "E167.3.1.1", {"start": v(178.75, 11.75) * mm, "end": v(178.75, 0) * mm, "construction": true});
            skCircle(sketch, "E167.3.1.2", {"center": v(167, 11.75) * mm, "radius": 1.05 * mm});
            skCircle(sketch, "E167.3.2.0", {"center": v(178.75, 23.5) * mm, "radius": 1.05 * mm});
            skLineSegment(sketch, "E167.3.2.1", {"start": v(178.75, 35.25) * mm, "end": v(178.75, 23.5) * mm, "construction": true});
            skCircle(sketch, "E167.3.2.2", {"center": v(167, 35.25) * mm, "radius": 1.05 * mm});
            skCircle(sketch, "E167.3.3.0", {"center": v(178.75, 47) * mm, "radius": 1.05 * mm});
            skLineSegment(sketch, "E167.3.3.1", {"start": v(178.75, 58.75) * mm, "end": v(178.75, 47) * mm, "construction": true});
            skCircle(sketch, "E167.3.3.2", {"center": v(167, 58.75) * mm, "radius": 1.05 * mm});
            skCircle(sketch, "E167.3.4.0", {"center": v(178.75, 70.5) * mm, "radius": 1.05 * mm});
            skLineSegment(sketch, "E167.3.4.1", {"start": v(178.75, 82.25) * mm, "end": v(178.75, 70.5) * mm, "construction": true});
            skCircle(sketch, "E167.3.4.2", {"center": v(167, 82.25) * mm, "radius": 1.05 * mm});
            skCircle(sketch, "E167.4.0.0", {"center": v(202.25, -23.5) * mm, "radius": 1.05 * mm});
            skLineSegment(sketch, "E167.4.0.1", {"start": v(202.25, -11.75) * mm, "end": v(202.25, -23.5) * mm, "construction": true});
            skCircle(sketch, "E167.4.0.2", {"center": v(190.5, -11.75) * mm, "radius": 1.05 * mm});
            skCircle(sketch, "E167.4.1.0", {"center": v(202.25, 0) * mm, "radius": 1.05 * mm});
            skLineSegment(sketch, "E167.4.1.1", {"start": v(202.25, 11.75) * mm, "end": v(202.25, 0) * mm, "construction": true});
            skCircle(sketch, "E167.4.1.2", {"center": v(190.5, 11.75) * mm, "radius": 1.05 * mm});
            skCircle(sketch, "E167.4.2.0", {"center": v(202.25, 23.5) * mm, "radius": 1.05 * mm});
            skLineSegment(sketch, "E167.4.2.1", {"start": v(202.25, 35.25) * mm, "end": v(202.25, 23.5) * mm, "construction": true});
            skCircle(sketch, "E167.4.2.2", {"center": v(190.5, 35.25) * mm, "radius": 1.05 * mm});
            skCircle(sketch, "E167.4.3.0", {"center": v(202.25, 47) * mm, "radius": 1.05 * mm});
            skLineSegment(sketch, "E167.4.3.1", {"start": v(202.25, 58.75) * mm, "end": v(202.25, 47) * mm, "construction": true});
            skCircle(sketch, "E167.4.3.2", {"center": v(190.5, 58.75) * mm, "radius": 1.05 * mm});
            skCircle(sketch, "E167.4.4.0", {"center": v(202.25, 70.5) * mm, "radius": 1.05 * mm});
            skLineSegment(sketch, "E167.4.4.1", {"start": v(202.25, 82.25) * mm, "end": v(202.25, 70.5) * mm, "construction": true});
            skCircle(sketch, "E167.4.4.2", {"center": v(190.5, 82.25) * mm, "radius": 1.05 * mm});
            skLineSegment(sketch, "E167.direction1", {"start": v(108.25, -23.5) * mm, "end": v(131.75, -23.5) * mm, "construction": true});
            skLineSegment(sketch, "E167.direction2", {"start": v(108.25, -23.5) * mm, "end": v(108.25, 0) * mm, "construction": true});
            skSolve(sketch);
        }
        {
            var Q0;
            Q0=qSketchRegion(id+"F30",true);
            extrude(context, id + "F31", {"entities" : qUnion([Q0]), "operationType" : NewBodyOperationType.REMOVE, "endBound" : BoundingType.THROUGH_ALL, "depth" : 25 * mm, "hasSecondDirection" : true, "secondDirectionBound" : SecondDirectionBoundingType.THROUGH_ALL, "secondDirectionOppositeDirection" : true, "secondDirectionDepth" : 25 * mm});
        }
        {
            var Q0;
            Q0=qCreatedBy(makeId("Top.planeOp"),FACE);
            var sketch = newSketch(context, id + "F32", { "sketchPlane" : qUnion([Q0])});
            skLineSegment(sketch, "E168", {"start": v(0, 0) * mm, "end": v(120, 0) * mm, "construction": true});
            skLineSegment(sketch, "E169.bottom", {"start": v(98.15, -21.85) * mm, "end": v(141.85, -21.85) * mm, "construction": true});
            skLineSegment(sketch, "E169.top", {"start": v(98.15, 21.85) * mm, "end": v(141.85, 21.85) * mm, "construction": true});
            skLineSegment(sketch, "E169.left", {"start": v(98.15, -21.85) * mm, "end": v(98.15, 21.85) * mm, "construction": true});
            skLineSegment(sketch, "E169.right", {"start": v(141.85, -21.85) * mm, "end": v(141.85, 21.85) * mm, "construction": true});
            skPoint(sketch, "E169.middle", {"position": v(120, 0) * mm});
            skCircle(sketch, "E170", {"center": v(98.15, 21.85) * mm, "radius": 1.05 * mm});
            skCircle(sketch, "E171", {"center": v(141.85, 21.85) * mm, "radius": 1.05 * mm});
            skCircle(sketch, "E172", {"center": v(141.85, -21.85) * mm, "radius": 1.05 * mm});
            skCircle(sketch, "E173", {"center": v(98.15, -21.85) * mm, "radius": 1.05 * mm});
            skSolve(sketch);
        }
        {
            var Q0;
            Q0=qSketchRegion(id+"F32",true);
            extrude(context, id + "F33", {"entities" : qUnion([Q0]), "operationType" : NewBodyOperationType.REMOVE, "endBound" : BoundingType.THROUGH_ALL, "oppositeDirection" : true, "depth" : 25 * mm});
        }
        {
            var Q0;
            Q0=qCreatedBy(makeId("Top.planeOp"),FACE);
            var sketch = newSketch(context, id + "F34", { "sketchPlane" : qUnion([Q0])});
            skLineSegment(sketch, "E174", {"start": v(0, 0) * mm, "end": v(120, 0) * mm, "construction": true});
            skLineSegment(sketch, "E175", {"start": v(120, 0) * mm, "end": v(120, -11.75) * mm, "construction": true});
            skLineSegment(sketch, "E176", {"start": v(120, -11.75) * mm, "end": v(108.25, -11.75) * mm, "construction": true});
            skLineSegment(sketch, "E177", {"start": v(120, 0) * mm, "end": v(120, 11.75) * mm, "construction": true});
            skLineSegment(sketch, "E178.bottom", {"start": v(105, -1.5) * mm, "end": v(111.5, -1.5) * mm});
            skLineSegment(sketch, "E178.top", {"start": v(105, -22) * mm, "end": v(111.5, -22) * mm});
            skLineSegment(sketch, "E178.left", {"start": v(98, -8.5) * mm, "end": v(98, -15) * mm});
            skLineSegment(sketch, "E178.right", {"start": v(118.5, -8.5) * mm, "end": v(118.5, -15) * mm});
            skPoint(sketch, "E178.middle", {"position": v(108.25, -11.75) * mm});
            skPoint(sketch, "E179.visualSharp", {"position": v(98, -22) * mm});
            skArc(sketch, "E179.filletArc", {"start": v(98, -15) * mm, "mid": v(100.05, -19.95) * mm, "end": v(105, -22) * mm});
            skPoint(sketch, "E180.visualSharp", {"position": v(118.5, -1.5) * mm});
            skArc(sketch, "E180.filletArc", {"start": v(118.5, -8.5) * mm, "mid": v(116.45, -3.55) * mm, "end": v(111.5, -1.5) * mm});
            skPoint(sketch, "E181.visualSharp", {"position": v(98, -1.5) * mm});
            skArc(sketch, "E181.filletArc", {"start": v(105, -1.5) * mm, "mid": v(100.05, -3.55) * mm, "end": v(98, -8.5) * mm});
            skPoint(sketch, "E182.visualSharp", {"position": v(118.5, -22) * mm});
            skArc(sketch, "E182.filletArc", {"start": v(111.5, -22) * mm, "mid": v(116.45, -19.95) * mm, "end": v(118.5, -15) * mm});
            skArc(sketch, "E183.0.1.0", {"start": v(118.5, 15) * mm, "mid": v(116.45, 19.95) * mm, "end": v(111.5, 22) * mm});
            skPoint(sketch, "E183.0.1.1", {"position": v(108.25, 11.75) * mm});
            skPoint(sketch, "E183.0.1.2", {"position": v(98, 1.5) * mm});
            skArc(sketch, "E183.0.1.3", {"start": v(105, 22) * mm, "mid": v(100.05, 19.95) * mm, "end": v(98, 15) * mm});
            skArc(sketch, "E183.0.1.4", {"start": v(111.5, 1.5) * mm, "mid": v(116.45, 3.55) * mm, "end": v(118.5, 8.5) * mm});
            skLineSegment(sketch, "E183.0.1.5", {"start": v(98, 15) * mm, "end": v(98, 8.5) * mm});
            skPoint(sketch, "E183.0.1.6", {"position": v(118.5, 22) * mm});
            skArc(sketch, "E183.0.1.7", {"start": v(98, 8.5) * mm, "mid": v(100.05, 3.55) * mm, "end": v(105, 1.5) * mm});
            skPoint(sketch, "E183.0.1.8", {"position": v(118.5, 1.5) * mm});
            skLineSegment(sketch, "E183.0.1.9", {"start": v(105, 1.5) * mm, "end": v(111.5, 1.5) * mm});
            skPoint(sketch, "E183.0.1.10", {"position": v(98, 22) * mm});
            skLineSegment(sketch, "E183.0.1.11", {"start": v(118.5, 15) * mm, "end": v(118.5, 8.5) * mm});
            skLineSegment(sketch, "E183.0.1.12", {"start": v(105, 22) * mm, "end": v(111.5, 22) * mm});
            skLineSegment(sketch, "E183.0.1.13", {"start": v(120, 11.75) * mm, "end": v(108.25, 11.75) * mm, "construction": true});
            skArc(sketch, "E183.0.2.0", {"start": v(118.5, 38.5) * mm, "mid": v(116.45, 43.45) * mm, "end": v(111.5, 45.5) * mm});
            skPoint(sketch, "E183.0.2.1", {"position": v(108.25, 35.25) * mm});
            skPoint(sketch, "E183.0.2.2", {"position": v(98, 25) * mm});
            skArc(sketch, "E183.0.2.3", {"start": v(105, 45.5) * mm, "mid": v(100.05, 43.45) * mm, "end": v(98, 38.5) * mm});
            skArc(sketch, "E183.0.2.4", {"start": v(111.5, 25) * mm, "mid": v(116.45, 27.05) * mm, "end": v(118.5, 32) * mm});
            skLineSegment(sketch, "E183.0.2.5", {"start": v(98, 38.5) * mm, "end": v(98, 32) * mm});
            skPoint(sketch, "E183.0.2.6", {"position": v(118.5, 45.5) * mm});
            skArc(sketch, "E183.0.2.7", {"start": v(98, 32) * mm, "mid": v(100.05, 27.05) * mm, "end": v(105, 25) * mm});
            skPoint(sketch, "E183.0.2.8", {"position": v(118.5, 25) * mm});
            skLineSegment(sketch, "E183.0.2.9", {"start": v(105, 25) * mm, "end": v(111.5, 25) * mm});
            skPoint(sketch, "E183.0.2.10", {"position": v(98, 45.5) * mm});
            skLineSegment(sketch, "E183.0.2.11", {"start": v(118.5, 38.5) * mm, "end": v(118.5, 32) * mm});
            skLineSegment(sketch, "E183.0.2.12", {"start": v(105, 45.5) * mm, "end": v(111.5, 45.5) * mm});
            skLineSegment(sketch, "E183.0.2.13", {"start": v(120, 35.25) * mm, "end": v(108.25, 35.25) * mm, "construction": true});
            skArc(sketch, "E183.1.0.0", {"start": v(142, -8.5) * mm, "mid": v(139.95, -3.55) * mm, "end": v(135, -1.5) * mm});
            skPoint(sketch, "E183.1.0.1", {"position": v(131.75, -11.75) * mm});
            skPoint(sketch, "E183.1.0.2", {"position": v(121.5, -22) * mm});
            skArc(sketch, "E183.1.0.3", {"start": v(128.5, -1.5) * mm, "mid": v(123.55, -3.55) * mm, "end": v(121.5, -8.5) * mm});
            skArc(sketch, "E183.1.0.4", {"start": v(135, -22) * mm, "mid": v(139.95, -19.95) * mm, "end": v(142, -15) * mm});
            skLineSegment(sketch, "E183.1.0.5", {"start": v(121.5, -8.5) * mm, "end": v(121.5, -15) * mm});
            skPoint(sketch, "E183.1.0.6", {"position": v(142, -1.5) * mm});
            skArc(sketch, "E183.1.0.7", {"start": v(121.5, -15) * mm, "mid": v(123.55, -19.95) * mm, "end": v(128.5, -22) * mm});
            skPoint(sketch, "E183.1.0.8", {"position": v(142, -22) * mm});
            skLineSegment(sketch, "E183.1.0.9", {"start": v(128.5, -22) * mm, "end": v(135, -22) * mm});
            skPoint(sketch, "E183.1.0.10", {"position": v(121.5, -1.5) * mm});
            skLineSegment(sketch, "E183.1.0.11", {"start": v(142, -8.5) * mm, "end": v(142, -15) * mm});
            skLineSegment(sketch, "E183.1.0.12", {"start": v(128.5, -1.5) * mm, "end": v(135, -1.5) * mm});
            skLineSegment(sketch, "E183.1.0.13", {"start": v(143.5, -11.75) * mm, "end": v(131.75, -11.75) * mm, "construction": true});
            skArc(sketch, "E183.1.1.0", {"start": v(142, 15) * mm, "mid": v(139.95, 19.95) * mm, "end": v(135, 22) * mm});
            skPoint(sketch, "E183.1.1.1", {"position": v(131.75, 11.75) * mm});
            skPoint(sketch, "E183.1.1.2", {"position": v(121.5, 1.5) * mm});
            skArc(sketch, "E183.1.1.3", {"start": v(128.5, 22) * mm, "mid": v(123.55, 19.95) * mm, "end": v(121.5, 15) * mm});
            skArc(sketch, "E183.1.1.4", {"start": v(135, 1.5) * mm, "mid": v(139.95, 3.55) * mm, "end": v(142, 8.5) * mm});
            skLineSegment(sketch, "E183.1.1.5", {"start": v(121.5, 15) * mm, "end": v(121.5, 8.5) * mm});
            skPoint(sketch, "E183.1.1.6", {"position": v(142, 22) * mm});
            skArc(sketch, "E183.1.1.7", {"start": v(121.5, 8.5) * mm, "mid": v(123.55, 3.55) * mm, "end": v(128.5, 1.5) * mm});
            skPoint(sketch, "E183.1.1.8", {"position": v(142, 1.5) * mm});
            skLineSegment(sketch, "E183.1.1.9", {"start": v(128.5, 1.5) * mm, "end": v(135, 1.5) * mm});
            skPoint(sketch, "E183.1.1.10", {"position": v(121.5, 22) * mm});
            skLineSegment(sketch, "E183.1.1.11", {"start": v(142, 15) * mm, "end": v(142, 8.5) * mm});
            skLineSegment(sketch, "E183.1.1.12", {"start": v(128.5, 22) * mm, "end": v(135, 22) * mm});
            skLineSegment(sketch, "E183.1.1.13", {"start": v(143.5, 11.75) * mm, "end": v(131.75, 11.75) * mm, "construction": true});
            skArc(sketch, "E183.1.2.0", {"start": v(142, 38.5) * mm, "mid": v(139.95, 43.45) * mm, "end": v(135, 45.5) * mm});
            skPoint(sketch, "E183.1.2.1", {"position": v(131.75, 35.25) * mm});
            skPoint(sketch, "E183.1.2.2", {"position": v(121.5, 25) * mm});
            skArc(sketch, "E183.1.2.3", {"start": v(128.5, 45.5) * mm, "mid": v(123.55, 43.45) * mm, "end": v(121.5, 38.5) * mm});
            skArc(sketch, "E183.1.2.4", {"start": v(135, 25) * mm, "mid": v(139.95, 27.05) * mm, "end": v(142, 32) * mm});
            skLineSegment(sketch, "E183.1.2.5", {"start": v(121.5, 38.5) * mm, "end": v(121.5, 32) * mm});
            skPoint(sketch, "E183.1.2.6", {"position": v(142, 45.5) * mm});
            skArc(sketch, "E183.1.2.7", {"start": v(121.5, 32) * mm, "mid": v(123.55, 27.05) * mm, "end": v(128.5, 25) * mm});
            skPoint(sketch, "E183.1.2.8", {"position": v(142, 25) * mm});
            skLineSegment(sketch, "E183.1.2.9", {"start": v(128.5, 25) * mm, "end": v(135, 25) * mm});
            skPoint(sketch, "E183.1.2.10", {"position": v(121.5, 45.5) * mm});
            skLineSegment(sketch, "E183.1.2.11", {"start": v(142, 38.5) * mm, "end": v(142, 32) * mm});
            skLineSegment(sketch, "E183.1.2.12", {"start": v(128.5, 45.5) * mm, "end": v(135, 45.5) * mm});
            skLineSegment(sketch, "E183.1.2.13", {"start": v(143.5, 35.25) * mm, "end": v(131.75, 35.25) * mm, "construction": true});
            skArc(sketch, "E183.2.0.0", {"start": v(165.5, -8.5) * mm, "mid": v(163.45, -3.55) * mm, "end": v(158.5, -1.5) * mm});
            skPoint(sketch, "E183.2.0.1", {"position": v(155.25, -11.75) * mm});
            skPoint(sketch, "E183.2.0.2", {"position": v(145, -22) * mm});
            skArc(sketch, "E183.2.0.3", {"start": v(152, -1.5) * mm, "mid": v(147.05, -3.55) * mm, "end": v(145, -8.5) * mm});
            skArc(sketch, "E183.2.0.4", {"start": v(158.5, -22) * mm, "mid": v(163.45, -19.95) * mm, "end": v(165.5, -15) * mm});
            skLineSegment(sketch, "E183.2.0.5", {"start": v(145, -8.5) * mm, "end": v(145, -15) * mm});
            skPoint(sketch, "E183.2.0.6", {"position": v(165.5, -1.5) * mm});
            skArc(sketch, "E183.2.0.7", {"start": v(145, -15) * mm, "mid": v(147.05, -19.95) * mm, "end": v(152, -22) * mm});
            skPoint(sketch, "E183.2.0.8", {"position": v(165.5, -22) * mm});
            skLineSegment(sketch, "E183.2.0.9", {"start": v(152, -22) * mm, "end": v(158.5, -22) * mm});
            skPoint(sketch, "E183.2.0.10", {"position": v(145, -1.5) * mm});
            skLineSegment(sketch, "E183.2.0.11", {"start": v(165.5, -8.5) * mm, "end": v(165.5, -15) * mm});
            skLineSegment(sketch, "E183.2.0.12", {"start": v(152, -1.5) * mm, "end": v(158.5, -1.5) * mm});
            skLineSegment(sketch, "E183.2.0.13", {"start": v(167, -11.75) * mm, "end": v(155.25, -11.75) * mm, "construction": true});
            skArc(sketch, "E183.2.1.0", {"start": v(165.5, 15) * mm, "mid": v(163.45, 19.95) * mm, "end": v(158.5, 22) * mm});
            skPoint(sketch, "E183.2.1.1", {"position": v(155.25, 11.75) * mm});
            skPoint(sketch, "E183.2.1.2", {"position": v(145, 1.5) * mm});
            skArc(sketch, "E183.2.1.3", {"start": v(152, 22) * mm, "mid": v(147.05, 19.95) * mm, "end": v(145, 15) * mm});
            skArc(sketch, "E183.2.1.4", {"start": v(158.5, 1.5) * mm, "mid": v(163.45, 3.55) * mm, "end": v(165.5, 8.5) * mm});
            skLineSegment(sketch, "E183.2.1.5", {"start": v(145, 15) * mm, "end": v(145, 8.5) * mm});
            skPoint(sketch, "E183.2.1.6", {"position": v(165.5, 22) * mm});
            skArc(sketch, "E183.2.1.7", {"start": v(145, 8.5) * mm, "mid": v(147.05, 3.55) * mm, "end": v(152, 1.5) * mm});
            skPoint(sketch, "E183.2.1.8", {"position": v(165.5, 1.5) * mm});
            skLineSegment(sketch, "E183.2.1.9", {"start": v(152, 1.5) * mm, "end": v(158.5, 1.5) * mm});
            skPoint(sketch, "E183.2.1.10", {"position": v(145, 22) * mm});
            skLineSegment(sketch, "E183.2.1.11", {"start": v(165.5, 15) * mm, "end": v(165.5, 8.5) * mm});
            skLineSegment(sketch, "E183.2.1.12", {"start": v(152, 22) * mm, "end": v(158.5, 22) * mm});
            skLineSegment(sketch, "E183.2.1.13", {"start": v(167, 11.75) * mm, "end": v(155.25, 11.75) * mm, "construction": true});
            skArc(sketch, "E183.2.2.0", {"start": v(165.5, 38.5) * mm, "mid": v(163.45, 43.45) * mm, "end": v(158.5, 45.5) * mm});
            skPoint(sketch, "E183.2.2.1", {"position": v(155.25, 35.25) * mm});
            skPoint(sketch, "E183.2.2.2", {"position": v(145, 25) * mm});
            skArc(sketch, "E183.2.2.3", {"start": v(152, 45.5) * mm, "mid": v(147.05, 43.45) * mm, "end": v(145, 38.5) * mm});
            skArc(sketch, "E183.2.2.4", {"start": v(158.5, 25) * mm, "mid": v(163.45, 27.05) * mm, "end": v(165.5, 32) * mm});
            skLineSegment(sketch, "E183.2.2.5", {"start": v(145, 38.5) * mm, "end": v(145, 32) * mm});
            skPoint(sketch, "E183.2.2.6", {"position": v(165.5, 45.5) * mm});
            skArc(sketch, "E183.2.2.7", {"start": v(145, 32) * mm, "mid": v(147.05, 27.05) * mm, "end": v(152, 25) * mm});
            skPoint(sketch, "E183.2.2.8", {"position": v(165.5, 25) * mm});
            skLineSegment(sketch, "E183.2.2.9", {"start": v(152, 25) * mm, "end": v(158.5, 25) * mm});
            skPoint(sketch, "E183.2.2.10", {"position": v(145, 45.5) * mm});
            skLineSegment(sketch, "E183.2.2.11", {"start": v(165.5, 38.5) * mm, "end": v(165.5, 32) * mm});
            skLineSegment(sketch, "E183.2.2.12", {"start": v(152, 45.5) * mm, "end": v(158.5, 45.5) * mm});
            skLineSegment(sketch, "E183.2.2.13", {"start": v(167, 35.25) * mm, "end": v(155.25, 35.25) * mm, "construction": true});
            skLineSegment(sketch, "E183.direction1", {"start": v(98, -22) * mm, "end": v(121.5, -22) * mm, "construction": true});
            skLineSegment(sketch, "E183.direction2", {"start": v(98, -22) * mm, "end": v(98, 1.5) * mm, "construction": true});
            skSolve(sketch);
        }
        {
            var Q0;
            Q0=makeQuery(id+"F34.imprint","IMPRINT",FACE,{"disambiguationData":[TD([[makeQuery(id+"F34.imprint","IMPRINT",EDGE,{"derivedFrom":sQuery(id+"F34.wireOp",EDGE,"E178.bottom")}),-1.0]])]});
            var Q1;
            Q1=makeQuery(id+"F34.imprint","IMPRINT",FACE,{"disambiguationData":[TD([[makeQuery(id+"F34.imprint","IMPRINT",EDGE,{"derivedFrom":sQuery(id+"F34.wireOp",EDGE,"E183.0.1.0")}),1.0]])]});
            var Q2;
            Q2=makeQuery(id+"F34.imprint","IMPRINT",FACE,{"disambiguationData":[TD([[makeQuery(id+"F34.imprint","IMPRINT",EDGE,{"derivedFrom":sQuery(id+"F34.wireOp",EDGE,"E183.1.0.0")}),1.0]])]});
            var Q3;
            Q3=makeQuery(id+"F34.imprint","IMPRINT",FACE,{"disambiguationData":[TD([[makeQuery(id+"F34.imprint","IMPRINT",EDGE,{"derivedFrom":sQuery(id+"F34.wireOp",EDGE,"E183.1.1.0")}),1.0]])]});
            var Q4;
            Q4=makeQuery(id+"F34.imprint","IMPRINT",FACE,{"disambiguationData":[TD([[makeQuery(id+"F34.imprint","IMPRINT",EDGE,{"derivedFrom":sQuery(id+"F34.wireOp",EDGE,"E183.0.1.0")}),1.0]])]});
            var Q5;
            Q5=makeQuery(id+"F34.imprint","IMPRINT",FACE,{"disambiguationData":[TD([[makeQuery(id+"F34.imprint","IMPRINT",EDGE,{"derivedFrom":sQuery(id+"F34.wireOp",EDGE,"E183.1.1.0")}),1.0]])]});
            var Q6;
            Q6=makeQuery(id+"F34.imprint","IMPRINT",FACE,{"disambiguationData":[TD([[makeQuery(id+"F34.imprint","IMPRINT",EDGE,{"derivedFrom":sQuery(id+"F34.wireOp",EDGE,"E183.1.0.0")}),1.0]])]});
            var Q7;
            Q7=makeQuery(id+"F34.imprint","IMPRINT",FACE,{"disambiguationData":[TD([[makeQuery(id+"F34.imprint","IMPRINT",EDGE,{"derivedFrom":sQuery(id+"F34.wireOp",EDGE,"E178.bottom")}),-1.0]])]});
            extrude(context, id + "F35", {"entities" : qUnion([Q0, Q1, Q2, Q3, Q4, Q5, Q6, Q7]), "operationType" : NewBodyOperationType.REMOVE, "endBound" : BoundingType.THROUGH_ALL, "oppositeDirection" : true, "depth" : 25 * mm});
        }
        {
            var Q0;
            Q0=qCreatedBy(makeId("Top.planeOp"),FACE);
            var sketch = newSketch(context, id + "F36", { "sketchPlane" : qUnion([Q0])});
            skLineSegment(sketch, "E184", {"start": v(0, 0) * mm, "end": v(-120, 0) * mm, "construction": true});
            skLineSegment(sketch, "E185.bottom", {"start": v(-149.5, -29.5) * mm, "end": v(-90.5, -29.5) * mm});
            skLineSegment(sketch, "E185.top", {"start": v(-149.5, 29.5) * mm, "end": v(-90.5, 29.5) * mm});
            skLineSegment(sketch, "E185.left", {"start": v(-149.5, -29.5) * mm, "end": v(-149.5, 29.5) * mm});
            skLineSegment(sketch, "E185.right", {"start": v(-90.5, -29.5) * mm, "end": v(-90.5, 29.5) * mm});
            skPoint(sketch, "E185.middle", {"position": v(-120, 0) * mm});
            skLineSegment(sketch, "E186.bottom", {"start": v(-141.85, 21.85) * mm, "end": v(-98.15, 21.85) * mm, "construction": true});
            skLineSegment(sketch, "E186.top", {"start": v(-141.85, -21.85) * mm, "end": v(-98.15, -21.85) * mm, "construction": true});
            skLineSegment(sketch, "E186.left", {"start": v(-141.85, 21.85) * mm, "end": v(-141.85, -21.85) * mm, "construction": true});
            skLineSegment(sketch, "E186.right", {"start": v(-98.15, 21.85) * mm, "end": v(-98.15, -21.85) * mm, "construction": true});
            skCircle(sketch, "E187", {"center": v(-141.85, 21.85) * mm, "radius": 1.05 * mm});
            skCircle(sketch, "E188", {"center": v(-98.15, 21.85) * mm, "radius": 1.05 * mm});
            skCircle(sketch, "E189", {"center": v(-98.15, -21.85) * mm, "radius": 1.05 * mm});
            skCircle(sketch, "E190", {"center": v(-141.85, -21.85) * mm, "radius": 1.05 * mm});
            skLineSegment(sketch, "E191.bottom", {"start": v(-137.5, 17.5) * mm, "end": v(-102.5, 17.5) * mm});
            skLineSegment(sketch, "E191.top", {"start": v(-137.5, -17.5) * mm, "end": v(-102.5, -17.5) * mm});
            skLineSegment(sketch, "E191.left", {"start": v(-137.5, 17.5) * mm, "end": v(-137.5, -17.5) * mm});
            skLineSegment(sketch, "E191.right", {"start": v(-102.5, 17.5) * mm, "end": v(-102.5, -17.5) * mm});
            skSolve(sketch);
        }
        {
            var Q0;
            Q0=qSketchRegion(id+"F36",true);
            extrude(context, id + "F37", {"entities" : qUnion([Q0]), "oppositeDirection" : true, "depth" : (getVariable(context, 'Grosor') / 2) * mm, "hasSecondDirection" : true, "secondDirectionOppositeDirection" : false, "secondDirectionDepth" : 3 * mm});
        }
        {
            var Q0;
            Q0=qCreatedBy(makeId("Top.planeOp"),FACE);
            var sketch = newSketch(context, id + "F38", { "sketchPlane" : qUnion([Q0])});
            skLineSegment(sketch, "E192", {"start": v(0, 0) * mm, "end": v(-120, 0) * mm, "construction": true});
            skLineSegment(sketch, "E193.bottom", {"start": v(-141.85, 21.85) * mm, "end": v(-98.15, 21.85) * mm, "construction": true});
            skLineSegment(sketch, "E193.top", {"start": v(-141.85, -21.85) * mm, "end": v(-98.15, -21.85) * mm, "construction": true});
            skLineSegment(sketch, "E193.left", {"start": v(-141.85, 21.85) * mm, "end": v(-141.85, -21.85) * mm, "construction": true});
            skLineSegment(sketch, "E193.right", {"start": v(-98.15, 21.85) * mm, "end": v(-98.15, -21.85) * mm, "construction": true});
            skPoint(sketch, "E193.middle", {"position": v(-120, 0) * mm});
            skCircle(sketch, "E194", {"center": v(-141.85, 21.85) * mm, "radius": 2.1 * mm});
            skCircle(sketch, "E195", {"center": v(-98.15, 21.85) * mm, "radius": 2.1 * mm});
            skCircle(sketch, "E196", {"center": v(-98.15, -21.85) * mm, "radius": 2.1 * mm});
            skCircle(sketch, "E197", {"center": v(-141.85, -21.85) * mm, "radius": 2.1 * mm});
            skLineSegment(sketch, "E198.bottom", {"start": v(-150, -30) * mm, "end": v(-90, -30) * mm});
            skLineSegment(sketch, "E198.top", {"start": v(-150, 30) * mm, "end": v(-90, 30) * mm});
            skLineSegment(sketch, "E198.left", {"start": v(-150, -30) * mm, "end": v(-150, 30) * mm});
            skLineSegment(sketch, "E198.right", {"start": v(-90, -30) * mm, "end": v(-90, 30) * mm});
            skSolve(sketch);
        }
        {
            var Q0;
            Q0=qSketchRegion(id+"F38",true);
            extrude(context, id + "F39", {"entities" : qUnion([Q0]), "operationType" : NewBodyOperationType.REMOVE, "depth" : 25 * mm});
        }
        {
            var Q0;
            Q0=makeQuery(id+"F27.opExtrude","SWEPT_EDGE",EDGE,{"disambiguationData":[OSD([sQuery(id+"F26.wireOp",EDGE,"E152.bottom"),sQuery(id+"F26.wireOp",EDGE,"E152.right")])]});
            var Q1;
            Q1=makeQuery(id+"F27.opExtrude","SWEPT_EDGE",EDGE,{"disambiguationData":[OSD([sQuery(id+"F26.wireOp",EDGE,"E152.bottom"),sQuery(id+"F26.wireOp",EDGE,"E152.left")])]});
            var Q2;
            Q2=makeQuery(id+"F37.opExtrude","SWEPT_EDGE",EDGE,{"disambiguationData":[OSD([sQuery(id+"F36.wireOp",EDGE,"E185.bottom"),sQuery(id+"F36.wireOp",EDGE,"E185.right")])]});
            var Q3;
            Q3=makeQuery(id+"F37.opExtrude","SWEPT_EDGE",EDGE,{"disambiguationData":[OSD([sQuery(id+"F36.wireOp",EDGE,"E185.bottom"),sQuery(id+"F36.wireOp",EDGE,"E185.left")])]});
            fillet(context, id + "F40", {"entities" : qUnion([Q0, Q1, Q2, Q3]), "radius" : 3 * mm, "tangentPropagation" : true, "allowEdgeOverflow" : false});
        }
        {
            var Q0;
            Q0=makeQuery(id+"F37.opExtrude","SWEPT_EDGE",EDGE,{"disambiguationData":[OSD([sQuery(id+"F36.wireOp",EDGE,"E185.top"),sQuery(id+"F36.wireOp",EDGE,"E185.left")])]});
            var Q1;
            Q1=makeQuery(id+"F37.opExtrude","SWEPT_EDGE",EDGE,{"disambiguationData":[OSD([sQuery(id+"F36.wireOp",EDGE,"E185.top"),sQuery(id+"F36.wireOp",EDGE,"E185.right")])]});
            var Q2;
            Q2=makeQuery(id+"F27.opExtrude","SWEPT_EDGE",EDGE,{"disambiguationData":[OSD([sQuery(id+"F26.wireOp",EDGE,"E152.top"),sQuery(id+"F26.wireOp",EDGE,"E152.left")])]});
            var Q3;
            Q3=makeQuery(id+"F27.opExtrude","SWEPT_EDGE",EDGE,{"disambiguationData":[OSD([sQuery(id+"F26.wireOp",EDGE,"E152.top"),sQuery(id+"F26.wireOp",EDGE,"E152.right")])]});
            chamfer(context, id + "F41", {"entities" : qUnion([Q0, Q1, Q2, Q3]), "width" : 3 * mm, "tangentPropagation" : true});
        }
    });
